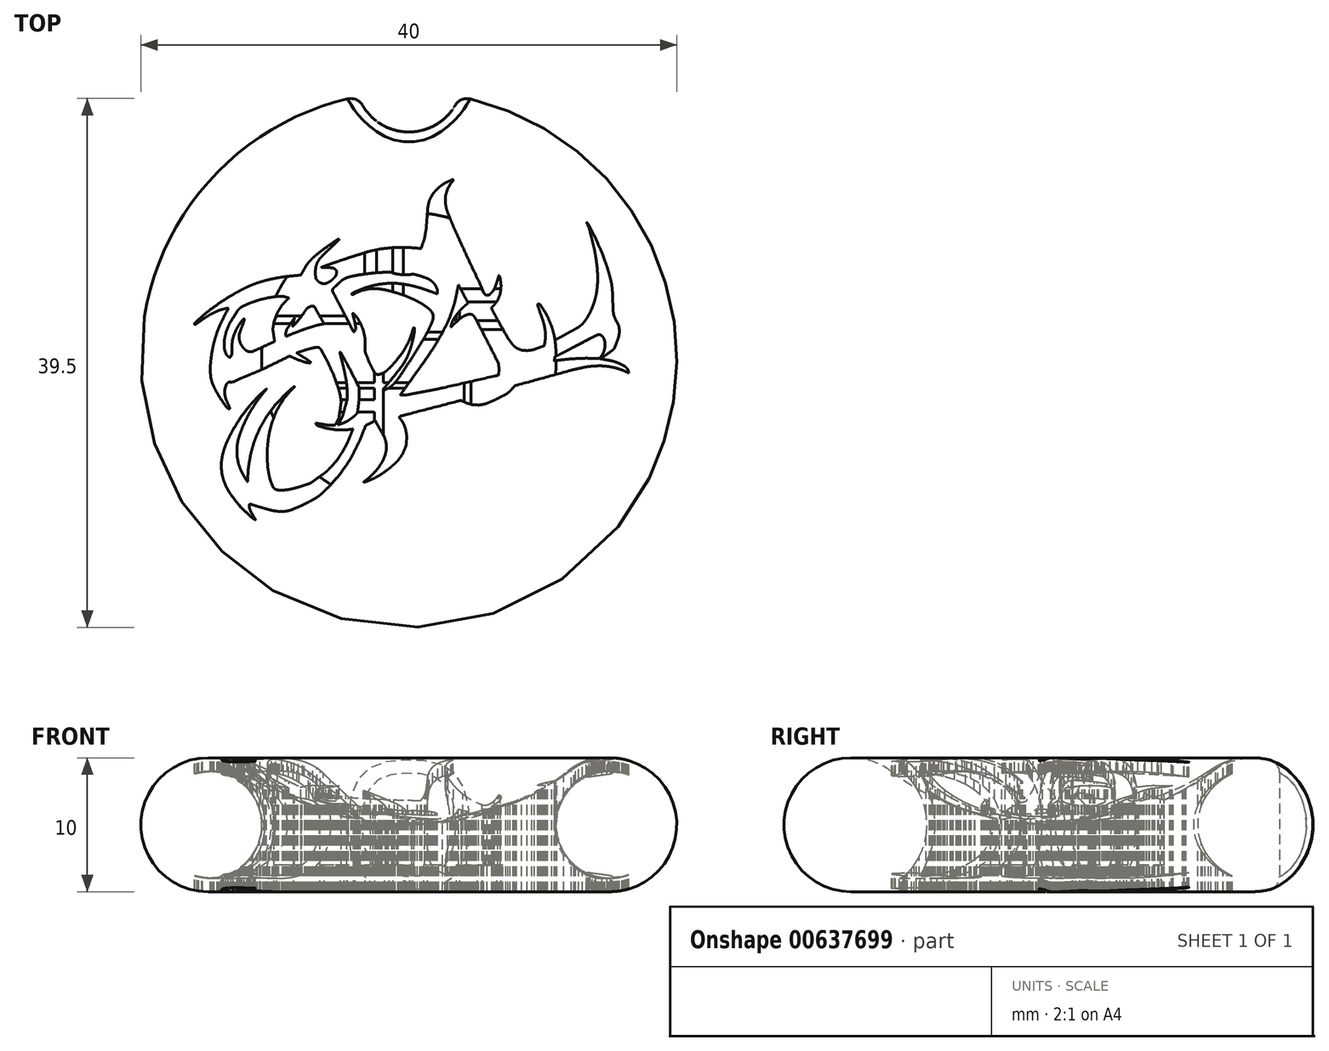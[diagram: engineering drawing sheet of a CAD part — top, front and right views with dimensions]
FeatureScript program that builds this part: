
annotation { "Feature Type Name" : "Feature", "Feature Type Description" : "" }
export const myFeature = defineFeature(function(context is Context, id is Id, definition is map)
    precondition{}
    {
        {
            var Q0;
            Q0=qCreatedBy(makeId("Front.planeOp"),FACE);
            var sketch = newSketch(context, id + "F0", { "sketchPlane" : qUnion([Q0])});
            skArc(sketch, "E0", {"start": v(-12, 9) * mm, "mid": v(-19.74, 6.58) * mm, "end": v(-15, 0) * mm});
            skArc(sketch, "E1", {"start": v(-12, 9) * mm, "mid": v(-6.32, 6.03) * mm, "end": v(0, 5) * mm});
            skLineSegment(sketch, "E2", {"start": v(-15, 0) * mm, "end": v(0, 0) * mm});
            skLineSegment(sketch, "E3", {"start": v(0, 0) * mm, "end": v(0, 5) * mm});
            skSolve(sketch);
        }
        {
            var Q0;
            Q0 = qSketchRegion(id + "F0", true);
            var Q1;
            Q1=makeQuery(id+"F0.imprint","IMPRINT",FACE,{"disambiguationData":[TD([[makeQuery(id+"F0.imprint","IMPRINT",EDGE,{"derivedFrom":sQuery(id+"F0.wireOp",EDGE,"E0")}),1.0]])]});
            var Q2;
            Q2=sQuery(id+"F0.wireOp",EDGE,"E3");
            revolve(context, id + "F1", {"entities" : qUnion([Q0, Q1]), "axis" : qUnion([Q2]), "revolveType" : RevolveType.FULL});
        }
        {
            var Q0;
            Q0=qCreatedBy(makeId("Top.planeOp"),FACE);
            cPlane(context, id + "F2", {"entities" : qUnion([Q0]), "cplaneType" : CPlaneType.OFFSET, "offset" : 10 * mm, "width" : 150 * mm, "height" : 150 * mm});
        }
        {
            var Q0;
            Q0=qCreatedBy(id+"F2.planeOp",FACE);
            var sketch = newSketch(context, id + "F3", { "sketchPlane" : qUnion([Q0])});
            skLineSegment(sketch, "E4", {"start": v(-7.6, 3.85) * mm, "end": v(-7.64, 3.77) * mm});
            skLineSegment(sketch, "E5", {"start": v(-7.64, 3.77) * mm, "end": v(-8.04, 3.2) * mm});
            skLineSegment(sketch, "E6", {"start": v(-8.04, 3.2) * mm, "end": v(-8.48, 2.66) * mm});
            skLineSegment(sketch, "E7", {"start": v(-8.48, 2.66) * mm, "end": v(-8.57, 2.56) * mm});
            skLineSegment(sketch, "E8", {"start": v(-8.57, 2.56) * mm, "end": v(-8.58, 2.56) * mm});
            skLineSegment(sketch, "E9", {"start": v(-8.58, 2.56) * mm, "end": v(-8.6, 2.53) * mm});
            skLineSegment(sketch, "E10", {"start": v(-8.6, 2.53) * mm, "end": v(-8.67, 2.5) * mm});
            skLineSegment(sketch, "E11", {"start": v(-8.67, 2.5) * mm, "end": v(-8.69, 2.48) * mm});
            skLineSegment(sketch, "E12", {"start": v(-8.69, 2.48) * mm, "end": v(-8.68, 2.52) * mm});
            skLineSegment(sketch, "E13", {"start": v(-8.68, 2.52) * mm, "end": v(-8.65, 2.7) * mm});
            skLineSegment(sketch, "E14", {"start": v(-8.65, 2.7) * mm, "end": v(-8.61, 2.84) * mm});
            skLineSegment(sketch, "E15", {"start": v(-8.61, 2.84) * mm, "end": v(-8.6, 2.87) * mm});
            skLineSegment(sketch, "E16", {"start": v(-8.6, 2.87) * mm, "end": v(-8.6, 2.9) * mm});
            skLineSegment(sketch, "E17", {"start": v(-8.6, 2.9) * mm, "end": v(-8.54, 3.1) * mm});
            skLineSegment(sketch, "E18", {"start": v(-8.9, 0.27) * mm, "end": v(-9.02, 0.2) * mm});
            skLineSegment(sketch, "E19", {"start": v(-9.02, 0.2) * mm, "end": v(-10.84, -0.68) * mm});
            skLineSegment(sketch, "E20", {"start": v(-10.84, -0.68) * mm, "end": v(-11.02, -0.77) * mm});
            skLineSegment(sketch, "E21", {"start": v(-11.02, -0.77) * mm, "end": v(-11.15, -0.83) * mm});
            skLineSegment(sketch, "E22", {"start": v(-11.15, -0.83) * mm, "end": v(-12.52, -1.4) * mm});
            skLineSegment(sketch, "E23", {"start": v(-12.52, -1.4) * mm, "end": v(-12.65, -1.45) * mm});
            skLineSegment(sketch, "E24", {"start": v(-12.65, -1.45) * mm, "end": v(-12.69, -1.46) * mm});
            skLineSegment(sketch, "E25", {"start": v(-12.69, -1.46) * mm, "end": v(-12.84, -1.54) * mm});
            skLineSegment(sketch, "E26", {"start": v(-12.84, -1.54) * mm, "end": v(-12.99, -1.62) * mm});
            skLineSegment(sketch, "E27", {"start": v(-12.99, -1.62) * mm, "end": v(-13.02, -1.63) * mm});
            skLineSegment(sketch, "E28", {"start": v(-13.02, -1.63) * mm, "end": v(-13.04, -1.64) * mm});
            skLineSegment(sketch, "E29", {"start": v(-13.04, -1.64) * mm, "end": v(-13.16, -1.68) * mm});
            skLineSegment(sketch, "E30", {"start": v(-13.16, -1.68) * mm, "end": v(-13.28, -1.68) * mm});
            skLineSegment(sketch, "E31", {"start": v(-13.28, -1.68) * mm, "end": v(-13.3, -1.68) * mm});
            skLineSegment(sketch, "E32", {"start": v(-13.3, -1.68) * mm, "end": v(-13.33, -1.68) * mm});
            skLineSegment(sketch, "E33", {"start": v(-13.33, -1.68) * mm, "end": v(-13.4, -1.68) * mm});
            skLineSegment(sketch, "E34", {"start": v(-13.4, -1.68) * mm, "end": v(-13.49, -1.7) * mm});
            skLineSegment(sketch, "E35", {"start": v(-13.49, -1.7) * mm, "end": v(-13.55, -1.75) * mm});
            skLineSegment(sketch, "E36", {"start": v(-13.55, -1.75) * mm, "end": v(-13.6, -1.81) * mm});
            skLineSegment(sketch, "E37", {"start": v(-13.6, -1.81) * mm, "end": v(-13.6, -1.83) * mm});
            skLineSegment(sketch, "E38", {"start": v(-13.6, -1.83) * mm, "end": v(-13.65, -1.9) * mm});
            skLineSegment(sketch, "E39", {"start": v(-13.65, -1.9) * mm, "end": v(-13.73, -2.15) * mm});
            skLineSegment(sketch, "E40", {"start": v(-13.73, -2.15) * mm, "end": v(-13.76, -2.46) * mm});
            skLineSegment(sketch, "E41", {"start": v(-13.76, -2.46) * mm, "end": v(-13.71, -2.77) * mm});
            skLineSegment(sketch, "E42", {"start": v(-13.71, -2.77) * mm, "end": v(-13.63, -3.01) * mm});
            skLineSegment(sketch, "E43", {"start": v(-13.63, -3.01) * mm, "end": v(-13.6, -3.09) * mm});
            skLineSegment(sketch, "E44", {"start": v(-13.6, -3.09) * mm, "end": v(-13.58, -3.13) * mm});
            skLineSegment(sketch, "E45", {"start": v(-13.58, -3.13) * mm, "end": v(-13.37, -3.6) * mm});
            skLineSegment(sketch, "E46", {"start": v(-13.37, -3.6) * mm, "end": v(-13.35, -3.65) * mm});
            skLineSegment(sketch, "E47", {"start": v(-13.35, -3.65) * mm, "end": v(-13.42, -3.7) * mm});
            skLineSegment(sketch, "E48", {"start": v(-13.42, -3.7) * mm, "end": v(-13.43, -3.69) * mm});
            skLineSegment(sketch, "E49", {"start": v(-13.43, -3.69) * mm, "end": v(-13.51, -3.64) * mm});
            skLineSegment(sketch, "E50", {"start": v(-13.51, -3.64) * mm, "end": v(-13.58, -3.58) * mm});
            skLineSegment(sketch, "E51", {"start": v(-13.58, -3.58) * mm, "end": v(-13.6, -3.57) * mm});
            skLineSegment(sketch, "E52", {"start": v(-13.6, -3.57) * mm, "end": v(-13.7, -3.44) * mm});
            skLineSegment(sketch, "E53", {"start": v(-13.7, -3.44) * mm, "end": v(-14.15, -2.78) * mm});
            skLineSegment(sketch, "E54", {"start": v(-14.15, -2.78) * mm, "end": v(-14.53, -2.08) * mm});
            skLineSegment(sketch, "E55", {"start": v(-14.53, -2.08) * mm, "end": v(-14.6, -1.93) * mm});
            skLineSegment(sketch, "E56", {"start": v(-14.6, -1.93) * mm, "end": v(-14.66, -1.8) * mm});
            skLineSegment(sketch, "E57", {"start": v(-14.66, -1.8) * mm, "end": v(-14.78, -1.39) * mm});
            skLineSegment(sketch, "E58", {"start": v(-14.78, -1.39) * mm, "end": v(-14.83, -0.85) * mm});
            skLineSegment(sketch, "E59", {"start": v(-14.83, -0.85) * mm, "end": v(-14.8, -0.3) * mm});
            skLineSegment(sketch, "E60", {"start": v(-14.8, -0.3) * mm, "end": v(-14.76, 0.1) * mm});
            skLineSegment(sketch, "E61", {"start": v(-14.76, 0.1) * mm, "end": v(-14.75, 0.23) * mm});
            skLineSegment(sketch, "E62", {"start": v(-14.75, 0.23) * mm, "end": v(-14.72, 0.46) * mm});
            skLineSegment(sketch, "E63", {"start": v(-14.72, 0.46) * mm, "end": v(-14.58, 1.14) * mm});
            skLineSegment(sketch, "E64", {"start": v(-14.58, 1.14) * mm, "end": v(-14.33, 2.02) * mm});
            skLineSegment(sketch, "E65", {"start": v(-14.33, 2.02) * mm, "end": v(-14.1, 2.58) * mm});
            skLineSegment(sketch, "E66", {"start": v(-13.66, 3.48) * mm, "end": v(-13.54, 3.68) * mm});
            skLineSegment(sketch, "E67", {"start": v(-13.54, 3.68) * mm, "end": v(-13.54, 3.69) * mm});
            skLineSegment(sketch, "E68", {"start": v(-13.54, 3.69) * mm, "end": v(-13.5, 3.75) * mm});
            skLineSegment(sketch, "E69", {"start": v(-13.5, 3.75) * mm, "end": v(-13.48, 3.82) * mm});
            skLineSegment(sketch, "E70", {"start": v(-13.48, 3.82) * mm, "end": v(-13.47, 3.84) * mm});
            skLineSegment(sketch, "E71", {"start": v(-13.47, 3.84) * mm, "end": v(-13.65, 3.82) * mm});
            skLineSegment(sketch, "E72", {"start": v(-13.65, 3.82) * mm, "end": v(-14.18, 3.68) * mm});
            skLineSegment(sketch, "E73", {"start": v(-14.18, 3.68) * mm, "end": v(-14.8, 3.38) * mm});
            skLineSegment(sketch, "E74", {"start": v(-14.8, 3.38) * mm, "end": v(-15.4, 3) * mm});
            skLineSegment(sketch, "E75", {"start": v(-15.4, 3) * mm, "end": v(-15.82, 2.7) * mm});
            skLineSegment(sketch, "E76", {"start": v(-15.82, 2.7) * mm, "end": v(-15.97, 2.6) * mm});
            skLineSegment(sketch, "E77", {"start": v(-15.97, 2.6) * mm, "end": v(-15.97, 2.6) * mm});
            skLineSegment(sketch, "E78", {"start": v(-15.97, 2.6) * mm, "end": v(-16.01, 2.67) * mm});
            skLineSegment(sketch, "E79", {"start": v(-16.01, 2.67) * mm, "end": v(-16.02, 2.67) * mm});
            skLineSegment(sketch, "E80", {"start": v(-16.02, 2.67) * mm, "end": v(-15.99, 2.7) * mm});
            skLineSegment(sketch, "E81", {"start": v(-15.99, 2.7) * mm, "end": v(-15.7, 3) * mm});
            skLineSegment(sketch, "E82", {"start": v(-15.7, 3) * mm, "end": v(-15.67, 3.03) * mm});
            skLineSegment(sketch, "E83", {"start": v(-15.67, 3.03) * mm, "end": v(-15.46, 3.2) * mm});
            skLineSegment(sketch, "E84", {"start": v(-15.46, 3.2) * mm, "end": v(-14.83, 3.73) * mm});
            skLineSegment(sketch, "E85", {"start": v(-14.83, 3.73) * mm, "end": v(-13.94, 4.36) * mm});
            skLineSegment(sketch, "E86", {"start": v(-13.94, 4.36) * mm, "end": v(-13.01, 4.93) * mm});
            skLineSegment(sketch, "E87", {"start": v(-13.01, 4.93) * mm, "end": v(-12.29, 5.32) * mm});
            skLineSegment(sketch, "E88", {"start": v(-12.29, 5.32) * mm, "end": v(-12.04, 5.43) * mm});
            skLineSegment(sketch, "E89", {"start": v(-12.04, 5.43) * mm, "end": v(-11.86, 5.52) * mm});
            skLineSegment(sketch, "E90", {"start": v(-11.86, 5.52) * mm, "end": v(-11.31, 5.73) * mm});
            skLineSegment(sketch, "E91", {"start": v(-11.31, 5.73) * mm, "end": v(-10.57, 5.95) * mm});
            skLineSegment(sketch, "E92", {"start": v(-10.57, 5.95) * mm, "end": v(-9.8, 6.1) * mm});
            skLineSegment(sketch, "E93", {"start": v(-9.8, 6.1) * mm, "end": v(-9.22, 6.2) * mm});
            skLineSegment(sketch, "E94", {"start": v(-9.22, 6.2) * mm, "end": v(-9.02, 6.22) * mm});
            skLineSegment(sketch, "E95", {"start": v(-9.02, 6.22) * mm, "end": v(-8.94, 6.23) * mm});
            skLineSegment(sketch, "E96", {"start": v(-8.94, 6.23) * mm, "end": v(-8.11, 6.3) * mm});
            skLineSegment(sketch, "E97", {"start": v(-8.11, 6.3) * mm, "end": v(-8.07, 6.31) * mm});
            skLineSegment(sketch, "E98", {"start": v(-5.52, -4.9) * mm, "end": v(-5.44, -4.79) * mm});
            skLineSegment(sketch, "E99", {"start": v(-5.44, -4.79) * mm, "end": v(-5.22, -4.36) * mm});
            skLineSegment(sketch, "E100", {"start": v(-5.05, -3.17) * mm, "end": v(-5.12, -2.7) * mm});
            skLineSegment(sketch, "E101", {"start": v(-5.12, -2.7) * mm, "end": v(-5.15, -2.54) * mm});
            skLineSegment(sketch, "E102", {"start": v(-5.15, -2.54) * mm, "end": v(-5.21, -2.3) * mm});
            skLineSegment(sketch, "E103", {"start": v(-5.21, -2.3) * mm, "end": v(-5.6, -1.16) * mm});
            skLineSegment(sketch, "E104", {"start": v(-5.6, -1.16) * mm, "end": v(-6.12, -0.06) * mm});
            skLineSegment(sketch, "E105", {"start": v(-6.12, -0.06) * mm, "end": v(-6.24, 0.16) * mm});
            skLineSegment(sketch, "E106", {"start": v(-6.24, 0.16) * mm, "end": v(-6.26, 0.19) * mm});
            skLineSegment(sketch, "E107", {"start": v(-6.26, 0.19) * mm, "end": v(-6.42, 0.49) * mm});
            skLineSegment(sketch, "E108", {"start": v(-6.42, 0.49) * mm, "end": v(-6.43, 0.52) * mm});
            skLineSegment(sketch, "E109", {"start": v(-6.43, 0.52) * mm, "end": v(-6.45, 0.55) * mm});
            skLineSegment(sketch, "E110", {"start": v(-6.45, 0.55) * mm, "end": v(-6.51, 0.66) * mm});
            skLineSegment(sketch, "E111", {"start": v(-6.51, 0.66) * mm, "end": v(-6.58, 0.77) * mm});
            skLineSegment(sketch, "E112", {"start": v(-6.58, 0.77) * mm, "end": v(-6.64, 0.85) * mm});
            skLineSegment(sketch, "E113", {"start": v(-6.64, 0.85) * mm, "end": v(-6.7, 0.9) * mm});
            skLineSegment(sketch, "E114", {"start": v(-6.7, 0.9) * mm, "end": v(-6.78, 0.92) * mm});
            skLineSegment(sketch, "E115", {"start": v(-6.78, 0.92) * mm, "end": v(-6.88, 0.92) * mm});
            skLineSegment(sketch, "E116", {"start": v(-6.88, 0.92) * mm, "end": v(-7, 0.9) * mm});
            skLineSegment(sketch, "E117", {"start": v(-7, 0.9) * mm, "end": v(-7.12, 0.88) * mm});
            skLineSegment(sketch, "E118", {"start": v(-7.12, 0.88) * mm, "end": v(-7.16, 0.87) * mm});
            skLineSegment(sketch, "E119", {"start": v(-7.16, 0.87) * mm, "end": v(-7.26, 0.84) * mm});
            skLineSegment(sketch, "E120", {"start": v(-7.26, 0.84) * mm, "end": v(-7.79, 0.7) * mm});
            skLineSegment(sketch, "E121", {"start": v(-7.79, 0.7) * mm, "end": v(-8.3, 0.52) * mm});
            skLineSegment(sketch, "E122", {"start": v(-8.3, 0.52) * mm, "end": v(-8.38, 0.5) * mm});
            skLineSegment(sketch, "E123", {"start": v(-5.06, 0.5) * mm, "end": v(-5.06, 0.5) * mm});
            skLineSegment(sketch, "E124", {"start": v(-5.06, 0.5) * mm, "end": v(-5.15, 0.56) * mm});
            skLineSegment(sketch, "E125", {"start": v(-5.15, 0.56) * mm, "end": v(-5.16, 0.56) * mm});
            skLineSegment(sketch, "E126", {"start": v(-5.16, 0.56) * mm, "end": v(-5.15, 0.5) * mm});
            skLineSegment(sketch, "E127", {"start": v(-5.15, 0.5) * mm, "end": v(-5.07, 0.2) * mm});
            skLineSegment(sketch, "E128", {"start": v(-5.07, 0.2) * mm, "end": v(-5, -0.07) * mm});
            skLineSegment(sketch, "E129", {"start": v(-5, -0.07) * mm, "end": v(-4.99, -0.13) * mm});
            skLineSegment(sketch, "E130", {"start": v(-4.99, -0.13) * mm, "end": v(-4.94, -0.3) * mm});
            skLineSegment(sketch, "E131", {"start": v(-4.94, -0.3) * mm, "end": v(-4.82, -0.85) * mm});
            skLineSegment(sketch, "E132", {"start": v(-4.82, -0.85) * mm, "end": v(-4.67, -1.58) * mm});
            skLineSegment(sketch, "E133", {"start": v(-4.67, -1.58) * mm, "end": v(-4.6, -2.31) * mm});
            skLineSegment(sketch, "E134", {"start": v(-4.6, -2.31) * mm, "end": v(-4.6, -2.87) * mm});
            skLineSegment(sketch, "E135", {"start": v(-4.6, -2.87) * mm, "end": v(-4.62, -3.06) * mm});
            skLineSegment(sketch, "E136", {"start": v(-4.94, -4.22) * mm, "end": v(-5.06, -4.46) * mm});
            skLineSegment(sketch, "E137", {"start": v(-5.06, -4.46) * mm, "end": v(-5.25, -4.78) * mm});
            skLineSegment(sketch, "E138", {"start": v(-5.25, -4.78) * mm, "end": v(-5.31, -4.87) * mm});
            skLineSegment(sketch, "E139", {"start": v(-3.85, -4.01) * mm, "end": v(-3.83, -3.89) * mm});
            skLineSegment(sketch, "E140", {"start": v(-3.83, -3.89) * mm, "end": v(-3.72, -3.06) * mm});
            skLineSegment(sketch, "E141", {"start": v(-3.72, -3.06) * mm, "end": v(-3.7, -2.22) * mm});
            skLineSegment(sketch, "E142", {"start": v(-3.7, -2.22) * mm, "end": v(-3.7, -2.05) * mm});
            skLineSegment(sketch, "E143", {"start": v(-3.23, -4.92) * mm, "end": v(-3.28, -5.08) * mm});
            skLineSegment(sketch, "E144", {"start": v(-3.28, -5.08) * mm, "end": v(-3.67, -6.03) * mm});
            skLineSegment(sketch, "E145", {"start": v(-3.67, -6.03) * mm, "end": v(-4.12, -6.97) * mm});
            skLineSegment(sketch, "E146", {"start": v(-4.12, -6.97) * mm, "end": v(-4.22, -7.15) * mm});
            skLineSegment(sketch, "E147", {"start": v(-4.22, -7.15) * mm, "end": v(-4.33, -7.36) * mm});
            skLineSegment(sketch, "E148", {"start": v(-4.33, -7.36) * mm, "end": v(-4.7, -7.95) * mm});
            skLineSegment(sketch, "E149", {"start": v(-4.7, -7.95) * mm, "end": v(-5.26, -8.7) * mm});
            skLineSegment(sketch, "E150", {"start": v(-5.26, -8.7) * mm, "end": v(-5.87, -9.4) * mm});
            skLineSegment(sketch, "E151", {"start": v(-5.87, -9.4) * mm, "end": v(-6.37, -9.89) * mm});
            skLineSegment(sketch, "E152", {"start": v(-6.37, -9.89) * mm, "end": v(-6.54, -10.04) * mm});
            skLineSegment(sketch, "E153", {"start": v(-6.54, -10.04) * mm, "end": v(-6.6, -10.1) * mm});
            skLineSegment(sketch, "E154", {"start": v(-6.6, -10.1) * mm, "end": v(-6.84, -10.28) * mm});
            skLineSegment(sketch, "E155", {"start": v(-6.84, -10.28) * mm, "end": v(-7.18, -10.48) * mm});
            skLineSegment(sketch, "E156", {"start": v(-7.18, -10.48) * mm, "end": v(-7.53, -10.66) * mm});
            skLineSegment(sketch, "E157", {"start": v(-7.53, -10.66) * mm, "end": v(-7.8, -10.8) * mm});
            skLineSegment(sketch, "E158", {"start": v(-7.8, -10.8) * mm, "end": v(-7.88, -10.84) * mm});
            skLineSegment(sketch, "E159", {"start": v(-7.88, -10.84) * mm, "end": v(-7.94, -10.88) * mm});
            skLineSegment(sketch, "E160", {"start": v(-7.94, -10.88) * mm, "end": v(-8.26, -11.01) * mm});
            skLineSegment(sketch, "E161", {"start": v(-8.26, -11.01) * mm, "end": v(-8.59, -11.15) * mm});
            skLineSegment(sketch, "E162", {"start": v(-8.59, -11.15) * mm, "end": v(-8.65, -11.18) * mm});
            skLineSegment(sketch, "E163", {"start": v(-8.65, -11.18) * mm, "end": v(-8.75, -11.22) * mm});
            skLineSegment(sketch, "E164", {"start": v(-8.75, -11.22) * mm, "end": v(-9.08, -11.32) * mm});
            skLineSegment(sketch, "E165", {"start": v(-9.08, -11.32) * mm, "end": v(-9.5, -11.36) * mm});
            skLineSegment(sketch, "E166", {"start": v(-9.5, -11.36) * mm, "end": v(-9.94, -11.32) * mm});
            skLineSegment(sketch, "E167", {"start": v(-9.94, -11.32) * mm, "end": v(-10.26, -11.26) * mm});
            skLineSegment(sketch, "E168", {"start": v(-10.26, -11.26) * mm, "end": v(-10.37, -11.23) * mm});
            skLineSegment(sketch, "E169", {"start": v(-10.37, -11.23) * mm, "end": v(-10.5, -11.2) * mm});
            skLineSegment(sketch, "E170", {"start": v(-10.5, -11.2) * mm, "end": v(-11.12, -11.02) * mm});
            skLineSegment(sketch, "E171", {"start": v(-11.12, -11.02) * mm, "end": v(-11.75, -10.82) * mm});
            skLineSegment(sketch, "E172", {"start": v(-11.75, -10.82) * mm, "end": v(-11.88, -10.78) * mm});
            skLineSegment(sketch, "E173", {"start": v(-11.88, -10.78) * mm, "end": v(-11.9, -10.86) * mm});
            skLineSegment(sketch, "E174", {"start": v(-11.9, -10.86) * mm, "end": v(-11.9, -11.11) * mm});
            skLineSegment(sketch, "E175", {"start": v(-11.9, -11.11) * mm, "end": v(-11.78, -11.4) * mm});
            skLineSegment(sketch, "E176", {"start": v(-11.78, -11.4) * mm, "end": v(-11.62, -11.68) * mm});
            skLineSegment(sketch, "E177", {"start": v(-11.62, -11.68) * mm, "end": v(-11.5, -11.89) * mm});
            skLineSegment(sketch, "E178", {"start": v(-11.5, -11.89) * mm, "end": v(-11.46, -11.97) * mm});
            skLineSegment(sketch, "E179", {"start": v(-11.46, -11.97) * mm, "end": v(-11.47, -11.96) * mm});
            skLineSegment(sketch, "E180", {"start": v(-11.47, -11.96) * mm, "end": v(-11.54, -11.93) * mm});
            skLineSegment(sketch, "E181", {"start": v(-11.54, -11.93) * mm, "end": v(-11.61, -11.89) * mm});
            skLineSegment(sketch, "E182", {"start": v(-11.61, -11.89) * mm, "end": v(-11.62, -11.88) * mm});
            skLineSegment(sketch, "E183", {"start": v(-11.62, -11.88) * mm, "end": v(-11.8, -11.74) * mm});
            skLineSegment(sketch, "E184", {"start": v(-11.8, -11.74) * mm, "end": v(-12.59, -10.98) * mm});
            skLineSegment(sketch, "E185", {"start": v(-12.59, -10.98) * mm, "end": v(-13.27, -10.12) * mm});
            skLineSegment(sketch, "E186", {"start": v(-13.27, -10.12) * mm, "end": v(-13.39, -9.93) * mm});
            skLineSegment(sketch, "E187", {"start": v(-13.39, -9.93) * mm, "end": v(-13.46, -9.82) * mm});
            skLineSegment(sketch, "E188", {"start": v(-13.46, -9.82) * mm, "end": v(-13.64, -9.48) * mm});
            skLineSegment(sketch, "E189", {"start": v(-13.64, -9.48) * mm, "end": v(-13.83, -9.02) * mm});
            skLineSegment(sketch, "E190", {"start": v(-13.83, -9.02) * mm, "end": v(-13.95, -8.57) * mm});
            skLineSegment(sketch, "E191", {"start": v(-13.95, -8.57) * mm, "end": v(-14, -8.1) * mm});
            skLineSegment(sketch, "E192", {"start": v(-14, -8.1) * mm, "end": v(-14, -7.64) * mm});
            skLineSegment(sketch, "E193", {"start": v(-14, -7.64) * mm, "end": v(-13.92, -7.17) * mm});
            skLineSegment(sketch, "E194", {"start": v(-13.92, -7.17) * mm, "end": v(-13.8, -6.7) * mm});
            skLineSegment(sketch, "E195", {"start": v(-13.8, -6.7) * mm, "end": v(-13.66, -6.34) * mm});
            skLineSegment(sketch, "E196", {"start": v(-13.66, -6.34) * mm, "end": v(-13.61, -6.22) * mm});
            skLineSegment(sketch, "E197", {"start": v(-13.61, -6.22) * mm, "end": v(-13.5, -5.97) * mm});
            skLineSegment(sketch, "E198", {"start": v(-13.5, -5.97) * mm, "end": v(-13.12, -5.22) * mm});
            skLineSegment(sketch, "E199", {"start": v(-13.12, -5.22) * mm, "end": v(-12.53, -4.29) * mm});
            skLineSegment(sketch, "E200", {"start": v(-12.53, -4.29) * mm, "end": v(-11.86, -3.41) * mm});
            skLineSegment(sketch, "E201", {"start": v(-11.86, -3.41) * mm, "end": v(-11.3, -2.8) * mm});
            skLineSegment(sketch, "E202", {"start": v(-11.3, -2.8) * mm, "end": v(-11.1, -2.6) * mm});
            skLineSegment(sketch, "E203", {"start": v(-11.1, -2.6) * mm, "end": v(-11.06, -2.57) * mm});
            skLineSegment(sketch, "E204", {"start": v(-11.06, -2.57) * mm, "end": v(-10.88, -2.4) * mm});
            skLineSegment(sketch, "E205", {"start": v(-10.88, -2.4) * mm, "end": v(-10.68, -2.22) * mm});
            skLineSegment(sketch, "E206", {"start": v(-10.68, -2.22) * mm, "end": v(-10.63, -2.18) * mm});
            skLineSegment(sketch, "E207", {"start": v(-10.63, -2.18) * mm, "end": v(-10.64, -2.2) * mm});
            skLineSegment(sketch, "E208", {"start": v(-10.64, -2.2) * mm, "end": v(-10.68, -2.27) * mm});
            skLineSegment(sketch, "E209", {"start": v(-10.68, -2.27) * mm, "end": v(-10.7, -2.3) * mm});
            skLineSegment(sketch, "E210", {"start": v(-10.7, -2.3) * mm, "end": v(-10.7, -2.32) * mm});
            skLineSegment(sketch, "E211", {"start": v(-10.7, -2.32) * mm, "end": v(-10.88, -2.5) * mm});
            skLineSegment(sketch, "E212", {"start": v(-10.88, -2.5) * mm, "end": v(-11.36, -3.12) * mm});
            skLineSegment(sketch, "E213", {"start": v(-11.36, -3.12) * mm, "end": v(-11.9, -3.99) * mm});
            skLineSegment(sketch, "E214", {"start": v(-11.9, -3.99) * mm, "end": v(-12.36, -4.9) * mm});
            skLineSegment(sketch, "E215", {"start": v(-12.36, -4.9) * mm, "end": v(-12.64, -5.63) * mm});
            skLineSegment(sketch, "E216", {"start": v(-12.64, -5.63) * mm, "end": v(-12.7, -5.88) * mm});
            skLineSegment(sketch, "E217", {"start": v(-12.7, -5.88) * mm, "end": v(-12.75, -6.04) * mm});
            skLineSegment(sketch, "E218", {"start": v(-12.75, -6.04) * mm, "end": v(-12.83, -6.52) * mm});
            skLineSegment(sketch, "E219", {"start": v(-12.83, -6.52) * mm, "end": v(-12.84, -7.15) * mm});
            skLineSegment(sketch, "E220", {"start": v(-12.84, -7.15) * mm, "end": v(-12.72, -7.77) * mm});
            skLineSegment(sketch, "E221", {"start": v(-12.72, -7.77) * mm, "end": v(-12.56, -8.24) * mm});
            skLineSegment(sketch, "E222", {"start": v(-12.56, -8.24) * mm, "end": v(-12.48, -8.38) * mm});
            skLineSegment(sketch, "E223", {"start": v(-12.48, -8.38) * mm, "end": v(-12.45, -8.45) * mm});
            skLineSegment(sketch, "E224", {"start": v(-12.45, -8.45) * mm, "end": v(-12.28, -8.76) * mm});
            skLineSegment(sketch, "E225", {"start": v(-12.28, -8.76) * mm, "end": v(-12.08, -9.07) * mm});
            skLineSegment(sketch, "E226", {"start": v(-12.08, -9.07) * mm, "end": v(-12.04, -9.13) * mm});
            skLineSegment(sketch, "E227", {"start": v(-12.04, -9.13) * mm, "end": v(-12.04, -8.86) * mm});
            skLineSegment(sketch, "E228", {"start": v(-12.04, -8.86) * mm, "end": v(-11.98, -8.05) * mm});
            skLineSegment(sketch, "E229", {"start": v(-11.98, -8.05) * mm, "end": v(-11.8, -7.03) * mm});
            skLineSegment(sketch, "E230", {"start": v(-11.8, -7.03) * mm, "end": v(-11.52, -6.06) * mm});
            skLineSegment(sketch, "E231", {"start": v(-11.52, -6.06) * mm, "end": v(-11.14, -5.15) * mm});
            skLineSegment(sketch, "E232", {"start": v(-11.14, -5.15) * mm, "end": v(-10.64, -4.3) * mm});
            skLineSegment(sketch, "E233", {"start": v(-10.64, -4.3) * mm, "end": v(-10.05, -3.48) * mm});
            skLineSegment(sketch, "E234", {"start": v(-10.05, -3.48) * mm, "end": v(-9.36, -2.72) * mm});
            skLineSegment(sketch, "E235", {"start": v(-9.36, -2.72) * mm, "end": v(-8.77, -2.18) * mm});
            skLineSegment(sketch, "E236", {"start": v(-8.77, -2.18) * mm, "end": v(-8.56, -2.01) * mm});
            skLineSegment(sketch, "E237", {"start": v(-8.56, -2.01) * mm, "end": v(-8.56, -2.02) * mm});
            skLineSegment(sketch, "E238", {"start": v(-8.56, -2.02) * mm, "end": v(-8.52, -2.04) * mm});
            skLineSegment(sketch, "E239", {"start": v(-8.52, -2.04) * mm, "end": v(-8.52, -2.05) * mm});
            skLineSegment(sketch, "E240", {"start": v(-8.52, -2.05) * mm, "end": v(-8.53, -2.06) * mm});
            skLineSegment(sketch, "E241", {"start": v(-8.53, -2.06) * mm, "end": v(-8.66, -2.18) * mm});
            skLineSegment(sketch, "E242", {"start": v(-8.66, -2.18) * mm, "end": v(-8.67, -2.2) * mm});
            skLineSegment(sketch, "E243", {"start": v(-8.67, -2.2) * mm, "end": v(-8.85, -2.36) * mm});
            skLineSegment(sketch, "E244", {"start": v(-8.85, -2.36) * mm, "end": v(-9.34, -2.93) * mm});
            skLineSegment(sketch, "E245", {"start": v(-9.34, -2.93) * mm, "end": v(-9.84, -3.75) * mm});
            skLineSegment(sketch, "E246", {"start": v(-9.84, -3.75) * mm, "end": v(-10.2, -4.65) * mm});
            skLineSegment(sketch, "E247", {"start": v(-10.2, -4.65) * mm, "end": v(-10.4, -5.37) * mm});
            skLineSegment(sketch, "E248", {"start": v(-10.4, -5.37) * mm, "end": v(-10.44, -5.61) * mm});
            skLineSegment(sketch, "E249", {"start": v(-10.44, -5.61) * mm, "end": v(-10.48, -5.82) * mm});
            skLineSegment(sketch, "E250", {"start": v(-10.48, -5.82) * mm, "end": v(-10.55, -6.44) * mm});
            skLineSegment(sketch, "E251", {"start": v(-10.55, -6.44) * mm, "end": v(-10.59, -7.26) * mm});
            skLineSegment(sketch, "E252", {"start": v(-10.59, -7.26) * mm, "end": v(-10.53, -8.09) * mm});
            skLineSegment(sketch, "E253", {"start": v(-10.53, -8.09) * mm, "end": v(-10.43, -8.7) * mm});
            skLineSegment(sketch, "E254", {"start": v(-10.43, -8.7) * mm, "end": v(-10.37, -8.9) * mm});
            skLineSegment(sketch, "E255", {"start": v(-10.37, -8.9) * mm, "end": v(-10.36, -8.95) * mm});
            skLineSegment(sketch, "E256", {"start": v(-10.36, -8.95) * mm, "end": v(-10.28, -9.17) * mm});
            skLineSegment(sketch, "E257", {"start": v(-10.28, -9.17) * mm, "end": v(-10.2, -9.4) * mm});
            skLineSegment(sketch, "E258", {"start": v(-10.2, -9.4) * mm, "end": v(-10.17, -9.44) * mm});
            skLineSegment(sketch, "E259", {"start": v(-10.17, -9.44) * mm, "end": v(-10.16, -9.47) * mm});
            skLineSegment(sketch, "E260", {"start": v(-10.16, -9.47) * mm, "end": v(-10.1, -9.57) * mm});
            skLineSegment(sketch, "E261", {"start": v(-10.1, -9.57) * mm, "end": v(-10, -9.66) * mm});
            skLineSegment(sketch, "E262", {"start": v(-10, -9.66) * mm, "end": v(-9.88, -9.72) * mm});
            skLineSegment(sketch, "E263", {"start": v(-9.88, -9.72) * mm, "end": v(-9.77, -9.74) * mm});
            skLineSegment(sketch, "E264", {"start": v(-9.77, -9.74) * mm, "end": v(-9.74, -9.75) * mm});
            skLineSegment(sketch, "E265", {"start": v(-9.74, -9.75) * mm, "end": v(-9.64, -9.76) * mm});
            skLineSegment(sketch, "E266", {"start": v(-9.64, -9.76) * mm, "end": v(-9.36, -9.75) * mm});
            skLineSegment(sketch, "E267", {"start": v(-9.36, -9.75) * mm, "end": v(-9, -9.71) * mm});
            skLineSegment(sketch, "E268", {"start": v(-9, -9.71) * mm, "end": v(-8.63, -9.63) * mm});
            skLineSegment(sketch, "E269", {"start": v(-8.63, -9.63) * mm, "end": v(-8.36, -9.56) * mm});
            skLineSegment(sketch, "E270", {"start": v(-8.36, -9.56) * mm, "end": v(-8.28, -9.54) * mm});
            skLineSegment(sketch, "E271", {"start": v(-8.28, -9.54) * mm, "end": v(-8.2, -9.52) * mm});
            skLineSegment(sketch, "E272", {"start": v(-8.2, -9.52) * mm, "end": v(-7.48, -9.28) * mm});
            skLineSegment(sketch, "E273", {"start": v(-7.48, -9.28) * mm, "end": v(-7.4, -9.25) * mm});
            skLineSegment(sketch, "E274", {"start": v(-7.4, -9.25) * mm, "end": v(-7.36, -9.23) * mm});
            skLineSegment(sketch, "E275", {"start": v(-7.36, -9.23) * mm, "end": v(-7.14, -9.09) * mm});
            skLineSegment(sketch, "E276", {"start": v(-7.14, -9.09) * mm, "end": v(-6.92, -8.92) * mm});
            skLineSegment(sketch, "E277", {"start": v(-6.92, -8.92) * mm, "end": v(-6.88, -8.9) * mm});
            skLineSegment(sketch, "E278", {"start": v(-6.88, -8.9) * mm, "end": v(-6.83, -8.86) * mm});
            skLineSegment(sketch, "E279", {"start": v(-6.83, -8.86) * mm, "end": v(-6.36, -8.53) * mm});
            skLineSegment(sketch, "E280", {"start": v(-6.36, -8.53) * mm, "end": v(-6.32, -8.5) * mm});
            skLineSegment(sketch, "E281", {"start": v(-6.32, -8.5) * mm, "end": v(-6.18, -8.38) * mm});
            skLineSegment(sketch, "E282", {"start": v(-6.18, -8.38) * mm, "end": v(-5.79, -8) * mm});
            skLineSegment(sketch, "E283", {"start": v(-5.79, -8) * mm, "end": v(-5.33, -7.46) * mm});
            skLineSegment(sketch, "E284", {"start": v(-5.33, -7.46) * mm, "end": v(-4.94, -6.87) * mm});
            skLineSegment(sketch, "E285", {"start": v(-4.94, -6.87) * mm, "end": v(-4.69, -6.4) * mm});
            skLineSegment(sketch, "E286", {"start": v(-4.69, -6.4) * mm, "end": v(-4.6, -6.24) * mm});
            skLineSegment(sketch, "E287", {"start": v(-4.6, -6.24) * mm, "end": v(-4.57, -6.15) * mm});
            skLineSegment(sketch, "E288", {"start": v(-4.57, -6.15) * mm, "end": v(-4.2, -5.26) * mm});
            skLineSegment(sketch, "E289", {"start": v(-4.2, -5.26) * mm, "end": v(-4.17, -5.19) * mm});
            skLineSegment(sketch, "E290", {"start": v(-4.12, 2.06) * mm, "end": v(-4.11, 2.06) * mm});
            skLineSegment(sketch, "E291", {"start": v(-4.11, 2.06) * mm, "end": v(-4.06, 2.12) * mm});
            skLineSegment(sketch, "E292", {"start": v(-4.06, 2.12) * mm, "end": v(-4, 2.2) * mm});
            skLineSegment(sketch, "E293", {"start": v(-4, 2.2) * mm, "end": v(-3.97, 2.28) * mm});
            skLineSegment(sketch, "E294", {"start": v(-3.97, 2.28) * mm, "end": v(-3.97, 2.35) * mm});
            skLineSegment(sketch, "E295", {"start": v(-3.97, 2.35) * mm, "end": v(-3.97, 2.37) * mm});
            skLineSegment(sketch, "E296", {"start": v(-3.97, 2.37) * mm, "end": v(-3.97, 2.44) * mm});
            skLineSegment(sketch, "E297", {"start": v(-3.97, 2.44) * mm, "end": v(-4.03, 2.76) * mm});
            skLineSegment(sketch, "E298", {"start": v(-4.03, 2.76) * mm, "end": v(-4.1, 3.08) * mm});
            skLineSegment(sketch, "E299", {"start": v(-4.1, 3.08) * mm, "end": v(-4.12, 3.15) * mm});
            skLineSegment(sketch, "E300", {"start": v(-4.12, 3.15) * mm, "end": v(-4.12, 3.17) * mm});
            skLineSegment(sketch, "E301", {"start": v(-4.12, 3.17) * mm, "end": v(-4.2, 3.4) * mm});
            skLineSegment(sketch, "E302", {"start": v(-4.2, 3.4) * mm, "end": v(-4.2, 3.43) * mm});
            skLineSegment(sketch, "E303", {"start": v(-4.2, 3.43) * mm, "end": v(-4.2, 3.43) * mm});
            skLineSegment(sketch, "E304", {"start": v(-4.2, 3.43) * mm, "end": v(-4.16, 3.46) * mm});
            skLineSegment(sketch, "E305", {"start": v(-4.16, 3.46) * mm, "end": v(-4.15, 3.47) * mm});
            skLineSegment(sketch, "E306", {"start": v(-4.15, 3.47) * mm, "end": v(-4.14, 3.45) * mm});
            skLineSegment(sketch, "E307", {"start": v(-4.14, 3.45) * mm, "end": v(-4.05, 3.36) * mm});
            skLineSegment(sketch, "E308", {"start": v(-4.05, 3.36) * mm, "end": v(-3.96, 3.27) * mm});
            skLineSegment(sketch, "E309", {"start": v(-3.96, 3.27) * mm, "end": v(-3.95, 3.25) * mm});
            skLineSegment(sketch, "E310", {"start": v(-3.95, 3.25) * mm, "end": v(-3.85, 3.13) * mm});
            skLineSegment(sketch, "E311", {"start": v(-3.85, 3.13) * mm, "end": v(-3.62, 2.73) * mm});
            skLineSegment(sketch, "E312", {"start": v(-3.62, 2.73) * mm, "end": v(-3.4, 2.17) * mm});
            skLineSegment(sketch, "E313", {"start": v(-3.4, 2.17) * mm, "end": v(-3.28, 1.58) * mm});
            skLineSegment(sketch, "E314", {"start": v(-3.28, 1.58) * mm, "end": v(-3.26, 1.11) * mm});
            skLineSegment(sketch, "E315", {"start": v(-3.26, 1.11) * mm, "end": v(-3.27, 0.96) * mm});
            skLineSegment(sketch, "E316", {"start": v(-3.27, 0.96) * mm, "end": v(-3.27, 0.93) * mm});
            skLineSegment(sketch, "E317", {"start": v(-3.27, 0.93) * mm, "end": v(-3.28, 0.82) * mm});
            skLineSegment(sketch, "E318", {"start": v(-3.28, 0.82) * mm, "end": v(-3.27, 0.68) * mm});
            skLineSegment(sketch, "E319", {"start": v(-3.27, 0.68) * mm, "end": v(-3.25, 0.55) * mm});
            skLineSegment(sketch, "E320", {"start": v(-3.25, 0.55) * mm, "end": v(-3.22, 0.45) * mm});
            skLineSegment(sketch, "E321", {"start": v(-3.22, 0.45) * mm, "end": v(-3.2, 0.42) * mm});
            skLineSegment(sketch, "E322", {"start": v(-3.2, 0.42) * mm, "end": v(-3.18, 0.36) * mm});
            skLineSegment(sketch, "E323", {"start": v(-3.18, 0.36) * mm, "end": v(-2.96, -0.21) * mm});
            skLineSegment(sketch, "E324", {"start": v(-9.18, 1.73) * mm, "end": v(-9, 1.8) * mm});
            skLineSegment(sketch, "E325", {"start": v(-9, 1.8) * mm, "end": v(-7.97, 2.21) * mm});
            skLineSegment(sketch, "E326", {"start": v(-7.97, 2.21) * mm, "end": v(-6.92, 2.55) * mm});
            skLineSegment(sketch, "E327", {"start": v(-6.92, 2.55) * mm, "end": v(-6.7, 2.6) * mm});
            skLineSegment(sketch, "E328", {"start": v(-6.7, 2.6) * mm, "end": v(-6.67, 2.6) * mm});
            skLineSegment(sketch, "E329", {"start": v(-6.67, 2.6) * mm, "end": v(-6.34, 2.67) * mm});
            skLineSegment(sketch, "E330", {"start": v(-6.34, 2.67) * mm, "end": v(-6.33, 2.67) * mm});
            skLineSegment(sketch, "E331", {"start": v(-8.96, 4.59) * mm, "end": v(-9, 4.61) * mm});
            skLineSegment(sketch, "E332", {"start": v(-9, 4.61) * mm, "end": v(-9.33, 4.71) * mm});
            skLineSegment(sketch, "E333", {"start": v(-9.33, 4.71) * mm, "end": v(-9.7, 4.72) * mm});
            skLineSegment(sketch, "E334", {"start": v(-9.7, 4.72) * mm, "end": v(-9.78, 4.72) * mm});
            skLineSegment(sketch, "E335", {"start": v(-9.78, 4.72) * mm, "end": v(-9.95, 4.7) * mm});
            skLineSegment(sketch, "E336", {"start": v(-9.95, 4.7) * mm, "end": v(-10.47, 4.62) * mm});
            skLineSegment(sketch, "E337", {"start": v(-10.47, 4.62) * mm, "end": v(-11.16, 4.47) * mm});
            skLineSegment(sketch, "E338", {"start": v(-11.16, 4.47) * mm, "end": v(-11.82, 4.24) * mm});
            skLineSegment(sketch, "E339", {"start": v(-11.82, 4.24) * mm, "end": v(-12.3, 4.03) * mm});
            skLineSegment(sketch, "E340", {"start": v(-12.3, 4.03) * mm, "end": v(-12.46, 3.94) * mm});
            skLineSegment(sketch, "E341", {"start": v(-12.46, 3.94) * mm, "end": v(-12.48, 3.93) * mm});
            skLineSegment(sketch, "E342", {"start": v(-12.48, 3.93) * mm, "end": v(-12.59, 3.86) * mm});
            skLineSegment(sketch, "E343", {"start": v(-12.59, 3.86) * mm, "end": v(-12.68, 3.78) * mm});
            skLineSegment(sketch, "E344", {"start": v(-12.68, 3.78) * mm, "end": v(-12.7, 3.76) * mm});
            skLineSegment(sketch, "E345", {"start": v(-12.7, 3.76) * mm, "end": v(-12.8, 3.63) * mm});
            skLineSegment(sketch, "E346", {"start": v(-13.4, 2.67) * mm, "end": v(-13.64, 2.08) * mm});
            skLineSegment(sketch, "E347", {"start": v(-13.64, 2.08) * mm, "end": v(-13.75, 1.6) * mm});
            skLineSegment(sketch, "E348", {"start": v(-13.75, 1.6) * mm, "end": v(-13.77, 1.44) * mm});
            skLineSegment(sketch, "E349", {"start": v(-13.77, 1.44) * mm, "end": v(-13.78, 1.36) * mm});
            skLineSegment(sketch, "E350", {"start": v(-13.78, 1.36) * mm, "end": v(-13.8, 1.14) * mm});
            skLineSegment(sketch, "E351", {"start": v(-13.8, 1.14) * mm, "end": v(-13.78, 0.86) * mm});
            skLineSegment(sketch, "E352", {"start": v(-13.78, 0.86) * mm, "end": v(-13.71, 0.58) * mm});
            skLineSegment(sketch, "E353", {"start": v(-13.71, 0.58) * mm, "end": v(-13.62, 0.38) * mm});
            skLineSegment(sketch, "E354", {"start": v(-13.62, 0.38) * mm, "end": v(-13.58, 0.32) * mm});
            skLineSegment(sketch, "E355", {"start": v(-13.58, 0.32) * mm, "end": v(-13.57, 0.3) * mm});
            skLineSegment(sketch, "E356", {"start": v(-13.57, 0.3) * mm, "end": v(-13.48, 0.23) * mm});
            skLineSegment(sketch, "E357", {"start": v(-13.48, 0.23) * mm, "end": v(-13.37, 0.16) * mm});
            skLineSegment(sketch, "E358", {"start": v(-13.37, 0.16) * mm, "end": v(-13.35, 0.15) * mm});
            skLineSegment(sketch, "E359", {"start": v(-13.35, 0.15) * mm, "end": v(-13.34, 0.17) * mm});
            skLineSegment(sketch, "E360", {"start": v(-13.34, 0.17) * mm, "end": v(-13.27, 0.27) * mm});
            skLineSegment(sketch, "E361", {"start": v(-13.27, 0.27) * mm, "end": v(-13.23, 0.37) * mm});
            skLineSegment(sketch, "E362", {"start": v(-13.23, 0.37) * mm, "end": v(-13.22, 0.4) * mm});
            skLineSegment(sketch, "E363", {"start": v(-13.22, 0.4) * mm, "end": v(-13.22, 0.48) * mm});
            skLineSegment(sketch, "E364", {"start": v(-13.22, 0.48) * mm, "end": v(-13.2, 0.91) * mm});
            skLineSegment(sketch, "E365", {"start": v(-13.2, 0.91) * mm, "end": v(-13.19, 1.34) * mm});
            skLineSegment(sketch, "E366", {"start": v(-13.19, 1.34) * mm, "end": v(-13.17, 1.43) * mm});
            skLineSegment(sketch, "E367", {"start": v(-13.17, 1.43) * mm, "end": v(-13.15, 1.53) * mm});
            skLineSegment(sketch, "E368", {"start": v(-13.15, 1.53) * mm, "end": v(-13.06, 1.83) * mm});
            skLineSegment(sketch, "E369", {"start": v(-13.06, 1.83) * mm, "end": v(-12.9, 2.21) * mm});
            skLineSegment(sketch, "E370", {"start": v(-12.9, 2.21) * mm, "end": v(-12.7, 2.58) * mm});
            skLineSegment(sketch, "E371", {"start": v(-12.7, 2.58) * mm, "end": v(-12.51, 2.84) * mm});
            skLineSegment(sketch, "E372", {"start": v(-12.51, 2.84) * mm, "end": v(-12.45, 2.92) * mm});
            skLineSegment(sketch, "E373", {"start": v(-12.45, 2.92) * mm, "end": v(-12.44, 2.93) * mm});
            skLineSegment(sketch, "E374", {"start": v(-12.44, 2.93) * mm, "end": v(-12.38, 2.99) * mm});
            skLineSegment(sketch, "E375", {"start": v(-12.38, 2.99) * mm, "end": v(-12.32, 3.03) * mm});
            skLineSegment(sketch, "E376", {"start": v(-12.32, 3.03) * mm, "end": v(-12.3, 3.04) * mm});
            skLineSegment(sketch, "E377", {"start": v(-12.3, 3.04) * mm, "end": v(-12.3, 3.04) * mm});
            skLineSegment(sketch, "E378", {"start": v(-12.3, 3.04) * mm, "end": v(-12.27, 3.02) * mm});
            skLineSegment(sketch, "E379", {"start": v(-12.27, 3.02) * mm, "end": v(-12.26, 3.01) * mm});
            skLineSegment(sketch, "E380", {"start": v(-12.26, 3.01) * mm, "end": v(-12.27, 3) * mm});
            skLineSegment(sketch, "E381", {"start": v(-12.27, 3) * mm, "end": v(-12.33, 2.81) * mm});
            skLineSegment(sketch, "E382", {"start": v(-12.33, 2.81) * mm, "end": v(-12.34, 2.8) * mm});
            skLineSegment(sketch, "E383", {"start": v(-12.34, 2.8) * mm, "end": v(-12.36, 2.72) * mm});
            skLineSegment(sketch, "E384", {"start": v(-12.36, 2.72) * mm, "end": v(-12.62, 2.02) * mm});
            skLineSegment(sketch, "E385", {"start": v(-12.62, 2.02) * mm, "end": v(-12.64, 1.95) * mm});
            skLineSegment(sketch, "E386", {"start": v(-12.64, 1.95) * mm, "end": v(-12.67, 1.86) * mm});
            skLineSegment(sketch, "E387", {"start": v(-12.67, 1.86) * mm, "end": v(-12.68, 1.57) * mm});
            skLineSegment(sketch, "E388", {"start": v(-12.68, 1.57) * mm, "end": v(-12.58, 1.22) * mm});
            skLineSegment(sketch, "E389", {"start": v(-12.58, 1.22) * mm, "end": v(-12.39, 0.9) * mm});
            skLineSegment(sketch, "E390", {"start": v(-12.39, 0.9) * mm, "end": v(-12.22, 0.73) * mm});
            skLineSegment(sketch, "E391", {"start": v(-12.22, 0.73) * mm, "end": v(-12.15, 0.68) * mm});
            skLineSegment(sketch, "E392", {"start": v(-12.15, 0.68) * mm, "end": v(-12.12, 0.66) * mm});
            skLineSegment(sketch, "E393", {"start": v(-12.12, 0.66) * mm, "end": v(-12.02, 0.6) * mm});
            skLineSegment(sketch, "E394", {"start": v(-12.02, 0.6) * mm, "end": v(-11.89, 0.58) * mm});
            skLineSegment(sketch, "E395", {"start": v(-11.89, 0.58) * mm, "end": v(-11.75, 0.58) * mm});
            skLineSegment(sketch, "E396", {"start": v(-11.75, 0.58) * mm, "end": v(-11.65, 0.61) * mm});
            skLineSegment(sketch, "E397", {"start": v(-11.65, 0.61) * mm, "end": v(-11.61, 0.63) * mm});
            skLineSegment(sketch, "E398", {"start": v(-11.61, 0.63) * mm, "end": v(-11.5, 0.68) * mm});
            skLineSegment(sketch, "E399", {"start": v(-11.5, 0.68) * mm, "end": v(-10.4, 1.18) * mm});
            skLineSegment(sketch, "E400", {"start": v(-10.4, 1.18) * mm, "end": v(-10.3, 1.23) * mm});
            skLineSegment(sketch, "E401", {"start": v(-10.3, 1.23) * mm, "end": v(-10.27, 1.24) * mm});
            skLineSegment(sketch, "E402", {"start": v(-10.27, 1.24) * mm, "end": v(-10.02, 1.35) * mm});
            skLineSegment(sketch, "E403", {"start": v(-2.96, -0.21) * mm, "end": v(-2.67, -0.78) * mm});
            skLineSegment(sketch, "E404", {"start": v(-2.67, -0.78) * mm, "end": v(-2.64, -0.84) * mm});
            skLineSegment(sketch, "E405", {"start": v(-2.64, -0.84) * mm, "end": v(-2.62, -0.86) * mm});
            skLineSegment(sketch, "E406", {"start": v(-2.62, -0.86) * mm, "end": v(-2.58, -0.94) * mm});
            skLineSegment(sketch, "E407", {"start": v(-2.58, -0.94) * mm, "end": v(-2.52, -1.01) * mm});
            skLineSegment(sketch, "E408", {"start": v(-2.52, -1.01) * mm, "end": v(-2.46, -1.07) * mm});
            skLineSegment(sketch, "E409", {"start": v(-2.46, -1.07) * mm, "end": v(-2.4, -1.1) * mm});
            skLineSegment(sketch, "E410", {"start": v(-2.4, -1.1) * mm, "end": v(-2.32, -1.12) * mm});
            skLineSegment(sketch, "E411", {"start": v(-2.32, -1.12) * mm, "end": v(-2.24, -1.11) * mm});
            skLineSegment(sketch, "E412", {"start": v(-2.24, -1.11) * mm, "end": v(-2.14, -1.09) * mm});
            skLineSegment(sketch, "E413", {"start": v(-2.14, -1.09) * mm, "end": v(-2.06, -1.06) * mm});
            skLineSegment(sketch, "E414", {"start": v(-2.06, -1.06) * mm, "end": v(-2.03, -1.05) * mm});
            skLineSegment(sketch, "E415", {"start": v(-2.03, -1.05) * mm, "end": v(-2, -1.03) * mm});
            skLineSegment(sketch, "E416", {"start": v(-2, -1.03) * mm, "end": v(-1.83, -0.95) * mm});
            skLineSegment(sketch, "E417", {"start": v(-1.83, -0.95) * mm, "end": v(-1.68, -0.84) * mm});
            skLineSegment(sketch, "E418", {"start": v(-1.68, -0.84) * mm, "end": v(-1.65, -0.82) * mm});
            skLineSegment(sketch, "E419", {"start": v(-1.65, -0.82) * mm, "end": v(-1.48, -0.66) * mm});
            skLineSegment(sketch, "E420", {"start": v(-1.48, -0.66) * mm, "end": v(-1.02, -0.17) * mm});
            skLineSegment(sketch, "E421", {"start": v(-1.02, -0.17) * mm, "end": v(-0.47, 0.52) * mm});
            skLineSegment(sketch, "E422", {"start": v(-0.47, 0.52) * mm, "end": v(-0.03, 1.3) * mm});
            skLineSegment(sketch, "E423", {"start": v(-0.03, 1.3) * mm, "end": v(0.22, 1.93) * mm});
            skLineSegment(sketch, "E424", {"start": v(0.22, 1.93) * mm, "end": v(0.27, 2.15) * mm});
            skLineSegment(sketch, "E425", {"start": v(0.27, 2.15) * mm, "end": v(0.28, 2.17) * mm});
            skLineSegment(sketch, "E426", {"start": v(0.28, 2.17) * mm, "end": v(0.35, 2.36) * mm});
            skLineSegment(sketch, "E427", {"start": v(0.35, 2.36) * mm, "end": v(0.35, 2.38) * mm});
            skLineSegment(sketch, "E428", {"start": v(0.35, 2.38) * mm, "end": v(0.36, 2.38) * mm});
            skLineSegment(sketch, "E429", {"start": v(0.36, 2.38) * mm, "end": v(0.41, 2.37) * mm});
            skLineSegment(sketch, "E430", {"start": v(0.41, 2.37) * mm, "end": v(0.42, 2.37) * mm});
            skLineSegment(sketch, "E431", {"start": v(0.42, 2.37) * mm, "end": v(0.42, 2.35) * mm});
            skLineSegment(sketch, "E432", {"start": v(0.42, 2.35) * mm, "end": v(0.43, 2.26) * mm});
            skLineSegment(sketch, "E433", {"start": v(0.43, 2.26) * mm, "end": v(0.43, 2.16) * mm});
            skLineSegment(sketch, "E434", {"start": v(0.43, 2.16) * mm, "end": v(0.42, 2.14) * mm});
            skLineSegment(sketch, "E435", {"start": v(0.42, 2.14) * mm, "end": v(0.4, 1.98) * mm});
            skLineSegment(sketch, "E436", {"start": v(0.4, 1.98) * mm, "end": v(0.3, 1.48) * mm});
            skLineSegment(sketch, "E437", {"start": v(0.3, 1.48) * mm, "end": v(0.13, 0.83) * mm});
            skLineSegment(sketch, "E438", {"start": v(0.13, 0.83) * mm, "end": v(-0.12, 0.2) * mm});
            skLineSegment(sketch, "E439", {"start": v(-0.12, 0.2) * mm, "end": v(-0.36, -0.25) * mm});
            skLineSegment(sketch, "E440", {"start": v(-0.36, -0.25) * mm, "end": v(-0.45, -0.39) * mm});
            skLineSegment(sketch, "E441", {"start": v(-0.45, -0.39) * mm, "end": v(-0.55, -0.53) * mm});
            skLineSegment(sketch, "E442", {"start": v(-0.55, -0.53) * mm, "end": v(-1.08, -1.2) * mm});
            skLineSegment(sketch, "E443", {"start": v(-1.08, -1.2) * mm, "end": v(-1.63, -1.87) * mm});
            skLineSegment(sketch, "E444", {"start": v(-1.63, -1.87) * mm, "end": v(-1.74, -2) * mm});
            skLineSegment(sketch, "E445", {"start": v(-1.74, -2) * mm, "end": v(-1.75, -2.03) * mm});
            skLineSegment(sketch, "E446", {"start": v(-1.75, -2.03) * mm, "end": v(-1.88, -2.23) * mm});
            skLineSegment(sketch, "E447", {"start": v(-1.88, -2.23) * mm, "end": v(-1.89, -2.25) * mm});
            skLineSegment(sketch, "E448", {"start": v(-1.89, -2.25) * mm, "end": v(-1.88, -2.25) * mm});
            skLineSegment(sketch, "E449", {"start": v(-1.88, -2.25) * mm, "end": v(-1.84, -2.28) * mm});
            skLineSegment(sketch, "E450", {"start": v(-1.84, -2.28) * mm, "end": v(-1.84, -2.28) * mm});
            skLineSegment(sketch, "E451", {"start": v(-1.84, -2.28) * mm, "end": v(-1.76, -2.25) * mm});
            skLineSegment(sketch, "E452", {"start": v(-1.76, -2.25) * mm, "end": v(-1.52, -2.13) * mm});
            skLineSegment(sketch, "E453", {"start": v(-1.52, -2.13) * mm, "end": v(-1.26, -1.95) * mm});
            skLineSegment(sketch, "E454", {"start": v(-1.26, -1.95) * mm, "end": v(-1, -1.7) * mm});
            skLineSegment(sketch, "E455", {"start": v(-1, -1.7) * mm, "end": v(-0.78, -1.4) * mm});
            skLineSegment(sketch, "E456", {"start": v(-0.78, -1.4) * mm, "end": v(-0.7, -1.3) * mm});
            skLineSegment(sketch, "E457", {"start": v(-0.7, -1.3) * mm, "end": v(-0.55, -1.06) * mm});
            skLineSegment(sketch, "E458", {"start": v(-0.55, -1.06) * mm, "end": v(0.22, 0.11) * mm});
            skLineSegment(sketch, "E459", {"start": v(0.22, 0.11) * mm, "end": v(0.96, 1.3) * mm});
            skLineSegment(sketch, "E460", {"start": v(0.96, 1.3) * mm, "end": v(1.1, 1.54) * mm});
            skLineSegment(sketch, "E461", {"start": v(1.1, 1.54) * mm, "end": v(1.16, 1.64) * mm});
            skLineSegment(sketch, "E462", {"start": v(1.16, 1.64) * mm, "end": v(1.44, 2.16) * mm});
            skLineSegment(sketch, "E463", {"start": v(1.44, 2.16) * mm, "end": v(1.68, 2.7) * mm});
            skLineSegment(sketch, "E464", {"start": v(1.68, 2.7) * mm, "end": v(1.73, 2.8) * mm});
            skLineSegment(sketch, "E465", {"start": v(1.73, 2.8) * mm, "end": v(1.76, 2.88) * mm});
            skLineSegment(sketch, "E466", {"start": v(1.76, 2.88) * mm, "end": v(1.82, 3.11) * mm});
            skLineSegment(sketch, "E467", {"start": v(1.82, 3.11) * mm, "end": v(1.8, 3.37) * mm});
            skLineSegment(sketch, "E468", {"start": v(1.8, 3.37) * mm, "end": v(1.68, 3.6) * mm});
            skLineSegment(sketch, "E469", {"start": v(1.68, 3.6) * mm, "end": v(1.51, 3.78) * mm});
            skLineSegment(sketch, "E470", {"start": v(1.51, 3.78) * mm, "end": v(1.45, 3.83) * mm});
            skLineSegment(sketch, "E471", {"start": v(1.45, 3.83) * mm, "end": v(1.42, 3.85) * mm});
            skLineSegment(sketch, "E472", {"start": v(1.42, 3.85) * mm, "end": v(1.18, 4.03) * mm});
            skLineSegment(sketch, "E473", {"start": v(1.18, 4.03) * mm, "end": v(1.15, 4.05) * mm});
            skLineSegment(sketch, "E474", {"start": v(1.15, 4.05) * mm, "end": v(1, 4.16) * mm});
            skLineSegment(sketch, "E475", {"start": v(1, 4.16) * mm, "end": v(0.49, 4.43) * mm});
            skLineSegment(sketch, "E476", {"start": v(0.49, 4.43) * mm, "end": v(-0.2, 4.74) * mm});
            skLineSegment(sketch, "E477", {"start": v(-0.2, 4.74) * mm, "end": v(-0.92, 4.98) * mm});
            skLineSegment(sketch, "E478", {"start": v(-0.92, 4.98) * mm, "end": v(-1.47, 5.14) * mm});
            skLineSegment(sketch, "E479", {"start": v(-1.47, 5.14) * mm, "end": v(-1.66, 5.18) * mm});
            skLineSegment(sketch, "E480", {"start": v(-1.66, 5.18) * mm, "end": v(-1.81, 5.22) * mm});
            skLineSegment(sketch, "E481", {"start": v(-1.81, 5.22) * mm, "end": v(-2.28, 5.29) * mm});
            skLineSegment(sketch, "E482", {"start": v(-2.28, 5.29) * mm, "end": v(-2.9, 5.3) * mm});
            skLineSegment(sketch, "E483", {"start": v(-2.9, 5.3) * mm, "end": v(-3.5, 5.17) * mm});
            skLineSegment(sketch, "E484", {"start": v(-3.5, 5.17) * mm, "end": v(-3.95, 4.98) * mm});
            skLineSegment(sketch, "E485", {"start": v(-3.95, 4.98) * mm, "end": v(-4.08, 4.9) * mm});
            skLineSegment(sketch, "E486", {"start": v(-4.08, 4.9) * mm, "end": v(-4.1, 4.9) * mm});
            skLineSegment(sketch, "E487", {"start": v(-4.1, 4.9) * mm, "end": v(-4.15, 4.87) * mm});
            skLineSegment(sketch, "E488", {"start": v(-4.15, 4.87) * mm, "end": v(-4.22, 4.86) * mm});
            skLineSegment(sketch, "E489", {"start": v(-4.22, 4.86) * mm, "end": v(-4.23, 4.86) * mm});
            skLineSegment(sketch, "E490", {"start": v(-4.23, 4.86) * mm, "end": v(-4.24, 4.86) * mm});
            skLineSegment(sketch, "E491", {"start": v(-4.24, 4.86) * mm, "end": v(-4.26, 4.9) * mm});
            skLineSegment(sketch, "E492", {"start": v(-4.26, 4.9) * mm, "end": v(-4.26, 4.91) * mm});
            skLineSegment(sketch, "E493", {"start": v(-4.26, 4.91) * mm, "end": v(-4.25, 4.92) * mm});
            skLineSegment(sketch, "E494", {"start": v(-4.25, 4.92) * mm, "end": v(-4.19, 4.97) * mm});
            skLineSegment(sketch, "E495", {"start": v(-4.19, 4.97) * mm, "end": v(-4.12, 5.02) * mm});
            skLineSegment(sketch, "E496", {"start": v(-4.12, 5.02) * mm, "end": v(-4.1, 5.02) * mm});
            skLineSegment(sketch, "E497", {"start": v(-4.1, 5.02) * mm, "end": v(-4.04, 5.05) * mm});
            skLineSegment(sketch, "E498", {"start": v(-4.04, 5.05) * mm, "end": v(-3.38, 5.32) * mm});
            skLineSegment(sketch, "E499", {"start": v(-3.38, 5.32) * mm, "end": v(-3.32, 5.34) * mm});
            skLineSegment(sketch, "E500", {"start": v(-3.32, 5.34) * mm, "end": v(-3.18, 5.39) * mm});
            skLineSegment(sketch, "E501", {"start": v(-3.18, 5.39) * mm, "end": v(-2.75, 5.51) * mm});
            skLineSegment(sketch, "E502", {"start": v(-2.75, 5.51) * mm, "end": v(-2.18, 5.63) * mm});
            skLineSegment(sketch, "E503", {"start": v(-2.18, 5.63) * mm, "end": v(-1.6, 5.7) * mm});
            skLineSegment(sketch, "E504", {"start": v(-1.6, 5.7) * mm, "end": v(-1.16, 5.7) * mm});
            skLineSegment(sketch, "E505", {"start": v(-1.16, 5.7) * mm, "end": v(-1.01, 5.7) * mm});
            skLineSegment(sketch, "E506", {"start": v(-1.01, 5.7) * mm, "end": v(-0.85, 5.69) * mm});
            skLineSegment(sketch, "E507", {"start": v(-0.85, 5.69) * mm, "end": v(-0.37, 5.63) * mm});
            skLineSegment(sketch, "E508", {"start": v(-0.37, 5.63) * mm, "end": v(0.27, 5.51) * mm});
            skLineSegment(sketch, "E509", {"start": v(0.27, 5.51) * mm, "end": v(0.9, 5.34) * mm});
            skLineSegment(sketch, "E510", {"start": v(0.9, 5.34) * mm, "end": v(1.36, 5.18) * mm});
            skLineSegment(sketch, "E511", {"start": v(1.36, 5.18) * mm, "end": v(1.5, 5.13) * mm});
            skLineSegment(sketch, "E512", {"start": v(1.5, 5.13) * mm, "end": v(1.56, 5.1) * mm});
            skLineSegment(sketch, "E513", {"start": v(1.56, 5.1) * mm, "end": v(2.06, 4.93) * mm});
            skLineSegment(sketch, "E514", {"start": v(2.06, 4.93) * mm, "end": v(2.12, 4.9) * mm});
            skLineSegment(sketch, "E515", {"start": v(2.12, 4.9) * mm, "end": v(2.14, 4.99) * mm});
            skLineSegment(sketch, "E516", {"start": v(2.14, 4.99) * mm, "end": v(2.11, 5.25) * mm});
            skLineSegment(sketch, "E517", {"start": v(2.11, 5.25) * mm, "end": v(1.97, 5.57) * mm});
            skLineSegment(sketch, "E518", {"start": v(1.97, 5.57) * mm, "end": v(1.72, 5.85) * mm});
            skLineSegment(sketch, "E519", {"start": v(1.72, 5.85) * mm, "end": v(1.47, 6.02) * mm});
            skLineSegment(sketch, "E520", {"start": v(1.47, 6.02) * mm, "end": v(1.39, 6.05) * mm});
            skLineSegment(sketch, "E521", {"start": v(1.39, 6.05) * mm, "end": v(1.3, 6.1) * mm});
            skLineSegment(sketch, "E522", {"start": v(1.3, 6.1) * mm, "end": v(0.83, 6.26) * mm});
            skLineSegment(sketch, "E523", {"start": v(0.83, 6.26) * mm, "end": v(0.35, 6.38) * mm});
            skLineSegment(sketch, "E524", {"start": v(0.35, 6.38) * mm, "end": v(0.3, 6.4) * mm});
            skLineSegment(sketch, "E525", {"start": v(-1.34, 6.54) * mm, "end": v(-1.54, 6.54) * mm});
            skLineSegment(sketch, "E526", {"start": v(-1.54, 6.54) * mm, "end": v(-2.68, 6.47) * mm});
            skLineSegment(sketch, "E527", {"start": v(-3.8, 6.3) * mm, "end": v(-4.04, 6.27) * mm});
            skLineSegment(sketch, "E528", {"start": v(-4.04, 6.27) * mm, "end": v(-4.1, 6.25) * mm});
            skLineSegment(sketch, "E529", {"start": v(-4.1, 6.25) * mm, "end": v(-4.3, 6.2) * mm});
            skLineSegment(sketch, "E530", {"start": v(-4.3, 6.2) * mm, "end": v(-4.58, 6.14) * mm});
            skLineSegment(sketch, "E531", {"start": v(-4.58, 6.14) * mm, "end": v(-4.83, 6.03) * mm});
            skLineSegment(sketch, "E532", {"start": v(-4.83, 6.03) * mm, "end": v(-5.01, 5.9) * mm});
            skLineSegment(sketch, "E533", {"start": v(-5.01, 5.9) * mm, "end": v(-5.06, 5.86) * mm});
            skLineSegment(sketch, "E534", {"start": v(-5.06, 5.86) * mm, "end": v(-5.1, 5.82) * mm});
            skLineSegment(sketch, "E535", {"start": v(-5.1, 5.82) * mm, "end": v(-5.48, 5.48) * mm});
            skLineSegment(sketch, "E536", {"start": v(-5.48, 5.48) * mm, "end": v(-5.51, 5.45) * mm});
            skLineSegment(sketch, "E537", {"start": v(-5.51, 5.45) * mm, "end": v(-5.53, 5.43) * mm});
            skLineSegment(sketch, "E538", {"start": v(-5.53, 5.43) * mm, "end": v(-5.6, 5.37) * mm});
            skLineSegment(sketch, "E539", {"start": v(-5.6, 5.37) * mm, "end": v(-5.65, 5.3) * mm});
            skLineSegment(sketch, "E540", {"start": v(-5.65, 5.3) * mm, "end": v(-5.68, 5.25) * mm});
            skLineSegment(sketch, "E541", {"start": v(-5.68, 5.25) * mm, "end": v(-5.7, 5.2) * mm});
            skLineSegment(sketch, "E542", {"start": v(-5.7, 5.2) * mm, "end": v(-5.7, 5.14) * mm});
            skLineSegment(sketch, "E543", {"start": v(-5.7, 5.14) * mm, "end": v(-5.68, 5.08) * mm});
            skLineSegment(sketch, "E544", {"start": v(-5.68, 5.08) * mm, "end": v(-5.64, 5) * mm});
            skLineSegment(sketch, "E545", {"start": v(-5.64, 5) * mm, "end": v(-5.6, 4.93) * mm});
            skLineSegment(sketch, "E546", {"start": v(-5.6, 4.93) * mm, "end": v(-5.6, 4.9) * mm});
            skLineSegment(sketch, "E547", {"start": v(-5.6, 4.9) * mm, "end": v(-5.54, 4.8) * mm});
            skLineSegment(sketch, "E548", {"start": v(-5.54, 4.8) * mm, "end": v(-5.04, 3.85) * mm});
            skLineSegment(sketch, "E549", {"start": v(-5.04, 3.85) * mm, "end": v(-4.99, 3.75) * mm});
            skLineSegment(sketch, "E550", {"start": v(-4.99, 3.75) * mm, "end": v(-4.91, 3.61) * mm});
            skLineSegment(sketch, "E551", {"start": v(-4.91, 3.61) * mm, "end": v(-4.19, 2.2) * mm});
            skLineSegment(sketch, "E552", {"start": v(-4.19, 2.2) * mm, "end": v(-4.12, 2.06) * mm});
            skLineSegment(sketch, "E553", {"start": v(-8.54, 3.1) * mm, "end": v(-8.55, 3.09) * mm});
            skLineSegment(sketch, "E554", {"start": v(-8.55, 3.09) * mm, "end": v(-8.95, 2.5) * mm});
            skLineSegment(sketch, "E555", {"start": v(-8.38, 0.5) * mm, "end": v(-8.34, 0.47) * mm});
            skLineSegment(sketch, "E556", {"start": v(-8.34, 0.47) * mm, "end": v(-7.7, 0.07) * mm});
            skLineSegment(sketch, "E557", {"start": v(-7.7, 0.07) * mm, "end": v(-7.64, 0.03) * mm});
            skLineSegment(sketch, "E558", {"start": v(-7.64, 0.03) * mm, "end": v(-7.61, 0.01) * mm});
            skLineSegment(sketch, "E559", {"start": v(-7.61, 0.01) * mm, "end": v(-7.37, -0.16) * mm});
            skLineSegment(sketch, "E560", {"start": v(-7.37, -0.16) * mm, "end": v(-7.34, -0.18) * mm});
            skLineSegment(sketch, "E561", {"start": v(-7.34, -0.18) * mm, "end": v(-7.35, -0.19) * mm});
            skLineSegment(sketch, "E562", {"start": v(-7.35, -0.19) * mm, "end": v(-7.37, -0.25) * mm});
            skLineSegment(sketch, "E563", {"start": v(-7.37, -0.25) * mm, "end": v(-7.37, -0.25) * mm});
            skLineSegment(sketch, "E564", {"start": v(-7.37, -0.25) * mm, "end": v(-7.4, -0.25) * mm});
            skLineSegment(sketch, "E565", {"start": v(-7.4, -0.25) * mm, "end": v(-7.49, -0.25) * mm});
            skLineSegment(sketch, "E566", {"start": v(-7.49, -0.25) * mm, "end": v(-7.58, -0.24) * mm});
            skLineSegment(sketch, "E567", {"start": v(-7.58, -0.24) * mm, "end": v(-7.6, -0.23) * mm});
            skLineSegment(sketch, "E568", {"start": v(-7.6, -0.23) * mm, "end": v(-7.72, -0.2) * mm});
            skLineSegment(sketch, "E569", {"start": v(-7.72, -0.2) * mm, "end": v(-8.3, -0.02) * mm});
            skLineSegment(sketch, "E570", {"start": v(-8.3, -0.02) * mm, "end": v(-8.83, 0.23) * mm});
            skLineSegment(sketch, "E571", {"start": v(-8.83, 0.23) * mm, "end": v(-8.9, 0.27) * mm});
            skLineSegment(sketch, "E572", {"start": v(-10.16, 2.27) * mm, "end": v(-10.06, 2.83) * mm});
            skLineSegment(sketch, "E573", {"start": v(-10.06, 2.83) * mm, "end": v(-9.82, 3.5) * mm});
            skLineSegment(sketch, "E574", {"start": v(-9.82, 3.5) * mm, "end": v(-9.44, 4.1) * mm});
            skLineSegment(sketch, "E575", {"start": v(-9.44, 4.1) * mm, "end": v(-9.07, 4.5) * mm});
            skLineSegment(sketch, "E576", {"start": v(-9.07, 4.5) * mm, "end": v(-8.96, 4.59) * mm});
            skLineSegment(sketch, "E577", {"start": v(-8.07, 6.31) * mm, "end": v(-8.06, 6.33) * mm});
            skLineSegment(sketch, "E578", {"start": v(-8.06, 6.33) * mm, "end": v(-7.73, 6.9) * mm});
            skLineSegment(sketch, "E579", {"start": v(-7.73, 6.9) * mm, "end": v(-7.7, 6.95) * mm});
            skLineSegment(sketch, "E580", {"start": v(-7.7, 6.95) * mm, "end": v(-7.65, 7.05) * mm});
            skLineSegment(sketch, "E581", {"start": v(-7.65, 7.05) * mm, "end": v(-7.44, 7.32) * mm});
            skLineSegment(sketch, "E582", {"start": v(-7.44, 7.32) * mm, "end": v(-7.14, 7.63) * mm});
            skLineSegment(sketch, "E583", {"start": v(-7.14, 7.63) * mm, "end": v(-6.8, 7.91) * mm});
            skLineSegment(sketch, "E584", {"start": v(-6.8, 7.91) * mm, "end": v(-6.53, 8.11) * mm});
            skLineSegment(sketch, "E585", {"start": v(-6.53, 8.11) * mm, "end": v(-6.45, 8.18) * mm});
            skLineSegment(sketch, "E586", {"start": v(-6.45, 8.18) * mm, "end": v(-6.36, 8.24) * mm});
            skLineSegment(sketch, "E587", {"start": v(-6.36, 8.24) * mm, "end": v(-5.5, 8.85) * mm});
            skLineSegment(sketch, "E588", {"start": v(-5.5, 8.85) * mm, "end": v(-5.42, 8.91) * mm});
            skLineSegment(sketch, "E589", {"start": v(-5.42, 8.91) * mm, "end": v(-5.4, 8.92) * mm});
            skLineSegment(sketch, "E590", {"start": v(-5.4, 8.92) * mm, "end": v(-5.3, 8.98) * mm});
            skLineSegment(sketch, "E591", {"start": v(-5.3, 8.98) * mm, "end": v(-5.25, 9) * mm});
            skLineSegment(sketch, "E592", {"start": v(-5.25, 9) * mm, "end": v(-5.25, 9) * mm});
            skLineSegment(sketch, "E593", {"start": v(-5.25, 9) * mm, "end": v(-5.22, 8.96) * mm});
            skLineSegment(sketch, "E594", {"start": v(-5.22, 8.96) * mm, "end": v(-5.21, 8.95) * mm});
            skLineSegment(sketch, "E595", {"start": v(-5.21, 8.95) * mm, "end": v(-5.23, 8.94) * mm});
            skLineSegment(sketch, "E596", {"start": v(-5.23, 8.94) * mm, "end": v(-5.38, 8.8) * mm});
            skLineSegment(sketch, "E597", {"start": v(-5.38, 8.8) * mm, "end": v(-5.4, 8.78) * mm});
            skLineSegment(sketch, "E598", {"start": v(-5.4, 8.78) * mm, "end": v(-5.5, 8.69) * mm});
            skLineSegment(sketch, "E599", {"start": v(-5.5, 8.69) * mm, "end": v(-6, 8.2) * mm});
            skLineSegment(sketch, "E600", {"start": v(-6, 8.2) * mm, "end": v(-6.51, 7.7) * mm});
            skLineSegment(sketch, "E601", {"start": v(-6.51, 7.7) * mm, "end": v(-6.6, 7.59) * mm});
            skLineSegment(sketch, "E602", {"start": v(-6.6, 7.59) * mm, "end": v(-6.67, 7.51) * mm});
            skLineSegment(sketch, "E603", {"start": v(-6.67, 7.51) * mm, "end": v(-6.83, 7.26) * mm});
            skLineSegment(sketch, "E604", {"start": v(-6.83, 7.26) * mm, "end": v(-6.95, 6.9) * mm});
            skLineSegment(sketch, "E605", {"start": v(-6.95, 6.9) * mm, "end": v(-6.99, 6.52) * mm});
            skLineSegment(sketch, "E606", {"start": v(-6.99, 6.52) * mm, "end": v(-6.97, 6.23) * mm});
            skLineSegment(sketch, "E607", {"start": v(-6.97, 6.23) * mm, "end": v(-6.95, 6.13) * mm});
            skLineSegment(sketch, "E608", {"start": v(-6.95, 6.13) * mm, "end": v(-6.94, 6.07) * mm});
            skLineSegment(sketch, "E609", {"start": v(-6.94, 6.07) * mm, "end": v(-6.86, 5.92) * mm});
            skLineSegment(sketch, "E610", {"start": v(-6.86, 5.92) * mm, "end": v(-6.67, 5.76) * mm});
            skLineSegment(sketch, "E611", {"start": v(-6.67, 5.76) * mm, "end": v(-6.44, 5.67) * mm});
            skLineSegment(sketch, "E612", {"start": v(-6.44, 5.67) * mm, "end": v(-6.26, 5.67) * mm});
            skLineSegment(sketch, "E613", {"start": v(-6.26, 5.67) * mm, "end": v(-6.2, 5.68) * mm});
            skLineSegment(sketch, "E614", {"start": v(-6.2, 5.68) * mm, "end": v(-6.13, 5.7) * mm});
            skLineSegment(sketch, "E615", {"start": v(-6.13, 5.7) * mm, "end": v(-5.8, 5.9) * mm});
            skLineSegment(sketch, "E616", {"start": v(-5.8, 5.9) * mm, "end": v(-5.52, 6.17) * mm});
            skLineSegment(sketch, "E617", {"start": v(-5.52, 6.17) * mm, "end": v(-5.47, 6.24) * mm});
            skLineSegment(sketch, "E618", {"start": v(-5.47, 6.24) * mm, "end": v(-5.44, 6.29) * mm});
            skLineSegment(sketch, "E619", {"start": v(-5.44, 6.29) * mm, "end": v(-5.39, 6.46) * mm});
            skLineSegment(sketch, "E620", {"start": v(-5.39, 6.46) * mm, "end": v(-5.41, 6.64) * mm});
            skLineSegment(sketch, "E621", {"start": v(-5.41, 6.64) * mm, "end": v(-5.53, 6.78) * mm});
            skLineSegment(sketch, "E622", {"start": v(-5.53, 6.78) * mm, "end": v(-5.7, 6.85) * mm});
            skLineSegment(sketch, "E623", {"start": v(-5.7, 6.85) * mm, "end": v(-5.75, 6.85) * mm});
            skLineSegment(sketch, "E624", {"start": v(-5.75, 6.85) * mm, "end": v(-5.81, 6.86) * mm});
            skLineSegment(sketch, "E625", {"start": v(-5.81, 6.86) * mm, "end": v(-6.13, 6.88) * mm});
            skLineSegment(sketch, "E626", {"start": v(-6.13, 6.88) * mm, "end": v(-6.46, 6.89) * mm});
            skLineSegment(sketch, "E627", {"start": v(-6.46, 6.89) * mm, "end": v(-6.53, 6.9) * mm});
            skLineSegment(sketch, "E628", {"start": v(-6.53, 6.9) * mm, "end": v(-6.48, 6.91) * mm});
            skLineSegment(sketch, "E629", {"start": v(-6.48, 6.91) * mm, "end": v(-5.98, 7.1) * mm});
            skLineSegment(sketch, "E630", {"start": v(-5.98, 7.1) * mm, "end": v(-5.93, 7.12) * mm});
            skLineSegment(sketch, "E631", {"start": v(-5.93, 7.12) * mm, "end": v(-5.7, 7.2) * mm});
            skLineSegment(sketch, "E632", {"start": v(-5.7, 7.2) * mm, "end": v(-4.52, 7.6) * mm});
            skLineSegment(sketch, "E633", {"start": v(-3.34, 7.97) * mm, "end": v(-3.1, 8.04) * mm});
            skLineSegment(sketch, "E634", {"start": v(-3.1, 8.04) * mm, "end": v(-2.86, 8.1) * mm});
            skLineSegment(sketch, "E635", {"start": v(-2.86, 8.1) * mm, "end": v(-2.11, 8.26) * mm});
            skLineSegment(sketch, "E636", {"start": v(-2.11, 8.26) * mm, "end": v(-1.11, 8.37) * mm});
            skLineSegment(sketch, "E637", {"start": v(-1.11, 8.37) * mm, "end": v(-0.1, 8.38) * mm});
            skLineSegment(sketch, "E638", {"start": v(-0.1, 8.38) * mm, "end": v(0.65, 8.32) * mm});
            skLineSegment(sketch, "E639", {"start": v(0.65, 8.32) * mm, "end": v(0.9, 8.29) * mm});
            skLineSegment(sketch, "E640", {"start": v(3.7, 5.59) * mm, "end": v(3.66, 5.4) * mm});
            skLineSegment(sketch, "E641", {"start": v(3.66, 5.4) * mm, "end": v(3.43, 4.3) * mm});
            skLineSegment(sketch, "E642", {"start": v(3.43, 4.3) * mm, "end": v(3.08, 3.21) * mm});
            skLineSegment(sketch, "E643", {"start": v(3.08, 3.21) * mm, "end": v(2.99, 3) * mm});
            skLineSegment(sketch, "E644", {"start": v(2.99, 3) * mm, "end": v(2.88, 2.75) * mm});
            skLineSegment(sketch, "E645", {"start": v(2.88, 2.75) * mm, "end": v(2.5, 2) * mm});
            skLineSegment(sketch, "E646", {"start": v(2.5, 2) * mm, "end": v(1.95, 1.05) * mm});
            skLineSegment(sketch, "E647", {"start": v(1.95, 1.05) * mm, "end": v(1.34, 0.13) * mm});
            skLineSegment(sketch, "E648", {"start": v(1.34, 0.13) * mm, "end": v(0.86, -0.55) * mm});
            skLineSegment(sketch, "E649", {"start": v(0.86, -0.55) * mm, "end": v(0.7, -0.77) * mm});
            skLineSegment(sketch, "E650", {"start": v(0.7, -0.77) * mm, "end": v(0.6, -0.91) * mm});
            skLineSegment(sketch, "E651", {"start": v(0.6, -0.91) * mm, "end": v(-0.41, -2.32) * mm});
            skLineSegment(sketch, "E652", {"start": v(-0.41, -2.32) * mm, "end": v(-0.51, -2.46) * mm});
            skLineSegment(sketch, "E653", {"start": v(-0.51, -2.46) * mm, "end": v(-0.52, -2.47) * mm});
            skLineSegment(sketch, "E654", {"start": v(-0.52, -2.47) * mm, "end": v(-0.56, -2.53) * mm});
            skLineSegment(sketch, "E655", {"start": v(-0.56, -2.53) * mm, "end": v(-0.62, -2.62) * mm});
            skLineSegment(sketch, "E656", {"start": v(-0.62, -2.62) * mm, "end": v(-0.63, -2.64) * mm});
            skLineSegment(sketch, "E657", {"start": v(-0.63, -2.64) * mm, "end": v(-0.58, -2.64) * mm});
            skLineSegment(sketch, "E658", {"start": v(-0.58, -2.64) * mm, "end": v(-0.36, -2.65) * mm});
            skLineSegment(sketch, "E659", {"start": v(-0.36, -2.65) * mm, "end": v(-0.16, -2.64) * mm});
            skLineSegment(sketch, "E660", {"start": v(-0.16, -2.64) * mm, "end": v(-0.12, -2.63) * mm});
            skLineSegment(sketch, "E661", {"start": v(-0.12, -2.63) * mm, "end": v(0.07, -2.6) * mm});
            skLineSegment(sketch, "E662", {"start": v(0.07, -2.6) * mm, "end": v(2.02, -2.23) * mm});
            skLineSegment(sketch, "E663", {"start": v(2.02, -2.23) * mm, "end": v(2.22, -2.18) * mm});
            skLineSegment(sketch, "E664", {"start": v(2.22, -2.18) * mm, "end": v(2.59, -2.1) * mm});
            skLineSegment(sketch, "E665", {"start": v(2.59, -2.1) * mm, "end": v(6.32, -1.25) * mm});
            skLineSegment(sketch, "E666", {"start": v(6.32, -1.25) * mm, "end": v(6.7, -1.16) * mm});
            skLineSegment(sketch, "E667", {"start": v(10.1, 1.04) * mm, "end": v(10.11, 1.09) * mm});
            skLineSegment(sketch, "E668", {"start": v(10.11, 1.09) * mm, "end": v(10.11, 1.1) * mm});
            skLineSegment(sketch, "E669", {"start": v(10.11, 1.1) * mm, "end": v(10.14, 1.2) * mm});
            skLineSegment(sketch, "E670", {"start": v(10.14, 1.2) * mm, "end": v(10.19, 1.56) * mm});
            skLineSegment(sketch, "E671", {"start": v(10.19, 1.56) * mm, "end": v(10.2, 2.02) * mm});
            skLineSegment(sketch, "E672", {"start": v(10.2, 2.02) * mm, "end": v(10.13, 2.47) * mm});
            skLineSegment(sketch, "E673", {"start": v(10.13, 2.47) * mm, "end": v(10.04, 2.8) * mm});
            skLineSegment(sketch, "E674", {"start": v(10.04, 2.8) * mm, "end": v(10, 2.92) * mm});
            skLineSegment(sketch, "E675", {"start": v(10, 2.92) * mm, "end": v(9.97, 3) * mm});
            skLineSegment(sketch, "E676", {"start": v(9.97, 3) * mm, "end": v(9.66, 3.9) * mm});
            skLineSegment(sketch, "E677", {"start": v(9.66, 3.9) * mm, "end": v(9.63, 4) * mm});
            skLineSegment(sketch, "E678", {"start": v(9.63, 4) * mm, "end": v(9.62, 4) * mm});
            skLineSegment(sketch, "E679", {"start": v(9.62, 4) * mm, "end": v(9.63, 4.08) * mm});
            skLineSegment(sketch, "E680", {"start": v(9.63, 4.08) * mm, "end": v(9.65, 4.15) * mm});
            skLineSegment(sketch, "E681", {"start": v(9.65, 4.15) * mm, "end": v(9.65, 4.17) * mm});
            skLineSegment(sketch, "E682", {"start": v(9.65, 4.17) * mm, "end": v(9.66, 4.16) * mm});
            skLineSegment(sketch, "E683", {"start": v(9.66, 4.16) * mm, "end": v(9.74, 4.13) * mm});
            skLineSegment(sketch, "E684", {"start": v(9.74, 4.13) * mm, "end": v(9.8, 4.1) * mm});
            skLineSegment(sketch, "E685", {"start": v(9.8, 4.1) * mm, "end": v(9.81, 4.09) * mm});
            skLineSegment(sketch, "E686", {"start": v(9.81, 4.09) * mm, "end": v(9.85, 4.03) * mm});
            skLineSegment(sketch, "E687", {"start": v(9.85, 4.03) * mm, "end": v(10.25, 3.41) * mm});
            skLineSegment(sketch, "E688", {"start": v(10.25, 3.41) * mm, "end": v(10.28, 3.35) * mm});
            skLineSegment(sketch, "E689", {"start": v(10.28, 3.35) * mm, "end": v(10.36, 3.2) * mm});
            skLineSegment(sketch, "E690", {"start": v(10.36, 3.2) * mm, "end": v(10.68, 2.41) * mm});
            skLineSegment(sketch, "E691", {"start": v(10.68, 2.41) * mm, "end": v(10.9, 1.6) * mm});
            skLineSegment(sketch, "E692", {"start": v(10.9, 1.6) * mm, "end": v(10.92, 1.46) * mm});
            skLineSegment(sketch, "E693", {"start": v(10.9, 0.2) * mm, "end": v(10.9, 0.2) * mm});
            skLineSegment(sketch, "E694", {"start": v(10.9, 0.2) * mm, "end": v(10.86, -0.06) * mm});
            skLineSegment(sketch, "E695", {"start": v(10.86, -0.06) * mm, "end": v(10.86, -0.09) * mm});
            skLineSegment(sketch, "E696", {"start": v(10.86, -0.09) * mm, "end": v(10.97, -0.07) * mm});
            skLineSegment(sketch, "E697", {"start": v(10.97, -0.07) * mm, "end": v(11.56, 0) * mm});
            skLineSegment(sketch, "E698", {"start": v(11.56, 0) * mm, "end": v(12.14, 0.06) * mm});
            skLineSegment(sketch, "E699", {"start": v(13.23, 0.1) * mm, "end": v(14.05, 0.08) * mm});
            skLineSegment(sketch, "E700", {"start": v(14.05, 0.08) * mm, "end": v(14.2, 0.07) * mm});
            skLineSegment(sketch, "E701", {"start": v(14.3, 0.06) * mm, "end": v(14.37, 0.05) * mm});
            skLineSegment(sketch, "E702", {"start": v(14.37, 0.05) * mm, "end": v(15.17, -0.1) * mm});
            skLineSegment(sketch, "E703", {"start": v(15.17, -0.1) * mm, "end": v(15.25, -0.13) * mm});
            skLineSegment(sketch, "E704", {"start": v(15.25, -0.13) * mm, "end": v(15.32, -0.14) * mm});
            skLineSegment(sketch, "E705", {"start": v(15.32, -0.14) * mm, "end": v(15.66, -0.27) * mm});
            skLineSegment(sketch, "E706", {"start": v(15.66, -0.27) * mm, "end": v(15.98, -0.42) * mm});
            skLineSegment(sketch, "E707", {"start": v(15.98, -0.42) * mm, "end": v(16.04, -0.46) * mm});
            skLineSegment(sketch, "E708", {"start": v(16.04, -0.46) * mm, "end": v(16.08, -0.48) * mm});
            skLineSegment(sketch, "E709", {"start": v(16.08, -0.48) * mm, "end": v(16.18, -0.55) * mm});
            skLineSegment(sketch, "E710", {"start": v(16.18, -0.55) * mm, "end": v(16.3, -0.67) * mm});
            skLineSegment(sketch, "E711", {"start": v(16.3, -0.67) * mm, "end": v(16.37, -0.82) * mm});
            skLineSegment(sketch, "E712", {"start": v(16.37, -0.82) * mm, "end": v(16.4, -0.96) * mm});
            skLineSegment(sketch, "E713", {"start": v(16.4, -0.96) * mm, "end": v(16.4, -1) * mm});
            skLineSegment(sketch, "E714", {"start": v(16.4, -1) * mm, "end": v(16.28, -0.94) * mm});
            skLineSegment(sketch, "E715", {"start": v(16.28, -0.94) * mm, "end": v(15.9, -0.77) * mm});
            skLineSegment(sketch, "E716", {"start": v(15.9, -0.77) * mm, "end": v(15.4, -0.61) * mm});
            skLineSegment(sketch, "E717", {"start": v(15.4, -0.61) * mm, "end": v(14.88, -0.51) * mm});
            skLineSegment(sketch, "E718", {"start": v(14.88, -0.51) * mm, "end": v(14.37, -0.47) * mm});
            skLineSegment(sketch, "E719", {"start": v(14.37, -0.47) * mm, "end": v(13.86, -0.47) * mm});
            skLineSegment(sketch, "E720", {"start": v(13.86, -0.47) * mm, "end": v(13.34, -0.53) * mm});
            skLineSegment(sketch, "E721", {"start": v(12.3, -0.74) * mm, "end": v(11.94, -0.84) * mm});
            skLineSegment(sketch, "E722", {"start": v(11.94, -0.84) * mm, "end": v(8.23, -1.86) * mm});
            skLineSegment(sketch, "E723", {"start": v(8.23, -1.86) * mm, "end": v(7.9, -1.96) * mm});
            skLineSegment(sketch, "E724", {"start": v(3.9, -3.04) * mm, "end": v(3.56, -3.13) * mm});
            skLineSegment(sketch, "E725", {"start": v(3.56, -3.13) * mm, "end": v(-0.04, -4.07) * mm});
            skLineSegment(sketch, "E726", {"start": v(-0.04, -4.07) * mm, "end": v(-0.4, -4.17) * mm});
            skLineSegment(sketch, "E727", {"start": v(-0.4, -4.17) * mm, "end": v(-0.43, -4.18) * mm});
            skLineSegment(sketch, "E728", {"start": v(-0.43, -4.18) * mm, "end": v(-0.53, -4.2) * mm});
            skLineSegment(sketch, "E729", {"start": v(-0.53, -4.2) * mm, "end": v(-0.62, -4.23) * mm});
            skLineSegment(sketch, "E730", {"start": v(-0.62, -4.23) * mm, "end": v(-0.68, -4.25) * mm});
            skLineSegment(sketch, "E731", {"start": v(-0.68, -4.25) * mm, "end": v(-0.7, -4.29) * mm});
            skLineSegment(sketch, "E732", {"start": v(-0.7, -4.29) * mm, "end": v(-0.7, -4.33) * mm});
            skLineSegment(sketch, "E733", {"start": v(-0.7, -4.33) * mm, "end": v(-0.67, -4.38) * mm});
            skLineSegment(sketch, "E734", {"start": v(-0.67, -4.38) * mm, "end": v(-0.61, -4.46) * mm});
            skLineSegment(sketch, "E735", {"start": v(-0.61, -4.46) * mm, "end": v(-0.55, -4.54) * mm});
            skLineSegment(sketch, "E736", {"start": v(-0.55, -4.54) * mm, "end": v(-0.53, -4.57) * mm});
            skLineSegment(sketch, "E737", {"start": v(-0.53, -4.57) * mm, "end": v(-0.5, -4.6) * mm});
            skLineSegment(sketch, "E738", {"start": v(-0.5, -4.6) * mm, "end": v(-0.4, -4.78) * mm});
            skLineSegment(sketch, "E739", {"start": v(-0.32, -4.98) * mm, "end": v(-0.3, -5.02) * mm});
            skLineSegment(sketch, "E740", {"start": v(-0.3, -5.02) * mm, "end": v(-0.25, -5.2) * mm});
            skLineSegment(sketch, "E741", {"start": v(-0.25, -5.2) * mm, "end": v(-0.15, -5.76) * mm});
            skLineSegment(sketch, "E742", {"start": v(-0.15, -5.76) * mm, "end": v(-0.21, -6.45) * mm});
            skLineSegment(sketch, "E743", {"start": v(-0.21, -6.45) * mm, "end": v(-0.48, -7.09) * mm});
            skLineSegment(sketch, "E744", {"start": v(-0.48, -7.09) * mm, "end": v(-0.82, -7.54) * mm});
            skLineSegment(sketch, "E745", {"start": v(-0.82, -7.54) * mm, "end": v(-0.95, -7.67) * mm});
            skLineSegment(sketch, "E746", {"start": v(-0.95, -7.67) * mm, "end": v(-1.07, -7.8) * mm});
            skLineSegment(sketch, "E747", {"start": v(-1.07, -7.8) * mm, "end": v(-1.46, -8.13) * mm});
            skLineSegment(sketch, "E748", {"start": v(-1.46, -8.13) * mm, "end": v(-2, -8.54) * mm});
            skLineSegment(sketch, "E749", {"start": v(-2, -8.54) * mm, "end": v(-2.6, -8.87) * mm});
            skLineSegment(sketch, "E750", {"start": v(-2.6, -8.87) * mm, "end": v(-3.07, -9.07) * mm});
            skLineSegment(sketch, "E751", {"start": v(-3.07, -9.07) * mm, "end": v(-3.24, -9.12) * mm});
            skLineSegment(sketch, "E752", {"start": v(-3.24, -9.12) * mm, "end": v(-3.24, -9.13) * mm});
            skLineSegment(sketch, "E753", {"start": v(-3.24, -9.13) * mm, "end": v(-3.3, -9.14) * mm});
            skLineSegment(sketch, "E754", {"start": v(-3.3, -9.14) * mm, "end": v(-3.37, -9.15) * mm});
            skLineSegment(sketch, "E755", {"start": v(-3.37, -9.15) * mm, "end": v(-3.39, -9.15) * mm});
            skLineSegment(sketch, "E756", {"start": v(-3.39, -9.15) * mm, "end": v(-3.34, -9.11) * mm});
            skLineSegment(sketch, "E757", {"start": v(-3.34, -9.11) * mm, "end": v(-3.14, -8.95) * mm});
            skLineSegment(sketch, "E758", {"start": v(-3.14, -8.95) * mm, "end": v(-2.95, -8.8) * mm});
            skLineSegment(sketch, "E759", {"start": v(-2.95, -8.8) * mm, "end": v(-2.92, -8.77) * mm});
            skLineSegment(sketch, "E760", {"start": v(-2.92, -8.77) * mm, "end": v(-2.88, -8.74) * mm});
            skLineSegment(sketch, "E761", {"start": v(-2.88, -8.74) * mm, "end": v(-2.54, -8.4) * mm});
            skLineSegment(sketch, "E762", {"start": v(-2.54, -8.4) * mm, "end": v(-2.51, -8.37) * mm});
            skLineSegment(sketch, "E763", {"start": v(-2.51, -8.37) * mm, "end": v(-2.43, -8.28) * mm});
            skLineSegment(sketch, "E764", {"start": v(-2.43, -8.28) * mm, "end": v(-2.2, -8) * mm});
            skLineSegment(sketch, "E765", {"start": v(-2.2, -8) * mm, "end": v(-1.96, -7.58) * mm});
            skLineSegment(sketch, "E766", {"start": v(-1.96, -7.58) * mm, "end": v(-1.77, -7.14) * mm});
            skLineSegment(sketch, "E767", {"start": v(-1.77, -7.14) * mm, "end": v(-1.7, -6.78) * mm});
            skLineSegment(sketch, "E768", {"start": v(-1.7, -6.78) * mm, "end": v(-1.68, -6.66) * mm});
            skLineSegment(sketch, "E769", {"start": v(-1.68, -6.66) * mm, "end": v(-1.67, -6.57) * mm});
            skLineSegment(sketch, "E770", {"start": v(-1.67, -6.57) * mm, "end": v(-1.7, -6.15) * mm});
            skLineSegment(sketch, "E771", {"start": v(-1.7, -6.15) * mm, "end": v(-1.84, -5.75) * mm});
            skLineSegment(sketch, "E772", {"start": v(-1.84, -5.75) * mm, "end": v(-1.89, -5.68) * mm});
            skLineSegment(sketch, "E773", {"start": v(-1.89, -5.68) * mm, "end": v(-1.94, -5.58) * mm});
            skLineSegment(sketch, "E774", {"start": v(-1.94, -5.58) * mm, "end": v(-2.47, -4.66) * mm});
            skLineSegment(sketch, "E775", {"start": v(-2.47, -4.66) * mm, "end": v(-2.52, -4.56) * mm});
            skLineSegment(sketch, "E776", {"start": v(-2.52, -4.56) * mm, "end": v(-2.6, -4.6) * mm});
            skLineSegment(sketch, "E777", {"start": v(-2.6, -4.6) * mm, "end": v(-2.8, -4.72) * mm});
            skLineSegment(sketch, "E778", {"start": v(-2.8, -4.72) * mm, "end": v(-3.03, -4.84) * mm});
            skLineSegment(sketch, "E779", {"start": v(-3.03, -4.84) * mm, "end": v(-3.08, -4.86) * mm});
            skLineSegment(sketch, "E780", {"start": v(-3.08, -4.86) * mm, "end": v(-3.1, -4.86) * mm});
            skLineSegment(sketch, "E781", {"start": v(-3.1, -4.86) * mm, "end": v(-3.23, -4.92) * mm});
            skLineSegment(sketch, "E782", {"start": v(-4.17, -5.19) * mm, "end": v(-4.33, -5.22) * mm});
            skLineSegment(sketch, "E783", {"start": v(-4.33, -5.22) * mm, "end": v(-4.82, -5.26) * mm});
            skLineSegment(sketch, "E784", {"start": v(-4.82, -5.26) * mm, "end": v(-5.47, -5.24) * mm});
            skLineSegment(sketch, "E785", {"start": v(-5.47, -5.24) * mm, "end": v(-6.12, -5.14) * mm});
            skLineSegment(sketch, "E786", {"start": v(-6.12, -5.14) * mm, "end": v(-6.62, -5) * mm});
            skLineSegment(sketch, "E787", {"start": v(-6.62, -5) * mm, "end": v(-6.78, -4.94) * mm});
            skLineSegment(sketch, "E788", {"start": v(-6.78, -4.94) * mm, "end": v(-6.78, -4.94) * mm});
            skLineSegment(sketch, "E789", {"start": v(-6.78, -4.94) * mm, "end": v(-6.85, -4.93) * mm});
            skLineSegment(sketch, "E790", {"start": v(-6.85, -4.93) * mm, "end": v(-6.86, -4.93) * mm});
            skLineSegment(sketch, "E791", {"start": v(-6.86, -4.93) * mm, "end": v(-6.95, -4.75) * mm});
            skLineSegment(sketch, "E792", {"start": v(-6.95, -4.75) * mm, "end": v(-6.89, -4.76) * mm});
            skLineSegment(sketch, "E793", {"start": v(-6.89, -4.76) * mm, "end": v(-6.23, -4.87) * mm});
            skLineSegment(sketch, "E794", {"start": v(-6.23, -4.87) * mm, "end": v(-6.17, -4.88) * mm});
            skLineSegment(sketch, "E795", {"start": v(-6.17, -4.88) * mm, "end": v(-6.11, -4.89) * mm});
            skLineSegment(sketch, "E796", {"start": v(-6.11, -4.89) * mm, "end": v(-5.83, -4.9) * mm});
            skLineSegment(sketch, "E797", {"start": v(-5.83, -4.9) * mm, "end": v(-5.57, -4.9) * mm});
            skLineSegment(sketch, "E798", {"start": v(-5.57, -4.9) * mm, "end": v(-5.52, -4.9) * mm});
            skLineSegment(sketch, "E799", {"start": v(-5.31, -4.87) * mm, "end": v(-5.24, -4.85) * mm});
            skLineSegment(sketch, "E800", {"start": v(-5.24, -4.85) * mm, "end": v(-4.94, -4.76) * mm});
            skLineSegment(sketch, "E801", {"start": v(-4.94, -4.76) * mm, "end": v(-4.55, -4.58) * mm});
            skLineSegment(sketch, "E802", {"start": v(-4.55, -4.58) * mm, "end": v(-4.2, -4.33) * mm});
            skLineSegment(sketch, "E803", {"start": v(-4.2, -4.33) * mm, "end": v(-3.94, -4.1) * mm});
            skLineSegment(sketch, "E804", {"start": v(-3.94, -4.1) * mm, "end": v(-3.86, -4.02) * mm});
            skLineSegment(sketch, "E805", {"start": v(-3.86, -4.02) * mm, "end": v(-3.86, -4.02) * mm});
            skLineSegment(sketch, "E806", {"start": v(-3.86, -4.02) * mm, "end": v(-3.85, -4.01) * mm});
            skLineSegment(sketch, "E807", {"start": v(-3.69, -2.12) * mm, "end": v(-3.77, -1.97) * mm});
            skLineSegment(sketch, "E808", {"start": v(-3.77, -1.97) * mm, "end": v(-4.57, -0.4) * mm});
            skLineSegment(sketch, "E809", {"start": v(-4.57, -0.4) * mm, "end": v(-4.65, -0.25) * mm});
            skLineSegment(sketch, "E810", {"start": v(-4.65, -0.25) * mm, "end": v(-4.69, -0.19) * mm});
            skLineSegment(sketch, "E811", {"start": v(-4.69, -0.19) * mm, "end": v(-5.06, 0.49) * mm});
            skLineSegment(sketch, "E812", {"start": v(-5.06, 0.49) * mm, "end": v(-5.1, 0.55) * mm});
            skLineSegment(sketch, "E813", {"start": v(-6.33, 2.67) * mm, "end": v(-6.34, 2.7) * mm});
            skLineSegment(sketch, "E814", {"start": v(-6.34, 2.7) * mm, "end": v(-6.59, 3.13) * mm});
            skLineSegment(sketch, "E815", {"start": v(-6.59, 3.13) * mm, "end": v(-6.61, 3.17) * mm});
            skLineSegment(sketch, "E816", {"start": v(-6.61, 3.17) * mm, "end": v(-6.64, 3.23) * mm});
            skLineSegment(sketch, "E817", {"start": v(-6.64, 3.23) * mm, "end": v(-6.96, 3.79) * mm});
            skLineSegment(sketch, "E818", {"start": v(-6.96, 3.79) * mm, "end": v(-6.99, 3.85) * mm});
            skLineSegment(sketch, "E819", {"start": v(-6.99, 3.85) * mm, "end": v(-7, 3.88) * mm});
            skLineSegment(sketch, "E820", {"start": v(-7, 3.88) * mm, "end": v(-7.05, 3.95) * mm});
            skLineSegment(sketch, "E821", {"start": v(-7.05, 3.95) * mm, "end": v(-7.13, 4) * mm});
            skLineSegment(sketch, "E822", {"start": v(-7.13, 4) * mm, "end": v(-7.22, 4) * mm});
            skLineSegment(sketch, "E823", {"start": v(-7.22, 4) * mm, "end": v(-7.3, 3.99) * mm});
            skLineSegment(sketch, "E824", {"start": v(-7.3, 3.99) * mm, "end": v(-7.31, 3.98) * mm});
            skLineSegment(sketch, "E825", {"start": v(-7.31, 3.98) * mm, "end": v(-7.34, 3.97) * mm});
            skLineSegment(sketch, "E826", {"start": v(-7.34, 3.97) * mm, "end": v(-7.6, 3.85) * mm});
            skLineSegment(sketch, "E827", {"start": v(6.68, -1.19) * mm, "end": v(6.7, -1.12) * mm});
            skLineSegment(sketch, "E828", {"start": v(6.7, -1.12) * mm, "end": v(6.73, -0.76) * mm});
            skLineSegment(sketch, "E829", {"start": v(6.73, -0.76) * mm, "end": v(6.7, -0.38) * mm});
            skLineSegment(sketch, "E830", {"start": v(6.7, -0.38) * mm, "end": v(6.69, -0.3) * mm});
            skLineSegment(sketch, "E831", {"start": v(6.69, -0.3) * mm, "end": v(6.69, -0.3) * mm});
            skLineSegment(sketch, "E832", {"start": v(6.69, -0.3) * mm, "end": v(6.65, -0.2) * mm});
            skLineSegment(sketch, "E833", {"start": v(6.65, -0.2) * mm, "end": v(6.65, -0.2) * mm});
            skLineSegment(sketch, "E834", {"start": v(6.65, -0.2) * mm, "end": v(6.52, 0.07) * mm});
            skLineSegment(sketch, "E835", {"start": v(6.52, 0.07) * mm, "end": v(6.12, 0.85) * mm});
            skLineSegment(sketch, "E836", {"start": v(5.2, 2.65) * mm, "end": v(5.07, 2.9) * mm});
            skLineSegment(sketch, "E837", {"start": v(5.07, 2.9) * mm, "end": v(5.05, 2.94) * mm});
            skLineSegment(sketch, "E838", {"start": v(5.05, 2.94) * mm, "end": v(4.95, 3.1) * mm});
            skLineSegment(sketch, "E839", {"start": v(4.95, 3.1) * mm, "end": v(4.83, 3.27) * mm});
            skLineSegment(sketch, "E840", {"start": v(4.83, 3.27) * mm, "end": v(4.8, 3.3) * mm});
            skLineSegment(sketch, "E841", {"start": v(4.8, 3.3) * mm, "end": v(4.8, 3.3) * mm});
            skLineSegment(sketch, "E842", {"start": v(4.8, 3.3) * mm, "end": v(4.75, 3.34) * mm});
            skLineSegment(sketch, "E843", {"start": v(4.75, 3.34) * mm, "end": v(4.68, 3.37) * mm});
            skLineSegment(sketch, "E844", {"start": v(4.68, 3.37) * mm, "end": v(4.6, 3.4) * mm});
            skLineSegment(sketch, "E845", {"start": v(4.6, 3.4) * mm, "end": v(4.55, 3.4) * mm});
            skLineSegment(sketch, "E846", {"start": v(4.55, 3.4) * mm, "end": v(4.53, 3.4) * mm});
            skLineSegment(sketch, "E847", {"start": v(4.53, 3.4) * mm, "end": v(4.45, 3.38) * mm});
            skLineSegment(sketch, "E848", {"start": v(4.45, 3.38) * mm, "end": v(4.22, 3.31) * mm});
            skLineSegment(sketch, "E849", {"start": v(4.22, 3.31) * mm, "end": v(3.95, 3.16) * mm});
            skLineSegment(sketch, "E850", {"start": v(3.95, 3.16) * mm, "end": v(3.7, 2.96) * mm});
            skLineSegment(sketch, "E851", {"start": v(3.7, 2.96) * mm, "end": v(3.53, 2.8) * mm});
            skLineSegment(sketch, "E852", {"start": v(3.53, 2.8) * mm, "end": v(3.48, 2.74) * mm});
            skLineSegment(sketch, "E853", {"start": v(3.48, 2.74) * mm, "end": v(3.45, 2.72) * mm});
            skLineSegment(sketch, "E854", {"start": v(3.45, 2.72) * mm, "end": v(3.19, 2.47) * mm});
            skLineSegment(sketch, "E855", {"start": v(3.19, 2.47) * mm, "end": v(3.16, 2.44) * mm});
            skLineSegment(sketch, "E856", {"start": v(3.16, 2.44) * mm, "end": v(3.15, 2.48) * mm});
            skLineSegment(sketch, "E857", {"start": v(3.15, 2.48) * mm, "end": v(3.17, 2.6) * mm});
            skLineSegment(sketch, "E858", {"start": v(3.17, 2.6) * mm, "end": v(3.24, 2.8) * mm});
            skLineSegment(sketch, "E859", {"start": v(3.24, 2.8) * mm, "end": v(3.36, 3.04) * mm});
            skLineSegment(sketch, "E860", {"start": v(3.36, 3.04) * mm, "end": v(3.52, 3.3) * mm});
            skLineSegment(sketch, "E861", {"start": v(3.52, 3.3) * mm, "end": v(3.72, 3.55) * mm});
            skLineSegment(sketch, "E862", {"start": v(3.72, 3.55) * mm, "end": v(3.94, 3.8) * mm});
            skLineSegment(sketch, "E863", {"start": v(3.94, 3.8) * mm, "end": v(4.18, 4.02) * mm});
            skLineSegment(sketch, "E864", {"start": v(4.18, 4.02) * mm, "end": v(4.36, 4.17) * mm});
            skLineSegment(sketch, "E865", {"start": v(4.36, 4.17) * mm, "end": v(4.42, 4.21) * mm});
            skLineSegment(sketch, "E866", {"start": v(4.42, 4.21) * mm, "end": v(4.3, 4.46) * mm});
            skLineSegment(sketch, "E867", {"start": v(4.3, 4.46) * mm, "end": v(3.94, 5.13) * mm});
            skLineSegment(sketch, "E868", {"start": v(3.94, 5.13) * mm, "end": v(3.9, 5.21) * mm});
            skLineSegment(sketch, "E869", {"start": v(3.9, 5.21) * mm, "end": v(3.88, 5.25) * mm});
            skLineSegment(sketch, "E870", {"start": v(3.88, 5.25) * mm, "end": v(3.7, 5.57) * mm});
            skLineSegment(sketch, "E871", {"start": v(3.7, 5.57) * mm, "end": v(3.7, 5.59) * mm});
            skLineSegment(sketch, "E872", {"start": v(7.9, -1.96) * mm, "end": v(7.89, -1.97) * mm});
            skLineSegment(sketch, "E873", {"start": v(7.89, -1.97) * mm, "end": v(7.89, -1.97) * mm});
            skLineSegment(sketch, "E874", {"start": v(7.89, -1.97) * mm, "end": v(7.84, -2.04) * mm});
            skLineSegment(sketch, "E875", {"start": v(7.84, -2.04) * mm, "end": v(7.57, -2.34) * mm});
            skLineSegment(sketch, "E876", {"start": v(7.57, -2.34) * mm, "end": v(7.25, -2.6) * mm});
            skLineSegment(sketch, "E877", {"start": v(7.25, -2.6) * mm, "end": v(7.18, -2.63) * mm});
            skLineSegment(sketch, "E878", {"start": v(7.18, -2.63) * mm, "end": v(7.06, -2.7) * mm});
            skLineSegment(sketch, "E879", {"start": v(7.06, -2.7) * mm, "end": v(6.45, -3) * mm});
            skLineSegment(sketch, "E880", {"start": v(6.45, -3) * mm, "end": v(5.83, -3.27) * mm});
            skLineSegment(sketch, "E881", {"start": v(5.83, -3.27) * mm, "end": v(5.7, -3.3) * mm});
            skLineSegment(sketch, "E882", {"start": v(5.7, -3.3) * mm, "end": v(5.58, -3.34) * mm});
            skLineSegment(sketch, "E883", {"start": v(5.58, -3.34) * mm, "end": v(5.22, -3.4) * mm});
            skLineSegment(sketch, "E884", {"start": v(5.22, -3.4) * mm, "end": v(4.76, -3.37) * mm});
            skLineSegment(sketch, "E885", {"start": v(4.76, -3.37) * mm, "end": v(4.3, -3.25) * mm});
            skLineSegment(sketch, "E886", {"start": v(4.3, -3.25) * mm, "end": v(3.97, -3.09) * mm});
            skLineSegment(sketch, "E887", {"start": v(3.97, -3.09) * mm, "end": v(3.9, -3.04) * mm});
            skLineSegment(sketch, "E888", {"start": v(14.2, 0.07) * mm, "end": v(14.22, 0.09) * mm});
            skLineSegment(sketch, "E889", {"start": v(14.22, 0.09) * mm, "end": v(14.22, 0.09) * mm});
            skLineSegment(sketch, "E890", {"start": v(14.22, 0.09) * mm, "end": v(14.26, 0.12) * mm});
            skLineSegment(sketch, "E891", {"start": v(14.26, 0.12) * mm, "end": v(14.36, 0.24) * mm});
            skLineSegment(sketch, "E892", {"start": v(14.36, 0.24) * mm, "end": v(14.47, 0.42) * mm});
            skLineSegment(sketch, "E893", {"start": v(14.47, 0.42) * mm, "end": v(14.56, 0.61) * mm});
            skLineSegment(sketch, "E894", {"start": v(14.56, 0.61) * mm, "end": v(14.62, 0.82) * mm});
            skLineSegment(sketch, "E895", {"start": v(14.62, 0.82) * mm, "end": v(14.65, 1.03) * mm});
            skLineSegment(sketch, "E896", {"start": v(14.65, 1.03) * mm, "end": v(14.64, 1.23) * mm});
            skLineSegment(sketch, "E897", {"start": v(14.64, 1.23) * mm, "end": v(14.6, 1.43) * mm});
            skLineSegment(sketch, "E898", {"start": v(14.6, 1.43) * mm, "end": v(14.56, 1.56) * mm});
            skLineSegment(sketch, "E899", {"start": v(14.56, 1.56) * mm, "end": v(14.54, 1.6) * mm});
            skLineSegment(sketch, "E900", {"start": v(14.54, 1.6) * mm, "end": v(14.51, 1.65) * mm});
            skLineSegment(sketch, "E901", {"start": v(14.51, 1.65) * mm, "end": v(14.42, 1.77) * mm});
            skLineSegment(sketch, "E902", {"start": v(14.42, 1.77) * mm, "end": v(14.3, 1.85) * mm});
            skLineSegment(sketch, "E903", {"start": v(14.3, 1.85) * mm, "end": v(14.14, 1.86) * mm});
            skLineSegment(sketch, "E904", {"start": v(14.14, 1.86) * mm, "end": v(14, 1.81) * mm});
            skLineSegment(sketch, "E905", {"start": v(14, 1.81) * mm, "end": v(13.95, 1.8) * mm});
            skLineSegment(sketch, "E906", {"start": v(13.95, 1.8) * mm, "end": v(13.74, 1.68) * mm});
            skLineSegment(sketch, "E907", {"start": v(13.74, 1.68) * mm, "end": v(11.68, 0.6) * mm});
            skLineSegment(sketch, "E908", {"start": v(11.68, 0.6) * mm, "end": v(11.47, 0.5) * mm});
            skLineSegment(sketch, "E909", {"start": v(11.47, 0.5) * mm, "end": v(11.42, 0.47) * mm});
            skLineSegment(sketch, "E910", {"start": v(11.42, 0.47) * mm, "end": v(10.93, 0.22) * mm});
            skLineSegment(sketch, "E911", {"start": v(10.93, 0.22) * mm, "end": v(10.9, 0.2) * mm});
            skLineSegment(sketch, "E912", {"start": v(10.92, 1.46) * mm, "end": v(11.04, 1.52) * mm});
            skLineSegment(sketch, "E913", {"start": v(11.04, 1.52) * mm, "end": v(12.44, 2.3) * mm});
            skLineSegment(sketch, "E914", {"start": v(12.44, 2.3) * mm, "end": v(12.58, 2.38) * mm});
            skLineSegment(sketch, "E915", {"start": v(12.58, 2.38) * mm, "end": v(12.68, 2.43) * mm});
            skLineSegment(sketch, "E916", {"start": v(12.68, 2.43) * mm, "end": v(12.95, 2.66) * mm});
            skLineSegment(sketch, "E917", {"start": v(12.95, 2.66) * mm, "end": v(13.24, 3) * mm});
            skLineSegment(sketch, "E918", {"start": v(13.24, 3) * mm, "end": v(13.47, 3.4) * mm});
            skLineSegment(sketch, "E919", {"start": v(13.47, 3.4) * mm, "end": v(13.61, 3.71) * mm});
            skLineSegment(sketch, "E920", {"start": v(13.61, 3.71) * mm, "end": v(13.66, 3.82) * mm});
            skLineSegment(sketch, "E921", {"start": v(13.66, 3.82) * mm, "end": v(13.71, 3.95) * mm});
            skLineSegment(sketch, "E922", {"start": v(13.71, 3.95) * mm, "end": v(13.85, 4.34) * mm});
            skLineSegment(sketch, "E923", {"start": v(13.85, 4.34) * mm, "end": v(13.98, 4.85) * mm});
            skLineSegment(sketch, "E924", {"start": v(13.98, 4.85) * mm, "end": v(14.06, 5.38) * mm});
            skLineSegment(sketch, "E925", {"start": v(14.06, 5.38) * mm, "end": v(14.1, 5.9) * mm});
            skLineSegment(sketch, "E926", {"start": v(14.1, 5.9) * mm, "end": v(14.09, 6.42) * mm});
            skLineSegment(sketch, "E927", {"start": v(14.09, 6.42) * mm, "end": v(14.05, 6.95) * mm});
            skLineSegment(sketch, "E928", {"start": v(14.05, 6.95) * mm, "end": v(13.98, 7.48) * mm});
            skLineSegment(sketch, "E929", {"start": v(13.98, 7.48) * mm, "end": v(13.91, 7.88) * mm});
            skLineSegment(sketch, "E930", {"start": v(13.91, 7.88) * mm, "end": v(13.89, 8) * mm});
            skLineSegment(sketch, "E931", {"start": v(13.89, 8) * mm, "end": v(13.86, 8.16) * mm});
            skLineSegment(sketch, "E932", {"start": v(13.86, 8.16) * mm, "end": v(13.68, 8.93) * mm});
            skLineSegment(sketch, "E933", {"start": v(13.68, 8.93) * mm, "end": v(13.49, 9.7) * mm});
            skLineSegment(sketch, "E934", {"start": v(13.49, 9.7) * mm, "end": v(13.45, 9.85) * mm});
            skLineSegment(sketch, "E935", {"start": v(13.45, 9.85) * mm, "end": v(13.44, 9.88) * mm});
            skLineSegment(sketch, "E936", {"start": v(13.44, 9.88) * mm, "end": v(13.37, 10.04) * mm});
            skLineSegment(sketch, "E937", {"start": v(13.37, 10.04) * mm, "end": v(13.3, 10.2) * mm});
            skLineSegment(sketch, "E938", {"start": v(13.3, 10.2) * mm, "end": v(13.28, 10.24) * mm});
            skLineSegment(sketch, "E939", {"start": v(13.28, 10.24) * mm, "end": v(13.3, 10.23) * mm});
            skLineSegment(sketch, "E940", {"start": v(13.3, 10.23) * mm, "end": v(13.4, 10.12) * mm});
            skLineSegment(sketch, "E941", {"start": v(13.4, 10.12) * mm, "end": v(13.4, 10.1) * mm});
            skLineSegment(sketch, "E942", {"start": v(13.4, 10.1) * mm, "end": v(13.54, 9.84) * mm});
            skLineSegment(sketch, "E943", {"start": v(13.54, 9.84) * mm, "end": v(13.94, 9.06) * mm});
            skLineSegment(sketch, "E944", {"start": v(13.94, 9.06) * mm, "end": v(14.41, 7.99) * mm});
            skLineSegment(sketch, "E945", {"start": v(14.41, 7.99) * mm, "end": v(14.8, 6.88) * mm});
            skLineSegment(sketch, "E946", {"start": v(14.8, 6.88) * mm, "end": v(15.05, 6.04) * mm});
            skLineSegment(sketch, "E947", {"start": v(15.05, 6.04) * mm, "end": v(15.11, 5.75) * mm});
            skLineSegment(sketch, "E948", {"start": v(15.11, 5.75) * mm, "end": v(15.15, 5.6) * mm});
            skLineSegment(sketch, "E949", {"start": v(15.15, 5.6) * mm, "end": v(15.22, 4.8) * mm});
            skLineSegment(sketch, "E950", {"start": v(15.22, 4.8) * mm, "end": v(15.23, 4) * mm});
            skLineSegment(sketch, "E951", {"start": v(15.23, 4) * mm, "end": v(15.23, 3.85) * mm});
            skLineSegment(sketch, "E952", {"start": v(15.23, 3.85) * mm, "end": v(15.23, 3.76) * mm});
            skLineSegment(sketch, "E953", {"start": v(15.23, 3.76) * mm, "end": v(15.3, 3.33) * mm});
            skLineSegment(sketch, "E954", {"start": v(15.3, 3.33) * mm, "end": v(15.45, 2.93) * mm});
            skLineSegment(sketch, "E955", {"start": v(15.45, 2.93) * mm, "end": v(15.5, 2.85) * mm});
            skLineSegment(sketch, "E956", {"start": v(15.5, 2.85) * mm, "end": v(15.56, 2.77) * mm});
            skLineSegment(sketch, "E957", {"start": v(15.56, 2.77) * mm, "end": v(15.67, 2.5) * mm});
            skLineSegment(sketch, "E958", {"start": v(15.67, 2.5) * mm, "end": v(15.72, 2.15) * mm});
            skLineSegment(sketch, "E959", {"start": v(15.72, 2.15) * mm, "end": v(15.68, 1.79) * mm});
            skLineSegment(sketch, "E960", {"start": v(15.68, 1.79) * mm, "end": v(15.6, 1.51) * mm});
            skLineSegment(sketch, "E961", {"start": v(15.6, 1.51) * mm, "end": v(15.56, 1.43) * mm});
            skLineSegment(sketch, "E962", {"start": v(15.56, 1.43) * mm, "end": v(15.54, 1.38) * mm});
            skLineSegment(sketch, "E963", {"start": v(15.54, 1.38) * mm, "end": v(15.46, 1.14) * mm});
            skLineSegment(sketch, "E964", {"start": v(15.46, 1.14) * mm, "end": v(15.37, 0.9) * mm});
            skLineSegment(sketch, "E965", {"start": v(15.37, 0.9) * mm, "end": v(15.34, 0.85) * mm});
            skLineSegment(sketch, "E966", {"start": v(15.34, 0.85) * mm, "end": v(15.33, 0.83) * mm});
            skLineSegment(sketch, "E967", {"start": v(15.33, 0.83) * mm, "end": v(15.22, 0.72) * mm});
            skLineSegment(sketch, "E968", {"start": v(15.22, 0.72) * mm, "end": v(15.1, 0.63) * mm});
            skLineSegment(sketch, "E969", {"start": v(15.1, 0.63) * mm, "end": v(15.07, 0.6) * mm});
            skLineSegment(sketch, "E970", {"start": v(15.07, 0.6) * mm, "end": v(15, 0.56) * mm});
            skLineSegment(sketch, "E971", {"start": v(15, 0.56) * mm, "end": v(14.35, 0.1) * mm});
            skLineSegment(sketch, "E972", {"start": v(14.35, 0.1) * mm, "end": v(14.3, 0.06) * mm});
            skLineSegment(sketch, "E973", {"start": v(0.9, 8.29) * mm, "end": v(0.94, 8.39) * mm});
            skLineSegment(sketch, "E974", {"start": v(0.94, 8.39) * mm, "end": v(1.17, 9.04) * mm});
            skLineSegment(sketch, "E975", {"start": v(1.17, 9.04) * mm, "end": v(1.3, 9.74) * mm});
            skLineSegment(sketch, "E976", {"start": v(1.3, 9.74) * mm, "end": v(1.3, 9.9) * mm});
            skLineSegment(sketch, "E977", {"start": v(1.3, 9.9) * mm, "end": v(1.3, 10) * mm});
            skLineSegment(sketch, "E978", {"start": v(1.3, 10) * mm, "end": v(1.4, 11.16) * mm});
            skLineSegment(sketch, "E979", {"start": v(1.4, 11.16) * mm, "end": v(1.4, 11.27) * mm});
            skLineSegment(sketch, "E980", {"start": v(1.4, 11.27) * mm, "end": v(1.42, 11.42) * mm});
            skLineSegment(sketch, "E981", {"start": v(1.42, 11.42) * mm, "end": v(1.53, 11.87) * mm});
            skLineSegment(sketch, "E982", {"start": v(1.53, 11.87) * mm, "end": v(1.78, 12.37) * mm});
            skLineSegment(sketch, "E983", {"start": v(1.78, 12.37) * mm, "end": v(2.16, 12.8) * mm});
            skLineSegment(sketch, "E984", {"start": v(2.16, 12.8) * mm, "end": v(2.51, 13.07) * mm});
            skLineSegment(sketch, "E985", {"start": v(2.51, 13.07) * mm, "end": v(2.64, 13.15) * mm});
            skLineSegment(sketch, "E986", {"start": v(2.64, 13.15) * mm, "end": v(2.7, 13.18) * mm});
            skLineSegment(sketch, "E987", {"start": v(2.7, 13.18) * mm, "end": v(3.22, 13.43) * mm});
            skLineSegment(sketch, "E988", {"start": v(3.22, 13.43) * mm, "end": v(3.27, 13.45) * mm});
            skLineSegment(sketch, "E989", {"start": v(3.27, 13.45) * mm, "end": v(3.28, 13.45) * mm});
            skLineSegment(sketch, "E990", {"start": v(3.28, 13.45) * mm, "end": v(3.3, 13.4) * mm});
            skLineSegment(sketch, "E991", {"start": v(3.3, 13.4) * mm, "end": v(3.31, 13.4) * mm});
            skLineSegment(sketch, "E992", {"start": v(3.31, 13.4) * mm, "end": v(3.3, 13.39) * mm});
            skLineSegment(sketch, "E993", {"start": v(3.3, 13.39) * mm, "end": v(3.24, 13.28) * mm});
            skLineSegment(sketch, "E994", {"start": v(3.24, 13.28) * mm, "end": v(3.23, 13.28) * mm});
            skLineSegment(sketch, "E995", {"start": v(3.23, 13.28) * mm, "end": v(3.14, 13.16) * mm});
            skLineSegment(sketch, "E996", {"start": v(3.14, 13.16) * mm, "end": v(2.9, 12.77) * mm});
            skLineSegment(sketch, "E997", {"start": v(2.9, 12.77) * mm, "end": v(2.73, 12.24) * mm});
            skLineSegment(sketch, "E998", {"start": v(2.73, 12.24) * mm, "end": v(2.72, 11.68) * mm});
            skLineSegment(sketch, "E999", {"start": v(2.72, 11.68) * mm, "end": v(2.8, 11.25) * mm});
            skLineSegment(sketch, "E1000", {"start": v(2.8, 11.25) * mm, "end": v(2.85, 11.12) * mm});
            skLineSegment(sketch, "E1001", {"start": v(2.85, 11.12) * mm, "end": v(2.93, 10.9) * mm});
            skLineSegment(sketch, "E1002", {"start": v(2.93, 10.9) * mm, "end": v(3.35, 9.88) * mm});
            skLineSegment(sketch, "E1003", {"start": v(3.35, 9.88) * mm, "end": v(3.8, 8.86) * mm});
            skLineSegment(sketch, "E1004", {"start": v(3.8, 8.86) * mm, "end": v(3.9, 8.66) * mm});
            skLineSegment(sketch, "E1005", {"start": v(3.9, 8.66) * mm, "end": v(4.03, 8.38) * mm});
            skLineSegment(sketch, "E1006", {"start": v(4.03, 8.38) * mm, "end": v(5.31, 5.64) * mm});
            skLineSegment(sketch, "E1007", {"start": v(5.31, 5.64) * mm, "end": v(5.44, 5.36) * mm});
            skLineSegment(sketch, "E1008", {"start": v(5.44, 5.36) * mm, "end": v(5.46, 5.33) * mm});
            skLineSegment(sketch, "E1009", {"start": v(5.46, 5.33) * mm, "end": v(5.5, 5.2) * mm});
            skLineSegment(sketch, "E1010", {"start": v(5.5, 5.2) * mm, "end": v(5.56, 5.05) * mm});
            skLineSegment(sketch, "E1011", {"start": v(5.56, 5.05) * mm, "end": v(5.58, 5.02) * mm});
            skLineSegment(sketch, "E1012", {"start": v(5.58, 5.02) * mm, "end": v(5.6, 4.98) * mm});
            skLineSegment(sketch, "E1013", {"start": v(5.6, 4.98) * mm, "end": v(5.68, 4.87) * mm});
            skLineSegment(sketch, "E1014", {"start": v(5.68, 4.87) * mm, "end": v(5.8, 4.8) * mm});
            skLineSegment(sketch, "E1015", {"start": v(5.8, 4.8) * mm, "end": v(5.93, 4.81) * mm});
            skLineSegment(sketch, "E1016", {"start": v(5.93, 4.81) * mm, "end": v(6.05, 4.88) * mm});
            skLineSegment(sketch, "E1017", {"start": v(6.05, 4.88) * mm, "end": v(6.09, 4.91) * mm});
            skLineSegment(sketch, "E1018", {"start": v(6.09, 4.91) * mm, "end": v(6.12, 4.94) * mm});
            skLineSegment(sketch, "E1019", {"start": v(6.12, 4.94) * mm, "end": v(6.27, 5.1) * mm});
            skLineSegment(sketch, "E1020", {"start": v(6.27, 5.1) * mm, "end": v(6.38, 5.27) * mm});
            skLineSegment(sketch, "E1021", {"start": v(6.38, 5.27) * mm, "end": v(6.4, 5.3) * mm});
            skLineSegment(sketch, "E1022", {"start": v(6.4, 5.3) * mm, "end": v(6.43, 5.39) * mm});
            skLineSegment(sketch, "E1023", {"start": v(6.43, 5.39) * mm, "end": v(6.57, 5.79) * mm});
            skLineSegment(sketch, "E1024", {"start": v(6.57, 5.79) * mm, "end": v(6.7, 6.2) * mm});
            skLineSegment(sketch, "E1025", {"start": v(6.7, 6.2) * mm, "end": v(6.73, 6.28) * mm});
            skLineSegment(sketch, "E1026", {"start": v(6.73, 6.28) * mm, "end": v(6.73, 6.27) * mm});
            skLineSegment(sketch, "E1027", {"start": v(6.73, 6.27) * mm, "end": v(6.77, 6.2) * mm});
            skLineSegment(sketch, "E1028", {"start": v(6.77, 6.2) * mm, "end": v(6.8, 6.13) * mm});
            skLineSegment(sketch, "E1029", {"start": v(6.8, 6.13) * mm, "end": v(6.8, 6.11) * mm});
            skLineSegment(sketch, "E1030", {"start": v(6.8, 6.11) * mm, "end": v(6.84, 5.97) * mm});
            skLineSegment(sketch, "E1031", {"start": v(6.84, 5.97) * mm, "end": v(6.88, 5.52) * mm});
            skLineSegment(sketch, "E1032", {"start": v(6.88, 5.52) * mm, "end": v(6.83, 4.96) * mm});
            skLineSegment(sketch, "E1033", {"start": v(6.83, 4.96) * mm, "end": v(6.63, 4.43) * mm});
            skLineSegment(sketch, "E1034", {"start": v(6.63, 4.43) * mm, "end": v(6.36, 4.06) * mm});
            skLineSegment(sketch, "E1035", {"start": v(6.36, 4.06) * mm, "end": v(6.25, 3.96) * mm});
            skLineSegment(sketch, "E1036", {"start": v(6.25, 3.96) * mm, "end": v(6.23, 3.94) * mm});
            skLineSegment(sketch, "E1037", {"start": v(6.23, 3.94) * mm, "end": v(6.2, 3.88) * mm});
            skLineSegment(sketch, "E1038", {"start": v(6.2, 3.88) * mm, "end": v(6.18, 3.82) * mm});
            skLineSegment(sketch, "E1039", {"start": v(6.18, 3.82) * mm, "end": v(6.2, 3.75) * mm});
            skLineSegment(sketch, "E1040", {"start": v(6.2, 3.75) * mm, "end": v(6.23, 3.7) * mm});
            skLineSegment(sketch, "E1041", {"start": v(6.23, 3.7) * mm, "end": v(6.24, 3.7) * mm});
            skLineSegment(sketch, "E1042", {"start": v(6.24, 3.7) * mm, "end": v(6.3, 3.58) * mm});
            skLineSegment(sketch, "E1043", {"start": v(6.3, 3.58) * mm, "end": v(6.59, 3.04) * mm});
            skLineSegment(sketch, "E1044", {"start": v(7.4, 1.57) * mm, "end": v(7.63, 1.27) * mm});
            skLineSegment(sketch, "E1045", {"start": v(7.63, 1.27) * mm, "end": v(7.7, 1.18) * mm});
            skLineSegment(sketch, "E1046", {"start": v(7.7, 1.18) * mm, "end": v(7.77, 1.09) * mm});
            skLineSegment(sketch, "E1047", {"start": v(7.77, 1.09) * mm, "end": v(8.03, 0.86) * mm});
            skLineSegment(sketch, "E1048", {"start": v(8.03, 0.86) * mm, "end": v(8.42, 0.7) * mm});
            skLineSegment(sketch, "E1049", {"start": v(8.42, 0.7) * mm, "end": v(8.84, 0.67) * mm});
            skLineSegment(sketch, "E1050", {"start": v(8.84, 0.67) * mm, "end": v(9.18, 0.71) * mm});
            skLineSegment(sketch, "E1051", {"start": v(9.18, 0.71) * mm, "end": v(9.28, 0.74) * mm});
            skLineSegment(sketch, "E1052", {"start": v(9.28, 0.74) * mm, "end": v(9.36, 0.76) * mm});
            skLineSegment(sketch, "E1053", {"start": v(9.36, 0.76) * mm, "end": v(10.06, 1.01) * mm});
            skLineSegment(sketch, "E1054", {"start": v(10.06, 1.01) * mm, "end": v(10.1, 1.04) * mm});
            skLineSegment(sketch, "E1055", {"start": v(0.3, 6.4) * mm, "end": v(0.26, 6.38) * mm});
            skLineSegment(sketch, "E1056", {"start": v(0.26, 6.38) * mm, "end": v(-0.02, 6.33) * mm});
            skLineSegment(sketch, "E1057", {"start": v(-0.02, 6.33) * mm, "end": v(-0.4, 6.32) * mm});
            skLineSegment(sketch, "E1058", {"start": v(-0.4, 6.32) * mm, "end": v(-0.8, 6.37) * mm});
            skLineSegment(sketch, "E1059", {"start": v(-0.8, 6.37) * mm, "end": v(-1.1, 6.44) * mm});
            skLineSegment(sketch, "E1060", {"start": v(-1.1, 6.44) * mm, "end": v(-1.19, 6.47) * mm});
            skLineSegment(sketch, "E1061", {"start": v(-1.19, 6.47) * mm, "end": v(-1.2, 6.47) * mm});
            skLineSegment(sketch, "E1062", {"start": v(-1.2, 6.47) * mm, "end": v(-1.34, 6.54) * mm});
            skLineSegment(sketch, "E1063", {"start": v(5.2, 2.65) * mm, "end": v(5.4, 2.24) * mm});
            skLineSegment(sketch, "E1064.trimOffspring", {"start": v(5.4, 2.24) * mm, "end": v(5.2, 2.65) * mm});
            skLineSegment(sketch, "E1065", {"start": v(-9, 1.8) * mm, "end": v(-9.18, 1.73) * mm});
            skLineSegment(sketch, "E1066.0", {"start": v(-13.64, -9.48) * mm, "end": v(15.57, 5.86) * mm, "construction": true});
            skLineSegment(sketch, "E1066.1", {"start": v(15.57, 5.86) * mm, "end": v(13.3, 10.2) * mm, "construction": true});
            skLineSegment(sketch, "E1067", {"start": v(-0.4, -4.78) * mm, "end": v(-0.32, -4.98) * mm});
            skLineSegment(sketch, "E1068", {"start": v(-13.66, 3.48) * mm, "end": v(-14.1, 2.58) * mm});
            skLineSegment(sketch, "E1069", {"start": v(-12.8, 3.63) * mm, "end": v(-13.4, 2.67) * mm});
            skLineSegment(sketch, "E1070", {"start": v(-10.16, 2.27) * mm, "end": v(-10.02, 1.35) * mm});
            skLineSegment(sketch, "E1071", {"start": v(-8.95, 2.5) * mm, "end": v(-9.12, 2.27) * mm});
            skLineSegment(sketch, "E1072", {"start": v(-9.12, 2.27) * mm, "end": v(-9.2, 1.93) * mm});
            skLineSegment(sketch, "E1073", {"start": v(-9.2, 1.93) * mm, "end": v(-9.18, 1.73) * mm});
            skLineSegment(sketch, "E1074", {"start": v(-4.62, -3.06) * mm, "end": v(-4.94, -4.22) * mm});
            skLineSegment(sketch, "E1075", {"start": v(-5.05, -3.17) * mm, "end": v(-5.22, -4.36) * mm});
            skLineSegment(sketch, "E1076", {"start": v(-4.52, 7.6) * mm, "end": v(-3.34, 7.97) * mm});
            skLineSegment(sketch, "E1077", {"start": v(-3.8, 6.3) * mm, "end": v(-2.68, 6.47) * mm});
            skLineSegment(sketch, "E1078", {"start": v(6.59, 3.04) * mm, "end": v(7.4, 1.57) * mm});
            skLineSegment(sketch, "E1079", {"start": v(5.4, 2.24) * mm, "end": v(6.12, 0.85) * mm});
            skLineSegment(sketch, "E1080", {"start": v(13.23, 0.1) * mm, "end": v(12.14, 0.06) * mm});
            skLineSegment(sketch, "E1081", {"start": v(12.3, -0.74) * mm, "end": v(13.34, -0.53) * mm});
            skSolve(sketch);
        }
        {
            var Q0;
            Q0 = qSketchRegion(id + "F3", true);
            extrude(context, id + "F4", {"entities" : qUnion([Q0]), "operationType" : NewBodyOperationType.REMOVE, "oppositeDirection" : true, "depth" : 25 * mm, "offsetDistance" : 25 * mm});
        }
        {
            var Q0;
            Q0=qCreatedBy(makeId("Front.planeOp"),FACE);
            var sketch = newSketch(context, id + "F5", { "sketchPlane" : qUnion([Q0])});
            skCircle(sketch, "E1082", {"center": v(-15, 5) * mm, "radius": 4 * mm});
            skSolve(sketch);
        }
        {
            var Q0;
            Q0 = qSketchRegion(id + "F5", true);
            var Q1;
            Q1=sQuery(id+"F0.wireOp",EDGE,"E3");
            revolve(context, id + "F6", {"operationType" : NewBodyOperationType.ADD, "entities" : qUnion([Q0]), "axis" : qUnion([Q1]), "revolveType" : RevolveType.FULL});
        }
        {
            var Q0;
            Q0=qCreatedBy(makeId("Top.planeOp"),FACE);
            var sketch = newSketch(context, id + "F7", { "sketchPlane" : qUnion([Q0])});
            skCircle(sketch, "E1083", {"center": v(0, 21) * mm, "radius": 4 * mm});
            skSolve(sketch);
        }
        {
            var Q0;
            Q0 = qSketchRegion(id + "F7", true);
            extrude(context, id + "F8", {"entities" : qUnion([Q0]), "operationType" : NewBodyOperationType.REMOVE, "depth" : 20 * mm, "offsetDistance" : 25 * mm});
        }
        {
            var Q0;
            Q0=makeQuery(id+"F8.boolean.opBoolean","INTERSECT",EDGE,{"derivedFrom":[makeQuery(id+"F4.boolean.opBoolean","SPLIT",FACE,{"disambiguationData":[TD([makeQuery(id+"F1.opRevolve","SWEPT_FACE",FACE,{"disambiguationData":[OSD([sQuery(id+"F0.wireOp",EDGE,"E1")])]}),makeQuery(id+"F1.opRevolve","SWEPT_FACE",FACE,{"disambiguationData":[OSD([sQuery(id+"F0.wireOp",EDGE,"E2")])]}),makeQuery(id+"F4.opExtrude","SWEPT_FACE",FACE,{"disambiguationData":[OSD([sQuery(id+"F3.wireOp",EDGE,"E22")])]}),makeQuery(id+"F4.opExtrude","SWEPT_FACE",FACE,{"disambiguationData":[OSD([sQuery(id+"F3.wireOp",EDGE,"E23")])]}),makeQuery(id+"F4.opExtrude","SWEPT_FACE",FACE,{"disambiguationData":[OSD([sQuery(id+"F3.wireOp",EDGE,"E24")])]}),makeQuery(id+"F4.opExtrude","SWEPT_FACE",FACE,{"disambiguationData":[OSD([sQuery(id+"F3.wireOp",EDGE,"E25")])]}),makeQuery(id+"F4.opExtrude","SWEPT_FACE",FACE,{"disambiguationData":[OSD([sQuery(id+"F3.wireOp",EDGE,"E26")])]}),makeQuery(id+"F4.opExtrude","SWEPT_FACE",FACE,{"disambiguationData":[OSD([sQuery(id+"F3.wireOp",EDGE,"E27")])]}),makeQuery(id+"F4.opExtrude","SWEPT_FACE",FACE,{"disambiguationData":[OSD([sQuery(id+"F3.wireOp",EDGE,"E28")])]}),makeQuery(id+"F4.opExtrude","SWEPT_FACE",FACE,{"disambiguationData":[OSD([sQuery(id+"F3.wireOp",EDGE,"E29")])]}),makeQuery(id+"F4.opExtrude","SWEPT_FACE",FACE,{"disambiguationData":[OSD([sQuery(id+"F3.wireOp",EDGE,"E30")])]}),makeQuery(id+"F4.opExtrude","SWEPT_FACE",FACE,{"disambiguationData":[OSD([sQuery(id+"F3.wireOp",EDGE,"E31")])]}),makeQuery(id+"F4.opExtrude","SWEPT_FACE",FACE,{"disambiguationData":[OSD([sQuery(id+"F3.wireOp",EDGE,"E32")])]}),makeQuery(id+"F4.opExtrude","SWEPT_FACE",FACE,{"disambiguationData":[OSD([sQuery(id+"F3.wireOp",EDGE,"E33")])]}),makeQuery(id+"F4.opExtrude","SWEPT_FACE",FACE,{"disambiguationData":[OSD([sQuery(id+"F3.wireOp",EDGE,"E34")])]}),makeQuery(id+"F4.opExtrude","SWEPT_FACE",FACE,{"disambiguationData":[OSD([sQuery(id+"F3.wireOp",EDGE,"E35")])]}),makeQuery(id+"F4.opExtrude","SWEPT_FACE",FACE,{"disambiguationData":[OSD([sQuery(id+"F3.wireOp",EDGE,"E36")])]}),makeQuery(id+"F4.opExtrude","SWEPT_FACE",FACE,{"disambiguationData":[OSD([sQuery(id+"F3.wireOp",EDGE,"E37")])]}),makeQuery(id+"F4.opExtrude","SWEPT_FACE",FACE,{"disambiguationData":[OSD([sQuery(id+"F3.wireOp",EDGE,"E38")])]}),makeQuery(id+"F4.opExtrude","SWEPT_FACE",FACE,{"disambiguationData":[OSD([sQuery(id+"F3.wireOp",EDGE,"E39")])]}),makeQuery(id+"F4.opExtrude","SWEPT_FACE",FACE,{"disambiguationData":[OSD([sQuery(id+"F3.wireOp",EDGE,"E40")])]}),makeQuery(id+"F4.opExtrude","SWEPT_FACE",FACE,{"disambiguationData":[OSD([sQuery(id+"F3.wireOp",EDGE,"E41")])]}),makeQuery(id+"F4.opExtrude","SWEPT_FACE",FACE,{"disambiguationData":[OSD([sQuery(id+"F3.wireOp",EDGE,"E42")])]}),makeQuery(id+"F4.opExtrude","SWEPT_FACE",FACE,{"disambiguationData":[OSD([sQuery(id+"F3.wireOp",EDGE,"E43")])]}),makeQuery(id+"F4.opExtrude","SWEPT_FACE",FACE,{"disambiguationData":[OSD([sQuery(id+"F3.wireOp",EDGE,"E44")])]}),makeQuery(id+"F4.opExtrude","SWEPT_FACE",FACE,{"disambiguationData":[OSD([sQuery(id+"F3.wireOp",EDGE,"E45")])]}),makeQuery(id+"F4.opExtrude","SWEPT_FACE",FACE,{"disambiguationData":[OSD([sQuery(id+"F3.wireOp",EDGE,"E46")])]}),makeQuery(id+"F4.opExtrude","SWEPT_FACE",FACE,{"disambiguationData":[OSD([sQuery(id+"F3.wireOp",EDGE,"E47")])]}),makeQuery(id+"F4.opExtrude","SWEPT_FACE",FACE,{"disambiguationData":[OSD([sQuery(id+"F3.wireOp",EDGE,"E48")])]}),makeQuery(id+"F4.opExtrude","SWEPT_FACE",FACE,{"disambiguationData":[OSD([sQuery(id+"F3.wireOp",EDGE,"E49")])]}),makeQuery(id+"F4.opExtrude","SWEPT_FACE",FACE,{"disambiguationData":[OSD([sQuery(id+"F3.wireOp",EDGE,"E50")])]}),makeQuery(id+"F4.opExtrude","SWEPT_FACE",FACE,{"disambiguationData":[OSD([sQuery(id+"F3.wireOp",EDGE,"E51")])]}),makeQuery(id+"F4.opExtrude","SWEPT_FACE",FACE,{"disambiguationData":[OSD([sQuery(id+"F3.wireOp",EDGE,"E52")])]}),makeQuery(id+"F4.opExtrude","SWEPT_FACE",FACE,{"disambiguationData":[OSD([sQuery(id+"F3.wireOp",EDGE,"E53")])]}),makeQuery(id+"F4.opExtrude","SWEPT_FACE",FACE,{"disambiguationData":[OSD([sQuery(id+"F3.wireOp",EDGE,"E54")])]}),makeQuery(id+"F4.opExtrude","SWEPT_FACE",FACE,{"disambiguationData":[OSD([sQuery(id+"F3.wireOp",EDGE,"E55")])]}),makeQuery(id+"F4.opExtrude","SWEPT_FACE",FACE,{"disambiguationData":[OSD([sQuery(id+"F3.wireOp",EDGE,"E56")])]}),makeQuery(id+"F4.opExtrude","SWEPT_FACE",FACE,{"disambiguationData":[OSD([sQuery(id+"F3.wireOp",EDGE,"E57")])]}),makeQuery(id+"F4.opExtrude","SWEPT_FACE",FACE,{"disambiguationData":[OSD([sQuery(id+"F3.wireOp",EDGE,"E58")])]}),makeQuery(id+"F4.opExtrude","SWEPT_FACE",FACE,{"disambiguationData":[OSD([sQuery(id+"F3.wireOp",EDGE,"E59")])]}),makeQuery(id+"F4.opExtrude","SWEPT_FACE",FACE,{"disambiguationData":[OSD([sQuery(id+"F3.wireOp",EDGE,"E60")])]}),makeQuery(id+"F4.opExtrude","SWEPT_FACE",FACE,{"disambiguationData":[OSD([sQuery(id+"F3.wireOp",EDGE,"E61")])]}),makeQuery(id+"F4.opExtrude","SWEPT_FACE",FACE,{"disambiguationData":[OSD([sQuery(id+"F3.wireOp",EDGE,"E62")])]}),makeQuery(id+"F4.opExtrude","SWEPT_FACE",FACE,{"disambiguationData":[OSD([sQuery(id+"F3.wireOp",EDGE,"E63")])]}),makeQuery(id+"F4.opExtrude","SWEPT_FACE",FACE,{"disambiguationData":[OSD([sQuery(id+"F3.wireOp",EDGE,"E64")])]}),makeQuery(id+"F4.opExtrude","SWEPT_FACE",FACE,{"disambiguationData":[OSD([sQuery(id+"F3.wireOp",EDGE,"E65")])]}),makeQuery(id+"F4.opExtrude","SWEPT_FACE",FACE,{"disambiguationData":[OSD([sQuery(id+"F3.wireOp",EDGE,"E66")])]}),makeQuery(id+"F4.opExtrude","SWEPT_FACE",FACE,{"disambiguationData":[OSD([sQuery(id+"F3.wireOp",EDGE,"E67")])]}),makeQuery(id+"F4.opExtrude","SWEPT_FACE",FACE,{"disambiguationData":[OSD([sQuery(id+"F3.wireOp",EDGE,"E68")])]}),makeQuery(id+"F4.opExtrude","SWEPT_FACE",FACE,{"disambiguationData":[OSD([sQuery(id+"F3.wireOp",EDGE,"E69")])]}),makeQuery(id+"F4.opExtrude","SWEPT_FACE",FACE,{"disambiguationData":[OSD([sQuery(id+"F3.wireOp",EDGE,"E70")])]}),makeQuery(id+"F4.opExtrude","SWEPT_FACE",FACE,{"disambiguationData":[OSD([sQuery(id+"F3.wireOp",EDGE,"E71")])]}),makeQuery(id+"F4.opExtrude","SWEPT_FACE",FACE,{"disambiguationData":[OSD([sQuery(id+"F3.wireOp",EDGE,"E72")])]}),makeQuery(id+"F4.opExtrude","SWEPT_FACE",FACE,{"disambiguationData":[OSD([sQuery(id+"F3.wireOp",EDGE,"E73")])]}),makeQuery(id+"F4.opExtrude","SWEPT_FACE",FACE,{"disambiguationData":[OSD([sQuery(id+"F3.wireOp",EDGE,"E74")])]}),makeQuery(id+"F4.opExtrude","SWEPT_FACE",FACE,{"disambiguationData":[OSD([sQuery(id+"F3.wireOp",EDGE,"E75")])]}),makeQuery(id+"F4.opExtrude","SWEPT_FACE",FACE,{"disambiguationData":[OSD([sQuery(id+"F3.wireOp",EDGE,"E76")])]}),makeQuery(id+"F4.opExtrude","SWEPT_FACE",FACE,{"disambiguationData":[OSD([sQuery(id+"F3.wireOp",EDGE,"E77")])]}),makeQuery(id+"F4.opExtrude","SWEPT_FACE",FACE,{"disambiguationData":[OSD([sQuery(id+"F3.wireOp",EDGE,"E78")])]}),makeQuery(id+"F4.opExtrude","SWEPT_FACE",FACE,{"disambiguationData":[OSD([sQuery(id+"F3.wireOp",EDGE,"E79")])]}),makeQuery(id+"F4.opExtrude","SWEPT_FACE",FACE,{"disambiguationData":[OSD([sQuery(id+"F3.wireOp",EDGE,"E80")])]}),makeQuery(id+"F4.opExtrude","SWEPT_FACE",FACE,{"disambiguationData":[OSD([sQuery(id+"F3.wireOp",EDGE,"E81")])]}),makeQuery(id+"F4.opExtrude","SWEPT_FACE",FACE,{"disambiguationData":[OSD([sQuery(id+"F3.wireOp",EDGE,"E82")])]}),makeQuery(id+"F4.opExtrude","SWEPT_FACE",FACE,{"disambiguationData":[OSD([sQuery(id+"F3.wireOp",EDGE,"E83")])]}),makeQuery(id+"F4.opExtrude","SWEPT_FACE",FACE,{"disambiguationData":[OSD([sQuery(id+"F3.wireOp",EDGE,"E84")])]}),makeQuery(id+"F4.opExtrude","SWEPT_FACE",FACE,{"disambiguationData":[OSD([sQuery(id+"F3.wireOp",EDGE,"E85")])]}),makeQuery(id+"F4.opExtrude","SWEPT_FACE",FACE,{"disambiguationData":[OSD([sQuery(id+"F3.wireOp",EDGE,"E86")])]}),makeQuery(id+"F4.opExtrude","SWEPT_FACE",FACE,{"disambiguationData":[OSD([sQuery(id+"F3.wireOp",EDGE,"E87")])]}),makeQuery(id+"F4.opExtrude","SWEPT_FACE",FACE,{"disambiguationData":[OSD([sQuery(id+"F3.wireOp",EDGE,"E88")])]}),makeQuery(id+"F4.opExtrude","SWEPT_FACE",FACE,{"disambiguationData":[OSD([sQuery(id+"F3.wireOp",EDGE,"E89")])]}),makeQuery(id+"F4.opExtrude","SWEPT_FACE",FACE,{"disambiguationData":[OSD([sQuery(id+"F3.wireOp",EDGE,"E90")])]}),makeQuery(id+"F4.opExtrude","SWEPT_FACE",FACE,{"disambiguationData":[OSD([sQuery(id+"F3.wireOp",EDGE,"E91")])]}),makeQuery(id+"F4.opExtrude","SWEPT_FACE",FACE,{"disambiguationData":[OSD([sQuery(id+"F3.wireOp",EDGE,"E92")])]}),makeQuery(id+"F4.opExtrude","SWEPT_FACE",FACE,{"disambiguationData":[OSD([sQuery(id+"F3.wireOp",EDGE,"E153")])]}),makeQuery(id+"F4.opExtrude","SWEPT_FACE",FACE,{"disambiguationData":[OSD([sQuery(id+"F3.wireOp",EDGE,"E154")])]}),makeQuery(id+"F4.opExtrude","SWEPT_FACE",FACE,{"disambiguationData":[OSD([sQuery(id+"F3.wireOp",EDGE,"E155")])]}),makeQuery(id+"F4.opExtrude","SWEPT_FACE",FACE,{"disambiguationData":[OSD([sQuery(id+"F3.wireOp",EDGE,"E156")])]}),makeQuery(id+"F4.opExtrude","SWEPT_FACE",FACE,{"disambiguationData":[OSD([sQuery(id+"F3.wireOp",EDGE,"E157")])]}),makeQuery(id+"F4.opExtrude","SWEPT_FACE",FACE,{"disambiguationData":[OSD([sQuery(id+"F3.wireOp",EDGE,"E158")])]}),makeQuery(id+"F4.opExtrude","SWEPT_FACE",FACE,{"disambiguationData":[OSD([sQuery(id+"F3.wireOp",EDGE,"E159")])]}),makeQuery(id+"F4.opExtrude","SWEPT_FACE",FACE,{"disambiguationData":[OSD([sQuery(id+"F3.wireOp",EDGE,"E160")])]}),makeQuery(id+"F4.opExtrude","SWEPT_FACE",FACE,{"disambiguationData":[OSD([sQuery(id+"F3.wireOp",EDGE,"E161")])]}),makeQuery(id+"F4.opExtrude","SWEPT_FACE",FACE,{"disambiguationData":[OSD([sQuery(id+"F3.wireOp",EDGE,"E162")])]}),makeQuery(id+"F4.opExtrude","SWEPT_FACE",FACE,{"disambiguationData":[OSD([sQuery(id+"F3.wireOp",EDGE,"E163")])]}),makeQuery(id+"F4.opExtrude","SWEPT_FACE",FACE,{"disambiguationData":[OSD([sQuery(id+"F3.wireOp",EDGE,"E164")])]}),makeQuery(id+"F4.opExtrude","SWEPT_FACE",FACE,{"disambiguationData":[OSD([sQuery(id+"F3.wireOp",EDGE,"E165")])]}),makeQuery(id+"F4.opExtrude","SWEPT_FACE",FACE,{"disambiguationData":[OSD([sQuery(id+"F3.wireOp",EDGE,"E166")])]}),makeQuery(id+"F4.opExtrude","SWEPT_FACE",FACE,{"disambiguationData":[OSD([sQuery(id+"F3.wireOp",EDGE,"E167")])]}),makeQuery(id+"F4.opExtrude","SWEPT_FACE",FACE,{"disambiguationData":[OSD([sQuery(id+"F3.wireOp",EDGE,"E168")])]}),makeQuery(id+"F4.opExtrude","SWEPT_FACE",FACE,{"disambiguationData":[OSD([sQuery(id+"F3.wireOp",EDGE,"E169")])]}),makeQuery(id+"F4.opExtrude","SWEPT_FACE",FACE,{"disambiguationData":[OSD([sQuery(id+"F3.wireOp",EDGE,"E170")])]}),makeQuery(id+"F4.opExtrude","SWEPT_FACE",FACE,{"disambiguationData":[OSD([sQuery(id+"F3.wireOp",EDGE,"E171")])]}),makeQuery(id+"F4.opExtrude","SWEPT_FACE",FACE,{"disambiguationData":[OSD([sQuery(id+"F3.wireOp",EDGE,"E172")])]}),makeQuery(id+"F4.opExtrude","SWEPT_FACE",FACE,{"disambiguationData":[OSD([sQuery(id+"F3.wireOp",EDGE,"E173")])]}),makeQuery(id+"F4.opExtrude","SWEPT_FACE",FACE,{"disambiguationData":[OSD([sQuery(id+"F3.wireOp",EDGE,"E174")])]}),makeQuery(id+"F4.opExtrude","SWEPT_FACE",FACE,{"disambiguationData":[OSD([sQuery(id+"F3.wireOp",EDGE,"E175")])]}),makeQuery(id+"F4.opExtrude","SWEPT_FACE",FACE,{"disambiguationData":[OSD([sQuery(id+"F3.wireOp",EDGE,"E176")])]}),makeQuery(id+"F4.opExtrude","SWEPT_FACE",FACE,{"disambiguationData":[OSD([sQuery(id+"F3.wireOp",EDGE,"E177")])]}),makeQuery(id+"F4.opExtrude","SWEPT_FACE",FACE,{"disambiguationData":[OSD([sQuery(id+"F3.wireOp",EDGE,"E178")])]}),makeQuery(id+"F4.opExtrude","SWEPT_FACE",FACE,{"disambiguationData":[OSD([sQuery(id+"F3.wireOp",EDGE,"E179")])]}),makeQuery(id+"F4.opExtrude","SWEPT_FACE",FACE,{"disambiguationData":[OSD([sQuery(id+"F3.wireOp",EDGE,"E180")])]}),makeQuery(id+"F4.opExtrude","SWEPT_FACE",FACE,{"disambiguationData":[OSD([sQuery(id+"F3.wireOp",EDGE,"E181")])]}),makeQuery(id+"F4.opExtrude","SWEPT_FACE",FACE,{"disambiguationData":[OSD([sQuery(id+"F3.wireOp",EDGE,"E182")])]}),makeQuery(id+"F4.opExtrude","SWEPT_FACE",FACE,{"disambiguationData":[OSD([sQuery(id+"F3.wireOp",EDGE,"E183")])]}),makeQuery(id+"F4.opExtrude","SWEPT_FACE",FACE,{"disambiguationData":[OSD([sQuery(id+"F3.wireOp",EDGE,"E184")])]}),makeQuery(id+"F4.opExtrude","SWEPT_FACE",FACE,{"disambiguationData":[OSD([sQuery(id+"F3.wireOp",EDGE,"E185")])]}),makeQuery(id+"F4.opExtrude","SWEPT_FACE",FACE,{"disambiguationData":[OSD([sQuery(id+"F3.wireOp",EDGE,"E186")])]}),makeQuery(id+"F4.opExtrude","SWEPT_FACE",FACE,{"disambiguationData":[OSD([sQuery(id+"F3.wireOp",EDGE,"E187")])]}),makeQuery(id+"F4.opExtrude","SWEPT_FACE",FACE,{"disambiguationData":[OSD([sQuery(id+"F3.wireOp",EDGE,"E188")])]}),makeQuery(id+"F4.opExtrude","SWEPT_FACE",FACE,{"disambiguationData":[OSD([sQuery(id+"F3.wireOp",EDGE,"E189")])]}),makeQuery(id+"F4.opExtrude","SWEPT_FACE",FACE,{"disambiguationData":[OSD([sQuery(id+"F3.wireOp",EDGE,"E190")])]}),makeQuery(id+"F4.opExtrude","SWEPT_FACE",FACE,{"disambiguationData":[OSD([sQuery(id+"F3.wireOp",EDGE,"E191")])]}),makeQuery(id+"F4.opExtrude","SWEPT_FACE",FACE,{"disambiguationData":[OSD([sQuery(id+"F3.wireOp",EDGE,"E192")])]}),makeQuery(id+"F4.opExtrude","SWEPT_FACE",FACE,{"disambiguationData":[OSD([sQuery(id+"F3.wireOp",EDGE,"E193")])]}),makeQuery(id+"F4.opExtrude","SWEPT_FACE",FACE,{"disambiguationData":[OSD([sQuery(id+"F3.wireOp",EDGE,"E194")])]}),makeQuery(id+"F4.opExtrude","SWEPT_FACE",FACE,{"disambiguationData":[OSD([sQuery(id+"F3.wireOp",EDGE,"E195")])]}),makeQuery(id+"F4.opExtrude","SWEPT_FACE",FACE,{"disambiguationData":[OSD([sQuery(id+"F3.wireOp",EDGE,"E196")])]}),makeQuery(id+"F4.opExtrude","SWEPT_FACE",FACE,{"disambiguationData":[OSD([sQuery(id+"F3.wireOp",EDGE,"E197")])]}),makeQuery(id+"F4.opExtrude","SWEPT_FACE",FACE,{"disambiguationData":[OSD([sQuery(id+"F3.wireOp",EDGE,"E198")])]}),makeQuery(id+"F4.opExtrude","SWEPT_FACE",FACE,{"disambiguationData":[OSD([sQuery(id+"F3.wireOp",EDGE,"E199")])]}),makeQuery(id+"F4.opExtrude","SWEPT_FACE",FACE,{"disambiguationData":[OSD([sQuery(id+"F3.wireOp",EDGE,"E200")])]}),makeQuery(id+"F4.opExtrude","SWEPT_FACE",FACE,{"disambiguationData":[OSD([sQuery(id+"F3.wireOp",EDGE,"E201")])]}),makeQuery(id+"F4.opExtrude","SWEPT_FACE",FACE,{"disambiguationData":[OSD([sQuery(id+"F3.wireOp",EDGE,"E337")])]}),makeQuery(id+"F4.opExtrude","SWEPT_FACE",FACE,{"disambiguationData":[OSD([sQuery(id+"F3.wireOp",EDGE,"E338")])]}),makeQuery(id+"F4.opExtrude","SWEPT_FACE",FACE,{"disambiguationData":[OSD([sQuery(id+"F3.wireOp",EDGE,"E339")])]}),makeQuery(id+"F4.opExtrude","SWEPT_FACE",FACE,{"disambiguationData":[OSD([sQuery(id+"F3.wireOp",EDGE,"E340")])]}),makeQuery(id+"F4.opExtrude","SWEPT_FACE",FACE,{"disambiguationData":[OSD([sQuery(id+"F3.wireOp",EDGE,"E341")])]}),makeQuery(id+"F4.opExtrude","SWEPT_FACE",FACE,{"disambiguationData":[OSD([sQuery(id+"F3.wireOp",EDGE,"E342")])]}),makeQuery(id+"F4.opExtrude","SWEPT_FACE",FACE,{"disambiguationData":[OSD([sQuery(id+"F3.wireOp",EDGE,"E343")])]}),makeQuery(id+"F4.opExtrude","SWEPT_FACE",FACE,{"disambiguationData":[OSD([sQuery(id+"F3.wireOp",EDGE,"E344")])]}),makeQuery(id+"F4.opExtrude","SWEPT_FACE",FACE,{"disambiguationData":[OSD([sQuery(id+"F3.wireOp",EDGE,"E345")])]}),makeQuery(id+"F4.opExtrude","SWEPT_FACE",FACE,{"disambiguationData":[OSD([sQuery(id+"F3.wireOp",EDGE,"E346")])]}),makeQuery(id+"F4.opExtrude","SWEPT_FACE",FACE,{"disambiguationData":[OSD([sQuery(id+"F3.wireOp",EDGE,"E347")])]}),makeQuery(id+"F4.opExtrude","SWEPT_FACE",FACE,{"disambiguationData":[OSD([sQuery(id+"F3.wireOp",EDGE,"E348")])]}),makeQuery(id+"F4.opExtrude","SWEPT_FACE",FACE,{"disambiguationData":[OSD([sQuery(id+"F3.wireOp",EDGE,"E349")])]}),makeQuery(id+"F4.opExtrude","SWEPT_FACE",FACE,{"disambiguationData":[OSD([sQuery(id+"F3.wireOp",EDGE,"E350")])]}),makeQuery(id+"F4.opExtrude","SWEPT_FACE",FACE,{"disambiguationData":[OSD([sQuery(id+"F3.wireOp",EDGE,"E351")])]}),makeQuery(id+"F4.opExtrude","SWEPT_FACE",FACE,{"disambiguationData":[OSD([sQuery(id+"F3.wireOp",EDGE,"E352")])]}),makeQuery(id+"F4.opExtrude","SWEPT_FACE",FACE,{"disambiguationData":[OSD([sQuery(id+"F3.wireOp",EDGE,"E353")])]}),makeQuery(id+"F4.opExtrude","SWEPT_FACE",FACE,{"disambiguationData":[OSD([sQuery(id+"F3.wireOp",EDGE,"E354")])]}),makeQuery(id+"F4.opExtrude","SWEPT_FACE",FACE,{"disambiguationData":[OSD([sQuery(id+"F3.wireOp",EDGE,"E355")])]}),makeQuery(id+"F4.opExtrude","SWEPT_FACE",FACE,{"disambiguationData":[OSD([sQuery(id+"F3.wireOp",EDGE,"E356")])]}),makeQuery(id+"F4.opExtrude","SWEPT_FACE",FACE,{"disambiguationData":[OSD([sQuery(id+"F3.wireOp",EDGE,"E357")])]}),makeQuery(id+"F4.opExtrude","SWEPT_FACE",FACE,{"disambiguationData":[OSD([sQuery(id+"F3.wireOp",EDGE,"E358")])]}),makeQuery(id+"F4.opExtrude","SWEPT_FACE",FACE,{"disambiguationData":[OSD([sQuery(id+"F3.wireOp",EDGE,"E359")])]}),makeQuery(id+"F4.opExtrude","SWEPT_FACE",FACE,{"disambiguationData":[OSD([sQuery(id+"F3.wireOp",EDGE,"E360")])]}),makeQuery(id+"F4.opExtrude","SWEPT_FACE",FACE,{"disambiguationData":[OSD([sQuery(id+"F3.wireOp",EDGE,"E361")])]}),makeQuery(id+"F4.opExtrude","SWEPT_FACE",FACE,{"disambiguationData":[OSD([sQuery(id+"F3.wireOp",EDGE,"E362")])]}),makeQuery(id+"F4.opExtrude","SWEPT_FACE",FACE,{"disambiguationData":[OSD([sQuery(id+"F3.wireOp",EDGE,"E363")])]}),makeQuery(id+"F4.opExtrude","SWEPT_FACE",FACE,{"disambiguationData":[OSD([sQuery(id+"F3.wireOp",EDGE,"E364")])]}),makeQuery(id+"F4.opExtrude","SWEPT_FACE",FACE,{"disambiguationData":[OSD([sQuery(id+"F3.wireOp",EDGE,"E365")])]}),makeQuery(id+"F4.opExtrude","SWEPT_FACE",FACE,{"disambiguationData":[OSD([sQuery(id+"F3.wireOp",EDGE,"E366")])]}),makeQuery(id+"F4.opExtrude","SWEPT_FACE",FACE,{"disambiguationData":[OSD([sQuery(id+"F3.wireOp",EDGE,"E367")])]}),makeQuery(id+"F4.opExtrude","SWEPT_FACE",FACE,{"disambiguationData":[OSD([sQuery(id+"F3.wireOp",EDGE,"E368")])]}),makeQuery(id+"F4.opExtrude","SWEPT_FACE",FACE,{"disambiguationData":[OSD([sQuery(id+"F3.wireOp",EDGE,"E369")])]}),makeQuery(id+"F4.opExtrude","SWEPT_FACE",FACE,{"disambiguationData":[OSD([sQuery(id+"F3.wireOp",EDGE,"E370")])]}),makeQuery(id+"F4.opExtrude","SWEPT_FACE",FACE,{"disambiguationData":[OSD([sQuery(id+"F3.wireOp",EDGE,"E371")])]}),makeQuery(id+"F4.opExtrude","SWEPT_FACE",FACE,{"disambiguationData":[OSD([sQuery(id+"F3.wireOp",EDGE,"E372")])]}),makeQuery(id+"F4.opExtrude","SWEPT_FACE",FACE,{"disambiguationData":[OSD([sQuery(id+"F3.wireOp",EDGE,"E373")])]}),makeQuery(id+"F4.opExtrude","SWEPT_FACE",FACE,{"disambiguationData":[OSD([sQuery(id+"F3.wireOp",EDGE,"E374")])]}),makeQuery(id+"F4.opExtrude","SWEPT_FACE",FACE,{"disambiguationData":[OSD([sQuery(id+"F3.wireOp",EDGE,"E375")])]}),makeQuery(id+"F4.opExtrude","SWEPT_FACE",FACE,{"disambiguationData":[OSD([sQuery(id+"F3.wireOp",EDGE,"E376")])]}),makeQuery(id+"F4.opExtrude","SWEPT_FACE",FACE,{"disambiguationData":[OSD([sQuery(id+"F3.wireOp",EDGE,"E377")])]}),makeQuery(id+"F4.opExtrude","SWEPT_FACE",FACE,{"disambiguationData":[OSD([sQuery(id+"F3.wireOp",EDGE,"E378")])]}),makeQuery(id+"F4.opExtrude","SWEPT_FACE",FACE,{"disambiguationData":[OSD([sQuery(id+"F3.wireOp",EDGE,"E379")])]}),makeQuery(id+"F4.opExtrude","SWEPT_FACE",FACE,{"disambiguationData":[OSD([sQuery(id+"F3.wireOp",EDGE,"E380")])]}),makeQuery(id+"F4.opExtrude","SWEPT_FACE",FACE,{"disambiguationData":[OSD([sQuery(id+"F3.wireOp",EDGE,"E381")])]}),makeQuery(id+"F4.opExtrude","SWEPT_FACE",FACE,{"disambiguationData":[OSD([sQuery(id+"F3.wireOp",EDGE,"E382")])]}),makeQuery(id+"F4.opExtrude","SWEPT_FACE",FACE,{"disambiguationData":[OSD([sQuery(id+"F3.wireOp",EDGE,"E383")])]}),makeQuery(id+"F4.opExtrude","SWEPT_FACE",FACE,{"disambiguationData":[OSD([sQuery(id+"F3.wireOp",EDGE,"E384")])]}),makeQuery(id+"F4.opExtrude","SWEPT_FACE",FACE,{"disambiguationData":[OSD([sQuery(id+"F3.wireOp",EDGE,"E385")])]}),makeQuery(id+"F4.opExtrude","SWEPT_FACE",FACE,{"disambiguationData":[OSD([sQuery(id+"F3.wireOp",EDGE,"E386")])]}),makeQuery(id+"F4.opExtrude","SWEPT_FACE",FACE,{"disambiguationData":[OSD([sQuery(id+"F3.wireOp",EDGE,"E387")])]}),makeQuery(id+"F4.opExtrude","SWEPT_FACE",FACE,{"disambiguationData":[OSD([sQuery(id+"F3.wireOp",EDGE,"E388")])]}),makeQuery(id+"F4.opExtrude","SWEPT_FACE",FACE,{"disambiguationData":[OSD([sQuery(id+"F3.wireOp",EDGE,"E389")])]}),makeQuery(id+"F4.opExtrude","SWEPT_FACE",FACE,{"disambiguationData":[OSD([sQuery(id+"F3.wireOp",EDGE,"E390")])]}),makeQuery(id+"F4.opExtrude","SWEPT_FACE",FACE,{"disambiguationData":[OSD([sQuery(id+"F3.wireOp",EDGE,"E391")])]}),makeQuery(id+"F4.opExtrude","SWEPT_FACE",FACE,{"disambiguationData":[OSD([sQuery(id+"F3.wireOp",EDGE,"E392")])]}),makeQuery(id+"F4.opExtrude","SWEPT_FACE",FACE,{"disambiguationData":[OSD([sQuery(id+"F3.wireOp",EDGE,"E393")])]}),makeQuery(id+"F4.opExtrude","SWEPT_FACE",FACE,{"disambiguationData":[OSD([sQuery(id+"F3.wireOp",EDGE,"E394")])]}),makeQuery(id+"F4.opExtrude","SWEPT_FACE",FACE,{"disambiguationData":[OSD([sQuery(id+"F3.wireOp",EDGE,"E698")])]}),makeQuery(id+"F4.opExtrude","SWEPT_FACE",FACE,{"disambiguationData":[OSD([sQuery(id+"F3.wireOp",EDGE,"E699")])]}),makeQuery(id+"F4.opExtrude","SWEPT_FACE",FACE,{"disambiguationData":[OSD([sQuery(id+"F3.wireOp",EDGE,"E700")])]}),makeQuery(id+"F4.opExtrude","SWEPT_FACE",FACE,{"disambiguationData":[OSD([sQuery(id+"F3.wireOp",EDGE,"E701")])]}),makeQuery(id+"F4.opExtrude","SWEPT_FACE",FACE,{"disambiguationData":[OSD([sQuery(id+"F3.wireOp",EDGE,"E702")])]}),makeQuery(id+"F4.opExtrude","SWEPT_FACE",FACE,{"disambiguationData":[OSD([sQuery(id+"F3.wireOp",EDGE,"E703")])]}),makeQuery(id+"F4.opExtrude","SWEPT_FACE",FACE,{"disambiguationData":[OSD([sQuery(id+"F3.wireOp",EDGE,"E704")])]}),makeQuery(id+"F4.opExtrude","SWEPT_FACE",FACE,{"disambiguationData":[OSD([sQuery(id+"F3.wireOp",EDGE,"E705")])]}),makeQuery(id+"F4.opExtrude","SWEPT_FACE",FACE,{"disambiguationData":[OSD([sQuery(id+"F3.wireOp",EDGE,"E706")])]}),makeQuery(id+"F4.opExtrude","SWEPT_FACE",FACE,{"disambiguationData":[OSD([sQuery(id+"F3.wireOp",EDGE,"E707")])]}),makeQuery(id+"F4.opExtrude","SWEPT_FACE",FACE,{"disambiguationData":[OSD([sQuery(id+"F3.wireOp",EDGE,"E708")])]}),makeQuery(id+"F4.opExtrude","SWEPT_FACE",FACE,{"disambiguationData":[OSD([sQuery(id+"F3.wireOp",EDGE,"E709")])]}),makeQuery(id+"F4.opExtrude","SWEPT_FACE",FACE,{"disambiguationData":[OSD([sQuery(id+"F3.wireOp",EDGE,"E710")])]}),makeQuery(id+"F4.opExtrude","SWEPT_FACE",FACE,{"disambiguationData":[OSD([sQuery(id+"F3.wireOp",EDGE,"E711")])]}),makeQuery(id+"F4.opExtrude","SWEPT_FACE",FACE,{"disambiguationData":[OSD([sQuery(id+"F3.wireOp",EDGE,"E712")])]}),makeQuery(id+"F4.opExtrude","SWEPT_FACE",FACE,{"disambiguationData":[OSD([sQuery(id+"F3.wireOp",EDGE,"E713")])]}),makeQuery(id+"F4.opExtrude","SWEPT_FACE",FACE,{"disambiguationData":[OSD([sQuery(id+"F3.wireOp",EDGE,"E714")])]}),makeQuery(id+"F4.opExtrude","SWEPT_FACE",FACE,{"disambiguationData":[OSD([sQuery(id+"F3.wireOp",EDGE,"E715")])]}),makeQuery(id+"F4.opExtrude","SWEPT_FACE",FACE,{"disambiguationData":[OSD([sQuery(id+"F3.wireOp",EDGE,"E716")])]}),makeQuery(id+"F4.opExtrude","SWEPT_FACE",FACE,{"disambiguationData":[OSD([sQuery(id+"F3.wireOp",EDGE,"E717")])]}),makeQuery(id+"F4.opExtrude","SWEPT_FACE",FACE,{"disambiguationData":[OSD([sQuery(id+"F3.wireOp",EDGE,"E718")])]}),makeQuery(id+"F4.opExtrude","SWEPT_FACE",FACE,{"disambiguationData":[OSD([sQuery(id+"F3.wireOp",EDGE,"E719")])]}),makeQuery(id+"F4.opExtrude","SWEPT_FACE",FACE,{"disambiguationData":[OSD([sQuery(id+"F3.wireOp",EDGE,"E720")])]}),makeQuery(id+"F4.opExtrude","SWEPT_FACE",FACE,{"disambiguationData":[OSD([sQuery(id+"F3.wireOp",EDGE,"E721")])]}),makeQuery(id+"F4.opExtrude","SWEPT_FACE",FACE,{"disambiguationData":[OSD([sQuery(id+"F3.wireOp",EDGE,"E888")])]}),makeQuery(id+"F4.opExtrude","SWEPT_FACE",FACE,{"disambiguationData":[OSD([sQuery(id+"F3.wireOp",EDGE,"E889")])]}),makeQuery(id+"F4.opExtrude","SWEPT_FACE",FACE,{"disambiguationData":[OSD([sQuery(id+"F3.wireOp",EDGE,"E890")])]}),makeQuery(id+"F4.opExtrude","SWEPT_FACE",FACE,{"disambiguationData":[OSD([sQuery(id+"F3.wireOp",EDGE,"E891")])]}),makeQuery(id+"F4.opExtrude","SWEPT_FACE",FACE,{"disambiguationData":[OSD([sQuery(id+"F3.wireOp",EDGE,"E892")])]}),makeQuery(id+"F4.opExtrude","SWEPT_FACE",FACE,{"disambiguationData":[OSD([sQuery(id+"F3.wireOp",EDGE,"E893")])]}),makeQuery(id+"F4.opExtrude","SWEPT_FACE",FACE,{"disambiguationData":[OSD([sQuery(id+"F3.wireOp",EDGE,"E894")])]}),makeQuery(id+"F4.opExtrude","SWEPT_FACE",FACE,{"disambiguationData":[OSD([sQuery(id+"F3.wireOp",EDGE,"E895")])]}),makeQuery(id+"F4.opExtrude","SWEPT_FACE",FACE,{"disambiguationData":[OSD([sQuery(id+"F3.wireOp",EDGE,"E896")])]}),makeQuery(id+"F4.opExtrude","SWEPT_FACE",FACE,{"disambiguationData":[OSD([sQuery(id+"F3.wireOp",EDGE,"E897")])]}),makeQuery(id+"F4.opExtrude","SWEPT_FACE",FACE,{"disambiguationData":[OSD([sQuery(id+"F3.wireOp",EDGE,"E898")])]}),makeQuery(id+"F4.opExtrude","SWEPT_FACE",FACE,{"disambiguationData":[OSD([sQuery(id+"F3.wireOp",EDGE,"E899"),sQuery(id+"F3.wireOp",EDGE,"E900")])]}),makeQuery(id+"F4.opExtrude","SWEPT_FACE",FACE,{"disambiguationData":[OSD([sQuery(id+"F3.wireOp",EDGE,"E901")])]}),makeQuery(id+"F4.opExtrude","SWEPT_FACE",FACE,{"disambiguationData":[OSD([sQuery(id+"F3.wireOp",EDGE,"E902")])]}),makeQuery(id+"F4.opExtrude","SWEPT_FACE",FACE,{"disambiguationData":[OSD([sQuery(id+"F3.wireOp",EDGE,"E903")])]}),makeQuery(id+"F4.opExtrude","SWEPT_FACE",FACE,{"disambiguationData":[OSD([sQuery(id+"F3.wireOp",EDGE,"E904")])]}),makeQuery(id+"F4.opExtrude","SWEPT_FACE",FACE,{"disambiguationData":[OSD([sQuery(id+"F3.wireOp",EDGE,"E905")])]}),makeQuery(id+"F4.opExtrude","SWEPT_FACE",FACE,{"disambiguationData":[OSD([sQuery(id+"F3.wireOp",EDGE,"E906")])]}),makeQuery(id+"F4.opExtrude","SWEPT_FACE",FACE,{"disambiguationData":[OSD([sQuery(id+"F3.wireOp",EDGE,"E907")])]}),makeQuery(id+"F4.opExtrude","SWEPT_FACE",FACE,{"disambiguationData":[OSD([sQuery(id+"F3.wireOp",EDGE,"E913")])]}),makeQuery(id+"F4.opExtrude","SWEPT_FACE",FACE,{"disambiguationData":[OSD([sQuery(id+"F3.wireOp",EDGE,"E914")])]}),makeQuery(id+"F4.opExtrude","SWEPT_FACE",FACE,{"disambiguationData":[OSD([sQuery(id+"F3.wireOp",EDGE,"E915")])]}),makeQuery(id+"F4.opExtrude","SWEPT_FACE",FACE,{"disambiguationData":[OSD([sQuery(id+"F3.wireOp",EDGE,"E916")])]}),makeQuery(id+"F4.opExtrude","SWEPT_FACE",FACE,{"disambiguationData":[OSD([sQuery(id+"F3.wireOp",EDGE,"E917")])]}),makeQuery(id+"F4.opExtrude","SWEPT_FACE",FACE,{"disambiguationData":[OSD([sQuery(id+"F3.wireOp",EDGE,"E918")])]}),makeQuery(id+"F4.opExtrude","SWEPT_FACE",FACE,{"disambiguationData":[OSD([sQuery(id+"F3.wireOp",EDGE,"E919")])]}),makeQuery(id+"F4.opExtrude","SWEPT_FACE",FACE,{"disambiguationData":[OSD([sQuery(id+"F3.wireOp",EDGE,"E920")])]}),makeQuery(id+"F4.opExtrude","SWEPT_FACE",FACE,{"disambiguationData":[OSD([sQuery(id+"F3.wireOp",EDGE,"E921")])]}),makeQuery(id+"F4.opExtrude","SWEPT_FACE",FACE,{"disambiguationData":[OSD([sQuery(id+"F3.wireOp",EDGE,"E922")])]}),makeQuery(id+"F4.opExtrude","SWEPT_FACE",FACE,{"disambiguationData":[OSD([sQuery(id+"F3.wireOp",EDGE,"E923")])]}),makeQuery(id+"F4.opExtrude","SWEPT_FACE",FACE,{"disambiguationData":[OSD([sQuery(id+"F3.wireOp",EDGE,"E924")])]}),makeQuery(id+"F4.opExtrude","SWEPT_FACE",FACE,{"disambiguationData":[OSD([sQuery(id+"F3.wireOp",EDGE,"E925")])]}),makeQuery(id+"F4.opExtrude","SWEPT_FACE",FACE,{"disambiguationData":[OSD([sQuery(id+"F3.wireOp",EDGE,"E926")])]}),makeQuery(id+"F4.opExtrude","SWEPT_FACE",FACE,{"disambiguationData":[OSD([sQuery(id+"F3.wireOp",EDGE,"E927")])]}),makeQuery(id+"F4.opExtrude","SWEPT_FACE",FACE,{"disambiguationData":[OSD([sQuery(id+"F3.wireOp",EDGE,"E928")])]}),makeQuery(id+"F4.opExtrude","SWEPT_FACE",FACE,{"disambiguationData":[OSD([sQuery(id+"F3.wireOp",EDGE,"E929")])]}),makeQuery(id+"F4.opExtrude","SWEPT_FACE",FACE,{"disambiguationData":[OSD([sQuery(id+"F3.wireOp",EDGE,"E930")])]}),makeQuery(id+"F4.opExtrude","SWEPT_FACE",FACE,{"disambiguationData":[OSD([sQuery(id+"F3.wireOp",EDGE,"E931")])]}),makeQuery(id+"F4.opExtrude","SWEPT_FACE",FACE,{"disambiguationData":[OSD([sQuery(id+"F3.wireOp",EDGE,"E932")])]}),makeQuery(id+"F4.opExtrude","SWEPT_FACE",FACE,{"disambiguationData":[OSD([sQuery(id+"F3.wireOp",EDGE,"E933")])]}),makeQuery(id+"F4.opExtrude","SWEPT_FACE",FACE,{"disambiguationData":[OSD([sQuery(id+"F3.wireOp",EDGE,"E934")])]}),makeQuery(id+"F4.opExtrude","SWEPT_FACE",FACE,{"disambiguationData":[OSD([sQuery(id+"F3.wireOp",EDGE,"E935")])]}),makeQuery(id+"F4.opExtrude","SWEPT_FACE",FACE,{"disambiguationData":[OSD([sQuery(id+"F3.wireOp",EDGE,"E936")])]}),makeQuery(id+"F4.opExtrude","SWEPT_FACE",FACE,{"disambiguationData":[OSD([sQuery(id+"F3.wireOp",EDGE,"E937")])]}),makeQuery(id+"F4.opExtrude","SWEPT_FACE",FACE,{"disambiguationData":[OSD([sQuery(id+"F3.wireOp",EDGE,"E938")])]}),makeQuery(id+"F4.opExtrude","SWEPT_FACE",FACE,{"disambiguationData":[OSD([sQuery(id+"F3.wireOp",EDGE,"E939")])]}),makeQuery(id+"F4.opExtrude","SWEPT_FACE",FACE,{"disambiguationData":[OSD([sQuery(id+"F3.wireOp",EDGE,"E940")])]}),makeQuery(id+"F4.opExtrude","SWEPT_FACE",FACE,{"disambiguationData":[OSD([sQuery(id+"F3.wireOp",EDGE,"E941")])]}),makeQuery(id+"F4.opExtrude","SWEPT_FACE",FACE,{"disambiguationData":[OSD([sQuery(id+"F3.wireOp",EDGE,"E942")])]}),makeQuery(id+"F4.opExtrude","SWEPT_FACE",FACE,{"disambiguationData":[OSD([sQuery(id+"F3.wireOp",EDGE,"E943")])]}),makeQuery(id+"F4.opExtrude","SWEPT_FACE",FACE,{"disambiguationData":[OSD([sQuery(id+"F3.wireOp",EDGE,"E944")])]}),makeQuery(id+"F4.opExtrude","SWEPT_FACE",FACE,{"disambiguationData":[OSD([sQuery(id+"F3.wireOp",EDGE,"E945")])]}),makeQuery(id+"F4.opExtrude","SWEPT_FACE",FACE,{"disambiguationData":[OSD([sQuery(id+"F3.wireOp",EDGE,"E946")])]}),makeQuery(id+"F4.opExtrude","SWEPT_FACE",FACE,{"disambiguationData":[OSD([sQuery(id+"F3.wireOp",EDGE,"E947")])]}),makeQuery(id+"F4.opExtrude","SWEPT_FACE",FACE,{"disambiguationData":[OSD([sQuery(id+"F3.wireOp",EDGE,"E948")])]}),makeQuery(id+"F4.opExtrude","SWEPT_FACE",FACE,{"disambiguationData":[OSD([sQuery(id+"F3.wireOp",EDGE,"E949")])]}),makeQuery(id+"F4.opExtrude","SWEPT_FACE",FACE,{"disambiguationData":[OSD([sQuery(id+"F3.wireOp",EDGE,"E950")])]}),makeQuery(id+"F4.opExtrude","SWEPT_FACE",FACE,{"disambiguationData":[OSD([sQuery(id+"F3.wireOp",EDGE,"E951")])]}),makeQuery(id+"F4.opExtrude","SWEPT_FACE",FACE,{"disambiguationData":[OSD([sQuery(id+"F3.wireOp",EDGE,"E952")])]}),makeQuery(id+"F4.opExtrude","SWEPT_FACE",FACE,{"disambiguationData":[OSD([sQuery(id+"F3.wireOp",EDGE,"E953")])]}),makeQuery(id+"F4.opExtrude","SWEPT_FACE",FACE,{"disambiguationData":[OSD([sQuery(id+"F3.wireOp",EDGE,"E954")])]}),makeQuery(id+"F4.opExtrude","SWEPT_FACE",FACE,{"disambiguationData":[OSD([sQuery(id+"F3.wireOp",EDGE,"E955")])]}),makeQuery(id+"F4.opExtrude","SWEPT_FACE",FACE,{"disambiguationData":[OSD([sQuery(id+"F3.wireOp",EDGE,"E956")])]}),makeQuery(id+"F4.opExtrude","SWEPT_FACE",FACE,{"disambiguationData":[OSD([sQuery(id+"F3.wireOp",EDGE,"E957")])]}),makeQuery(id+"F4.opExtrude","SWEPT_FACE",FACE,{"disambiguationData":[OSD([sQuery(id+"F3.wireOp",EDGE,"E958")])]}),makeQuery(id+"F4.opExtrude","SWEPT_FACE",FACE,{"disambiguationData":[OSD([sQuery(id+"F3.wireOp",EDGE,"E959")])]}),makeQuery(id+"F4.opExtrude","SWEPT_FACE",FACE,{"disambiguationData":[OSD([sQuery(id+"F3.wireOp",EDGE,"E960")])]}),makeQuery(id+"F4.opExtrude","SWEPT_FACE",FACE,{"disambiguationData":[OSD([sQuery(id+"F3.wireOp",EDGE,"E961")])]}),makeQuery(id+"F4.opExtrude","SWEPT_FACE",FACE,{"disambiguationData":[OSD([sQuery(id+"F3.wireOp",EDGE,"E962")])]}),makeQuery(id+"F4.opExtrude","SWEPT_FACE",FACE,{"disambiguationData":[OSD([sQuery(id+"F3.wireOp",EDGE,"E963")])]}),makeQuery(id+"F4.opExtrude","SWEPT_FACE",FACE,{"disambiguationData":[OSD([sQuery(id+"F3.wireOp",EDGE,"E964")])]}),makeQuery(id+"F4.opExtrude","SWEPT_FACE",FACE,{"disambiguationData":[OSD([sQuery(id+"F3.wireOp",EDGE,"E965")])]}),makeQuery(id+"F4.opExtrude","SWEPT_FACE",FACE,{"disambiguationData":[OSD([sQuery(id+"F3.wireOp",EDGE,"E966")])]}),makeQuery(id+"F4.opExtrude","SWEPT_FACE",FACE,{"disambiguationData":[OSD([sQuery(id+"F3.wireOp",EDGE,"E967")])]}),makeQuery(id+"F4.opExtrude","SWEPT_FACE",FACE,{"disambiguationData":[OSD([sQuery(id+"F3.wireOp",EDGE,"E968")])]}),makeQuery(id+"F4.opExtrude","SWEPT_FACE",FACE,{"disambiguationData":[OSD([sQuery(id+"F3.wireOp",EDGE,"E969")])]}),makeQuery(id+"F4.opExtrude","SWEPT_FACE",FACE,{"disambiguationData":[OSD([sQuery(id+"F3.wireOp",EDGE,"E970")])]}),makeQuery(id+"F4.opExtrude","SWEPT_FACE",FACE,{"disambiguationData":[OSD([sQuery(id+"F3.wireOp",EDGE,"E971")])]}),makeQuery(id+"F4.opExtrude","SWEPT_FACE",FACE,{"disambiguationData":[OSD([sQuery(id+"F3.wireOp",EDGE,"E972")])]}),makeQuery(id+"F4.opExtrude","SWEPT_FACE",FACE,{"disambiguationData":[OSD([sQuery(id+"F3.wireOp",EDGE,"E982")])]}),makeQuery(id+"F4.opExtrude","SWEPT_FACE",FACE,{"disambiguationData":[OSD([sQuery(id+"F3.wireOp",EDGE,"E983")])]}),makeQuery(id+"F4.opExtrude","SWEPT_FACE",FACE,{"disambiguationData":[OSD([sQuery(id+"F3.wireOp",EDGE,"E984")])]}),makeQuery(id+"F4.opExtrude","SWEPT_FACE",FACE,{"disambiguationData":[OSD([sQuery(id+"F3.wireOp",EDGE,"E985")])]}),makeQuery(id+"F4.opExtrude","SWEPT_FACE",FACE,{"disambiguationData":[OSD([sQuery(id+"F3.wireOp",EDGE,"E986")])]}),makeQuery(id+"F4.opExtrude","SWEPT_FACE",FACE,{"disambiguationData":[OSD([sQuery(id+"F3.wireOp",EDGE,"E987")])]}),makeQuery(id+"F4.opExtrude","SWEPT_FACE",FACE,{"disambiguationData":[OSD([sQuery(id+"F3.wireOp",EDGE,"E988")])]}),makeQuery(id+"F4.opExtrude","SWEPT_FACE",FACE,{"disambiguationData":[OSD([sQuery(id+"F3.wireOp",EDGE,"E989")])]}),makeQuery(id+"F4.opExtrude","SWEPT_FACE",FACE,{"disambiguationData":[OSD([sQuery(id+"F3.wireOp",EDGE,"E990")])]}),makeQuery(id+"F4.opExtrude","SWEPT_FACE",FACE,{"disambiguationData":[OSD([sQuery(id+"F3.wireOp",EDGE,"E991")])]}),makeQuery(id+"F4.opExtrude","SWEPT_FACE",FACE,{"disambiguationData":[OSD([sQuery(id+"F3.wireOp",EDGE,"E992")])]}),makeQuery(id+"F4.opExtrude","SWEPT_FACE",FACE,{"disambiguationData":[OSD([sQuery(id+"F3.wireOp",EDGE,"E993")])]}),makeQuery(id+"F4.opExtrude","SWEPT_FACE",FACE,{"disambiguationData":[OSD([sQuery(id+"F3.wireOp",EDGE,"E994")])]}),makeQuery(id+"F4.opExtrude","SWEPT_FACE",FACE,{"disambiguationData":[OSD([sQuery(id+"F3.wireOp",EDGE,"E995")])]}),makeQuery(id+"F4.opExtrude","SWEPT_FACE",FACE,{"disambiguationData":[OSD([sQuery(id+"F3.wireOp",EDGE,"E996")])]}),makeQuery(id+"F4.opExtrude","SWEPT_FACE",FACE,{"disambiguationData":[OSD([sQuery(id+"F3.wireOp",EDGE,"E997")])]}),makeQuery(id+"F4.opExtrude","SWEPT_FACE",FACE,{"disambiguationData":[OSD([sQuery(id+"F3.wireOp",EDGE,"E998")])]}),makeQuery(id+"F4.opExtrude","SWEPT_FACE",FACE,{"disambiguationData":[OSD([sQuery(id+"F3.wireOp",EDGE,"FdFcAiBO-ON24-jFwk-7KOQ-EmIEps3LklzC")])]}),makeQuery(id+"F4.opExtrude","SWEPT_FACE",FACE,{"disambiguationData":[OSD([sQuery(id+"F3.wireOp",EDGE,"ysPcMRTr-CDba-Jo9G-BDWK-J5wc3SDX7p4u")])]}),makeQuery(id+"F4.opExtrude","SWEPT_FACE",FACE,{"disambiguationData":[OSD([sQuery(id+"F3.wireOp",EDGE,"vdfo7SUS-2qYI-YUpW-azbw-TsPRVRUnNGmC")])]}),makeQuery(id+"F4.opExtrude","SWEPT_FACE",FACE,{"disambiguationData":[OSD([sQuery(id+"F3.wireOp",EDGE,"JwKaMSSL-dmdz-AKYG-gjAR-02H6QUGJ043I")])]})])],"derivedFrom":makeQuery(id+"F1.opRevolve","SWEPT_FACE",FACE,{"disambiguationData":[OSD([sQuery(id+"F0.wireOp",EDGE,"E0")])]})}),makeQuery(id+"F8.opExtrude","SWEPT_FACE",FACE,{"disambiguationData":[OSD([sQuery(id+"F7.wireOp",EDGE,"E1083")])]})]});
            fillet(context, id + "F9", {"entities" : qUnion([Q0]), "radius" : 1 * mm, "tangentPropagation" : true, "allowEdgeOverflow" : false});
        }
        {
            var Q0;
            Q0=qCreatedBy(makeId("Top.planeOp"),FACE);
            var sketch = newSketch(context, id + "F10", { "sketchPlane" : qUnion([Q0])});
            skLineSegment(sketch, "E1084.bottom", {"start": v(-2.57, 0.8) * mm, "end": v(-1.9, 0.8) * mm});
            skLineSegment(sketch, "E1084.top", {"start": v(-2.57, -6.3) * mm, "end": v(-1.9, -6.3) * mm});
            skLineSegment(sketch, "E1084.left", {"start": v(-2.57, 0.8) * mm, "end": v(-2.57, -6.3) * mm});
            skLineSegment(sketch, "E1084.right", {"start": v(-1.9, 0.8) * mm, "end": v(-1.9, -6.3) * mm});
            skLineSegment(sketch, "E1085.bottom", {"start": v(-5.66, -2.15) * mm, "end": v(0.72, -2.15) * mm});
            skLineSegment(sketch, "E1085.top", {"start": v(-5.66, -1.71) * mm, "end": v(0.72, -1.71) * mm});
            skLineSegment(sketch, "E1085.left", {"start": v(-5.66, -2.15) * mm, "end": v(-5.66, -1.71) * mm});
            skLineSegment(sketch, "E1085.right", {"start": v(0.72, -2.15) * mm, "end": v(0.72, -1.71) * mm});
            skLineSegment(sketch, "E1086.bottom", {"start": v(7.6, 2.9) * mm, "end": v(4.72, 2.9) * mm});
            skLineSegment(sketch, "E1086.top", {"start": v(7.6, 2.26) * mm, "end": v(4.72, 2.26) * mm});
            skLineSegment(sketch, "E1086.left", {"start": v(7.6, 2.9) * mm, "end": v(7.6, 2.26) * mm});
            skLineSegment(sketch, "E1086.right", {"start": v(4.72, 2.9) * mm, "end": v(4.72, 2.26) * mm});
            skLineSegment(sketch, "E1087.bottom", {"start": v(2.8, 1.5) * mm, "end": v(-1.2, 1.5) * mm});
            skLineSegment(sketch, "E1087.top", {"start": v(2.8, 2.04) * mm, "end": v(-1.2, 2.04) * mm});
            skLineSegment(sketch, "E1087.left", {"start": v(2.8, 1.5) * mm, "end": v(2.8, 2.04) * mm});
            skLineSegment(sketch, "E1087.right", {"start": v(-1.2, 1.5) * mm, "end": v(-1.2, 2.04) * mm});
            skLineSegment(sketch, "E1088.bottom", {"start": v(-3.29, 5.9) * mm, "end": v(-2.42, 5.9) * mm});
            skLineSegment(sketch, "E1088.top", {"start": v(-3.29, 9.37) * mm, "end": v(-2.42, 9.37) * mm});
            skLineSegment(sketch, "E1088.left", {"start": v(-3.29, 5.9) * mm, "end": v(-3.29, 9.37) * mm});
            skLineSegment(sketch, "E1088.right", {"start": v(-2.42, 5.9) * mm, "end": v(-2.42, 9.37) * mm});
            skLineSegment(sketch, "E1089.bottom", {"start": v(-3.43, 3.27) * mm, "end": v(-10.72, 3.27) * mm});
            skLineSegment(sketch, "E1089.top", {"start": v(-3.43, 2.7) * mm, "end": v(-10.72, 2.7) * mm});
            skLineSegment(sketch, "E1089.left", {"start": v(-3.43, 3.27) * mm, "end": v(-3.43, 2.7) * mm});
            skLineSegment(sketch, "E1089.right", {"start": v(-10.72, 3.27) * mm, "end": v(-10.72, 2.7) * mm});
            skLineSegment(sketch, "E1090.bottom", {"start": v(4.64, -0.96) * mm, "end": v(4.13, -0.96) * mm});
            skLineSegment(sketch, "E1090.top", {"start": v(4.64, -4.18) * mm, "end": v(4.13, -4.18) * mm});
            skLineSegment(sketch, "E1090.left", {"start": v(4.64, -0.96) * mm, "end": v(4.64, -4.18) * mm});
            skLineSegment(sketch, "E1090.right", {"start": v(4.13, -0.96) * mm, "end": v(4.13, -4.18) * mm});
            skLineSegment(sketch, "E1091.bottom", {"start": v(-5.57, -3.9) * mm, "end": v(-2.2, -3.9) * mm});
            skLineSegment(sketch, "E1091.top", {"start": v(-5.57, -3) * mm, "end": v(-2.2, -3) * mm});
            skLineSegment(sketch, "E1091.left", {"start": v(-5.57, -3.9) * mm, "end": v(-5.57, -3) * mm});
            skLineSegment(sketch, "E1091.right", {"start": v(-2.2, -3.9) * mm, "end": v(-2.2, -3) * mm});
            skLineSegment(sketch, "E1092.bottom", {"start": v(-1.2, 8.92) * mm, "end": v(-0.41, 8.92) * mm});
            skLineSegment(sketch, "E1092.top", {"start": v(-1.2, 4.13) * mm, "end": v(-0.41, 4.13) * mm});
            skLineSegment(sketch, "E1092.left", {"start": v(-1.2, 8.92) * mm, "end": v(-1.2, 4.13) * mm});
            skLineSegment(sketch, "E1092.right", {"start": v(-0.41, 8.92) * mm, "end": v(-0.41, 4.13) * mm});
            skLineSegment(sketch, "E1093.bottom", {"start": v(3.73, 4.3) * mm, "end": v(7.5, 4.3) * mm});
            skLineSegment(sketch, "E1093.top", {"start": v(3.73, 5.3) * mm, "end": v(7.5, 5.3) * mm});
            skLineSegment(sketch, "E1093.left", {"start": v(3.73, 4.3) * mm, "end": v(3.73, 5.3) * mm});
            skLineSegment(sketch, "E1093.right", {"start": v(7.5, 4.3) * mm, "end": v(7.5, 5.3) * mm});
            skLineSegment(sketch, "E1094.bottom", {"start": v(3.53, 3.9) * mm, "end": v(3.79, 3.9) * mm});
            skLineSegment(sketch, "E1094.top", {"start": v(3.53, 2.67) * mm, "end": v(3.79, 2.67) * mm});
            skLineSegment(sketch, "E1094.left", {"start": v(3.53, 3.9) * mm, "end": v(3.53, 2.67) * mm});
            skLineSegment(sketch, "E1094.right", {"start": v(3.79, 3.9) * mm, "end": v(3.79, 2.67) * mm});
            skSolve(sketch);
        }
        {
            var Q0;
            Q0=makeQuery(id+"F10.imprint","IMPRINT",FACE,{"disambiguationData":[TD([[makeQuery(id+"F10.imprint","IMPRINT",EDGE,{"derivedFrom":sQuery(id+"F10.wireOp",EDGE,"E1090.bottom")}),1.0]])]});
            var Q1;
            Q1=makeQuery(id+"F10.imprint","IMPRINT",FACE,{"disambiguationData":[TD([[makeQuery(id+"F10.imprint","IMPRINT",EDGE,{"derivedFrom":sQuery(id+"F10.wireOp",EDGE,"E1086.bottom")}),1.0]])]});
            var Q2;
            Q2=makeQuery(id+"F10.imprint","IMPRINT",FACE,{"disambiguationData":[TD([[makeQuery(id+"F10.imprint","IMPRINT",EDGE,{"derivedFrom":sQuery(id+"F10.wireOp",EDGE,"E1087.bottom")}),-1.0]])]});
            var Q3;
            {var subQ5=sQuery(id+"F10.wireOp",EDGE,"E1085.right");Q3=makeQuery(id+"F10.imprint","IMPRINT",FACE,{"disambiguationData":[TD([[makeQuery(id+"F10.imprint","IMPRINT",EDGE,{"derivedFrom":subQ5}),1.0]])]});}
            var Q4;
            {var subQ0=sQuery(id+"F10.wireOp",EDGE,"E1085.top");var subQ1=sQuery(id+"F10.wireOp",EDGE,"E1084.left");var subQ2=makeQuery(id+"F10.imprint","INTERSECT",VERTEX,{"derivedFrom":[subQ1,subQ0]});Q4=makeQuery(id+"F10.imprint","IMPRINT",FACE,{"disambiguationData":[TD([[makeQuery(id+"F10.imprint","IMPRINT",EDGE,{"disambiguationData":[TD([[subQ2,-1.0]])],"derivedFrom":subQ1}),1.0]])]});}
            var Q5;
            {var subQ0=sQuery(id+"F10.wireOp",EDGE,"E1084.bottom");Q5=makeQuery(id+"F10.imprint","IMPRINT",FACE,{"disambiguationData":[TD([[makeQuery(id+"F10.imprint","IMPRINT",EDGE,{"derivedFrom":subQ0}),-1.0]])]});}
            var Q6;
            {var subQ5=sQuery(id+"F10.wireOp",EDGE,"E1085.left");Q6=makeQuery(id+"F10.imprint","IMPRINT",FACE,{"disambiguationData":[TD([[makeQuery(id+"F10.imprint","IMPRINT",EDGE,{"derivedFrom":subQ5}),-1.0]])]});}
            var Q7;
            {var subQ0=sQuery(id+"F10.wireOp",EDGE,"E1084.top");Q7=makeQuery(id+"F10.imprint","IMPRINT",FACE,{"disambiguationData":[TD([[makeQuery(id+"F10.imprint","IMPRINT",EDGE,{"derivedFrom":subQ0}),1.0]])]});}
            var Q8;
            Q8=makeQuery(id+"F10.imprint","IMPRINT",FACE,{"disambiguationData":[TD([[makeQuery(id+"F10.imprint","IMPRINT",EDGE,{"derivedFrom":sQuery(id+"F10.wireOp",EDGE,"E1089.bottom")}),1.0]])]});
            var Q9;
            Q9=makeQuery(id+"F10.imprint","IMPRINT",FACE,{"disambiguationData":[TD([[makeQuery(id+"F10.imprint","IMPRINT",EDGE,{"derivedFrom":sQuery(id+"F10.wireOp",EDGE,"E1088.bottom")}),1.0]])]});
            var Q10;
            {var subQ5=sQuery(id+"F10.wireOp",EDGE,"E1091.left");Q10=makeQuery(id+"F10.imprint","IMPRINT",FACE,{"disambiguationData":[TD([[makeQuery(id+"F10.imprint","IMPRINT",EDGE,{"derivedFrom":subQ5}),-1.0]])]});}
            var Q11;
            {var subQ5=sQuery(id+"F10.wireOp",EDGE,"E1091.right");Q11=makeQuery(id+"F10.imprint","IMPRINT",FACE,{"disambiguationData":[TD([[makeQuery(id+"F10.imprint","IMPRINT",EDGE,{"derivedFrom":subQ5}),1.0]])]});}
            var Q12;
            Q12=makeQuery(id+"F10.imprint","IMPRINT",FACE,{"disambiguationData":[TD([[makeQuery(id+"F10.imprint","IMPRINT",EDGE,{"derivedFrom":sQuery(id+"F10.wireOp",EDGE,"E1092.bottom")}),-1.0]])]});
            var Q13;
            Q13=makeQuery(id+"F10.imprint","IMPRINT",FACE,{"disambiguationData":[TD([[makeQuery(id+"F10.imprint","IMPRINT",EDGE,{"derivedFrom":sQuery(id+"F10.wireOp",EDGE,"E1093.bottom")}),1.0]])]});
            var Q14;
            Q14=makeQuery(id+"F10.imprint","IMPRINT",FACE,{"disambiguationData":[TD([[makeQuery(id+"F10.imprint","IMPRINT",EDGE,{"derivedFrom":sQuery(id+"F10.wireOp",EDGE,"E1094.bottom")}),-1.0]])]});
            extrude(context, id + "F11", {"entities" : qUnion([Q0, Q1, Q2, Q3, Q4, Q5, Q6, Q7, Q8, Q9, Q10, Q11, Q12, Q13, Q14]), "operationType" : NewBodyOperationType.ADD, "depth" : 2 * mm, "offsetDistance" : 25 * mm});
        }
    });
